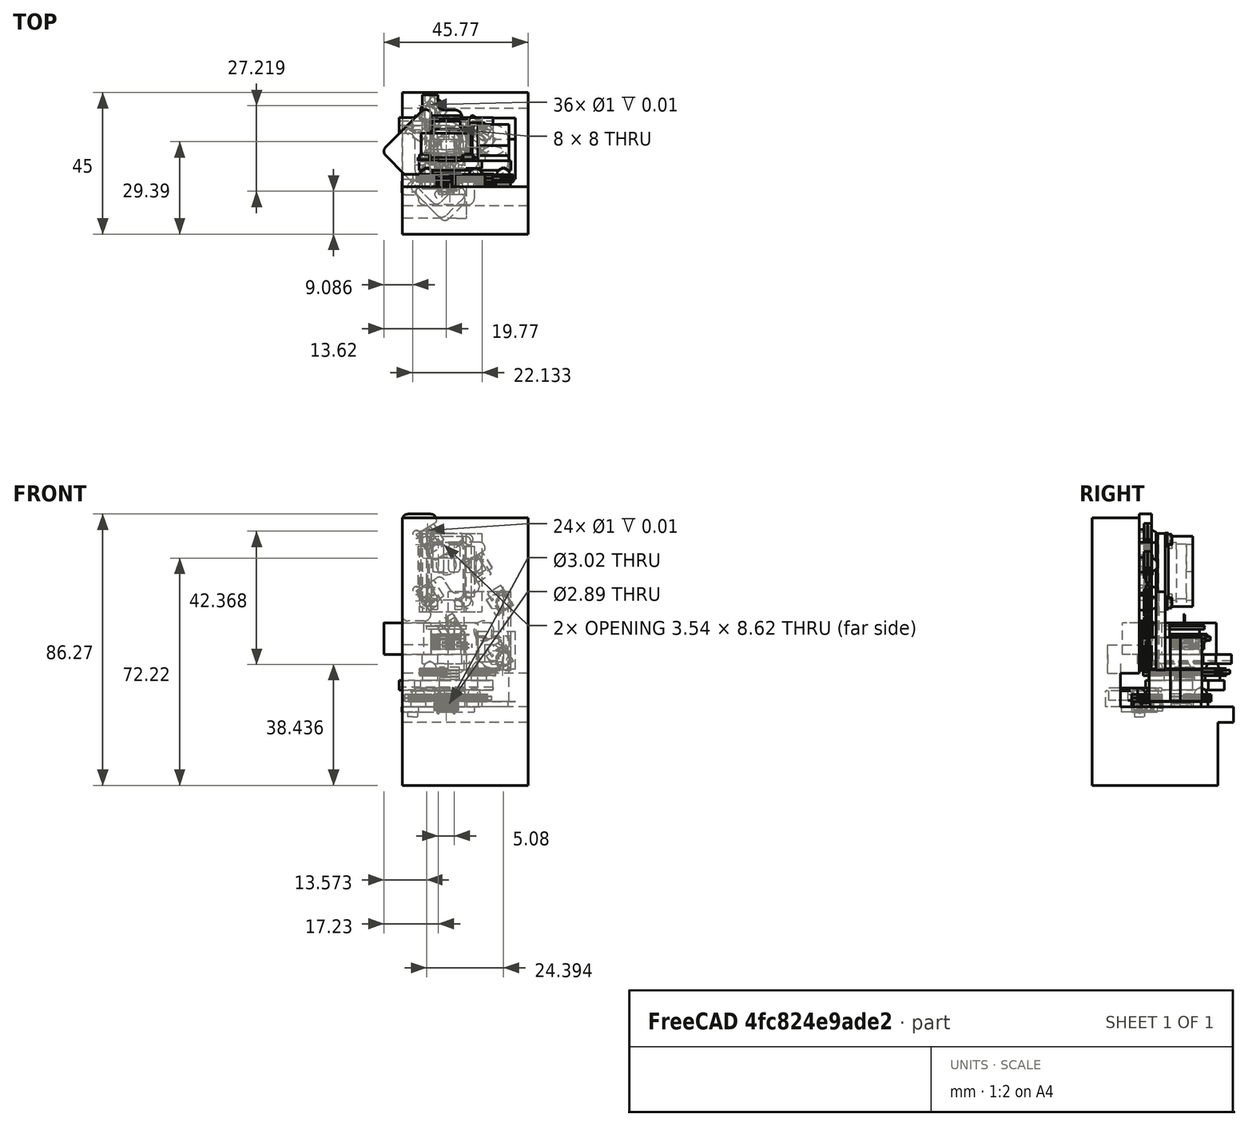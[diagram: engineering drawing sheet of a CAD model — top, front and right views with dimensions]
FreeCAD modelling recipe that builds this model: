
FCSTD DOCUMENT  (FreeCAD 1.1R20260223 (Git shallow))
Label: PhaseII
License: All rights reserved
LicenseURL: https://en.wikipedia.org/wiki/All_rights_reserved
objects: Part::Box×200, Part::Cut×118, Part::Cylinder×102, App::DocumentObjectGroup×31, Sketcher::SketchObject×30, App::Point×20, PartDesign::Pocket×18, Part::Feature×15, Part::Sphere×13, PartDesign::Fillet×13, PartDesign::Pad×11, PartDesign::Body×11, App::Part×9, App::Link×3, Fem::ConstraintFixed×2, PartDesign::CoordinateSystem×1, Fem::FemSolverObjectPython×1, App::MaterialObjectPython×1, Fem::FemMeshShapeBaseObjectPython×1, Fem::FemAnalysis×1
note: 646 computed .brp shape members not serialized (recipe doc carries the construction recipe); baked Part::Feature solids carry a one-line shape summary decoded from their .brp

FEATURE [App::Point] Origin027  label="Origin035"
  Role = Origin
FEATURE [Sketcher::SketchObject] Sketch003
  ArcFitTolerance = 1e-06
  AttachmentSupport = -> [Origin026]
  ExternalTypes = [0]
  FullyConstrained = true
  MakeInternals = false
  MapMode = 5
  sketch-geometry (4):
    g0: LineSegment StartX=7.94 StartY=11.17 StartZ=0 EndX=-7.94 EndY=11.17 EndZ=0
    g1: LineSegment StartX=-7.94 StartY=11.17 StartZ=0 EndX=-7.94 EndY=-11.17 EndZ=0
    g2: LineSegment StartX=-7.94 StartY=-11.17 StartZ=0 EndX=7.94 EndY=-11.17 EndZ=0
    g3: LineSegment StartX=7.94 StartY=-11.17 StartZ=0 EndX=7.94 EndY=11.17 EndZ=0
  constraints (12):
    c: Coincident(g0,g1)
    c: Coincident(g1,g2)
    c: Coincident(g2,g3)
    c: Coincident(g3,g0)
    c: Horizontal(g0)
    c: Horizontal(g2)
    c: Vertical(g1)
    c: Vertical(g3)
    c: DistanceY(g1,g1) = 22.34
    c: DistanceX(g0,g0) = 15.88
    c: Distance(g-1,g0) = 11.17
    c: Distance(g-1,g1) = 7.94
FEATURE [PartDesign::Pad] Pad001
  Direction = (0,0,1)
  Length = 7.7
  Length2 = 10
  Profile = -> Sketch003
  ReferenceAxis = -> Sketch003 [N_Axis]
  Refine = true
  SideType = 0
  Suppressed = false
  Type = 0
  Type2 = 0
FEATURE [Sketcher::SketchObject] Sketch004
  ArcFitTolerance = 1e-06
  AttachmentSupport = -> [Origin026]
  ExternalTypes = [0]
  FullyConstrained = true
  MakeInternals = false
  MapMode = 5
  sketch-geometry (8):
    g0: LineSegment StartX=-3.69 StartY=8.67 StartZ=0 EndX=3.69 EndY=8.67 EndZ=0
    g1: LineSegment StartX=5.44 StartY=6.92 StartZ=0 EndX=5.44 EndY=-6.92 EndZ=0
    g2: LineSegment StartX=3.69 StartY=-8.67 StartZ=0 EndX=-3.69 EndY=-8.67 EndZ=0
    g3: LineSegment StartX=-5.44 StartY=-6.92 StartZ=0 EndX=-5.44 EndY=6.92 EndZ=0
    g4: ArcOfCircle CenterX=-3.69 CenterY=6.92 CenterZ=0 NormalX=0 NormalY=0 NormalZ=1 AngleXU=0 Radius=1.75 StartAngle=1.5708 EndAngle=3.14159
    g5: ArcOfCircle CenterX=3.69 CenterY=6.92 CenterZ=0 NormalX=0 NormalY=0 NormalZ=1 AngleXU=0 Radius=1.75 StartAngle=0 EndAngle=1.5708
    g6: ArcOfCircle CenterX=-3.69 CenterY=-6.92 CenterZ=0 NormalX=0 NormalY=0 NormalZ=1 AngleXU=0 Radius=1.75 StartAngle=3.14159 EndAngle=4.71239
    g7: ArcOfCircle CenterX=3.69 CenterY=-6.92 CenterZ=0 NormalX=0 NormalY=0 NormalZ=1 AngleXU=0 Radius=1.75 StartAngle=4.71239 EndAngle=6.28319
  constraints (20):
    c: Horizontal(g0)
    c: Vertical(g1)
    c: Horizontal(g2)
    c: Vertical(g3)
    c: Radius(g4) = 1.75
    c: Distance(g-1,g0) = 8.67
    c: Distance(g-1,g2) = 8.67
    c: Distance(g-1,g1) = 5.44
    c: Distance(g-1,g3) = 5.44
    c: Tangent(g0,g4) = 1.5708
    c: Tangent(g3,g4) = 1.5708
    c: Radius(g5) = 1.75
    c: Tangent(g1,g5) = 1.5708
    c: Tangent(g5,g0) = 1.5708
    c: Radius(g6) = 1.75
    c: Radius(g7) = 1.75
    c: Tangent(g6,g3) = 1.5708
    c: Tangent(g2,g6) = 1.5708
    c: Tangent(g7,g1) = 1.5708
    c: Tangent(g7,g2) = 1.5708
FEATURE [Sketcher::SketchObject] Sketch006
  ArcFitTolerance = 1e-06
  AttachmentSupport = -> [Origin026]
  ExternalTypes = [0]
  FullyConstrained = true
  MakeInternals = false
  MapMode = 5
  sketch-geometry (14):
    g0: LineSegment StartX=5.99 StartY=6.92 StartZ=0 EndX=5.99 EndY=-6.92 EndZ=0
    g1: LineSegment StartX=3.69 StartY=-9.22 StartZ=0 EndX=-3.69 EndY=-9.22 EndZ=0
    g2: LineSegment StartX=-5.99 StartY=-6.92 StartZ=0 EndX=-5.99 EndY=6.92 EndZ=0
    g3: ArcOfCircle CenterX=-3.69 CenterY=6.92 CenterZ=0 NormalX=0 NormalY=0 NormalZ=1 AngleXU=0 Radius=2.3 StartAngle=1.5708 EndAngle=3.14159
    g4: ArcOfCircle CenterX=3.69 CenterY=6.92 CenterZ=0 NormalX=0 NormalY=0 NormalZ=1 AngleXU=0 Radius=2.3 StartAngle=0 EndAngle=1.5708
    g5: ArcOfCircle CenterX=-3.69 CenterY=-6.92 CenterZ=0 NormalX=0 NormalY=0 NormalZ=1 AngleXU=0 Radius=2.3 StartAngle=3.14159 EndAngle=4.71239
    g6: ArcOfCircle CenterX=3.69 CenterY=-6.92 CenterZ=0 NormalX=0 NormalY=0 NormalZ=1 AngleXU=0 Radius=2.3 StartAngle=4.71239 EndAngle=6.28319
    g7: LineSegment StartX=2.72 StartY=11.17 StartZ=0 EndX=2.72 EndY=9.97 EndZ=0
    g8: LineSegment StartX=-2.72 StartY=11.17 StartZ=0 EndX=-2.72 EndY=9.97 EndZ=0
    g9: LineSegment StartX=2.72 StartY=11.17 StartZ=0 EndX=-2.72 EndY=11.17 EndZ=0
    g10: LineSegment StartX=3.69 StartY=9.22 StartZ=0 EndX=3.47 EndY=9.22 EndZ=0
    g11: LineSegment StartX=-3.69 StartY=9.22 StartZ=0 EndX=-3.47 EndY=9.22 EndZ=0
    g12: ArcOfCircle CenterX=-3.47 CenterY=9.97 CenterZ=0 NormalX=0 NormalY=0 NormalZ=1 AngleXU=0 Radius=0.75 StartAngle=4.71239 EndAngle=6.28319
    g13: ArcOfCircle CenterX=3.47 CenterY=9.97 CenterZ=0 NormalX=0 NormalY=0 NormalZ=1 AngleXU=0 Radius=0.75 StartAngle=3.14159 EndAngle=4.71239
  constraints (37):
    c: Vertical(g0)
    c: Horizontal(g1)
    c: Vertical(g2)
    c: Distance(g-1,g0) = 5.99
    c: Tangent(g2,g3) = 1.5708
    c: Radius(g4) = 2.3
    c: Tangent(g0,g4) = 1.5708
    c: Tangent(g5,g2) = 1.5708
    c: Tangent(g1,g5) = 1.5708
    c: Tangent(g6,g0) = 1.5708
    c: Tangent(g6,g1) = 1.5708
    c: Vertical(g7)
    c: Vertical(g8)
    c: Distance(g-1,g7) = 2.72
    c: Distance(g-1,g8) = 2.72
    c: Coincident(g9,g7)
    c: Coincident(g9,g8)
    c: Horizontal(g9)
    c: Distance(g-1,g9) = 11.17
    c: Coincident(g10,g4)
    c: Horizontal(g10)
    c: Coincident(g11,g3)
    c: Horizontal(g11)
    c: Radius(g13) = 0.75
    c: Radius(g12) = 0.75
    c: Distance(g-1,g11) = 9.22
    c: Distance(g-1,g10) = 9.22
    c: Tangent(g12,g11) = -1.5708
    c: Tangent(g12,g8) = 1.5708
    c: Tangent(g13,g10) = 1.5708
    c: Tangent(g13,g7) = -1.5708
    c: Angle(g3) = 1.5708
    c: Angle(g4) = 1.5708
    c: Equal(g6,g4)
    c: Equal(g4,g3)
    c: Equal(g3,g5)
    c: Symmetric(g0,g2,g-1)
FEATURE [Part::Cylinder] Cylinder013  label="KJ_D21SH"
  Angle = 360
  AttacherType = Attacher::AttachEngine3D
  FirstAngle = 0
  Height = 1.59
  Placement = pos=(6.94,8.74,32.91) rot=(1,0,0;4.71239rad)
  Radius = 1.59
  SecondAngle = 0
FEATURE [Part::Cylinder] Cylinder014  label="KJ_D21SH001"
  Angle = 360
  AttacherType = Attacher::AttachEngine3D
  FirstAngle = 0
  Height = 1.59
  Placement = pos=(6.94,8.74,53.25) rot=(1,0,0;4.71239rad)
  Radius = 1.59
  SecondAngle = 0
FEATURE [Part::Cylinder] Cylinder015  label="KJ_D21SH002"
  Angle = 360
  AttacherType = Attacher::AttachEngine3D
  FirstAngle = 0
  Height = 1.59
  Placement = pos=(-6.94,8.74,32.91) rot=(1,0,0;4.71239rad)
  Radius = 1.59
  SecondAngle = 0
FEATURE [Part::Cylinder] Cylinder016  label="KJ_D21SH003"
  Angle = 360
  AttacherType = Attacher::AttachEngine3D
  FirstAngle = 0
  Height = 1.59
  Placement = pos=(-6.94,8.74,53.25) rot=(1,0,0;4.71239rad)
  Radius = 1.59
  SecondAngle = 0
FEATURE [Part::Box] Box046  label="Conductive Gasket"
  AttacherType = Attacher::AttachEngine3D
  Height = 1
  Length = 3
  Placement = pos=(5.94,8.33,51.08) rot=(1,0,0;4.71239rad)
  Width = 16
FEATURE [Part::Box] Box047  label="Conductive Gasket001"
  AttacherType = Attacher::AttachEngine3D
  Height = 1
  Length = 3
  Placement = pos=(-8.94,8.33,51.08) rot=(1,0,0;4.71239rad)
  Width = 16
FEATURE [Part::Box] Box048  label="Conductive Gasket002"
  AttacherType = Attacher::AttachEngine3D
  Height = 1
  Length = 10
  Placement = pos=(-5,8.33,55.25) rot=(1,0,0;4.71239rad)
  Width = 3
FEATURE [Part::Box] Box049  label="Conductive Gasket003"
  AttacherType = Attacher::AttachEngine3D
  Height = 1
  Length = 2.3
  Placement = pos=(2.72,8.33,33.91) rot=(1,0,0;4.71239rad)
  Width = 3
FEATURE [Part::Box] Box050  label="Conductive Gasket004"
  AttacherType = Attacher::AttachEngine3D
  Height = 1
  Length = 2.3
  Placement = pos=(-5.02,8.33,33.91) rot=(1,0,0;4.71239rad)
  Width = 3
FEATURE [App::DocumentObjectGroup] Group006  label="PreAmp Shield Gasket"
  Group = -> [Cylinder013,Cylinder014,Cylinder015,Cylinder016,Box046,Box047,Box048,Box049,Box050]
FEATURE [Sketcher::SketchObject] Sketch007
  ArcFitTolerance = 1e-06
  AttachmentSupport = -> [Origin026]
  ExternalTypes = [0]
  FullyConstrained = true
  MakeInternals = false
  MapMode = 5
  sketch-geometry (4):
    g0: LineSegment StartX=2.72 StartY=11.17 StartZ=0 EndX=-2.72 EndY=11.17 EndZ=0
    g1: LineSegment StartX=-2.72 StartY=11.17 StartZ=0 EndX=-2.72 EndY=8.5 EndZ=0
    g2: LineSegment StartX=-2.72 StartY=8.5 StartZ=0 EndX=2.72 EndY=8.5 EndZ=0
    g3: LineSegment StartX=2.72 StartY=8.5 StartZ=0 EndX=2.72 EndY=11.17 EndZ=0
  constraints (12):
    c: Coincident(g0,g1)
    c: Coincident(g1,g2)
    c: Coincident(g2,g3)
    c: Coincident(g3,g0)
    c: Horizontal(g0)
    c: Horizontal(g2)
    c: Vertical(g1)
    c: Vertical(g3)
    c: Distance(g-1,g3) = 2.72
    c: Distance(g-1,g1) = 2.72
    c: Distance(g-1,g0) = 11.17
    c: Distance(g-1,g2) = 8.5
FEATURE [Sketcher::SketchObject] Sketch008
  ArcFitTolerance = 1e-06
  AttachmentSupport = -> [Origin026]
  ExternalTypes = [0]
  FullyConstrained = true
  MakeInternals = false
  MapMode = 5
  sketch-geometry (6):
    g0: LineSegment StartX=2.72 StartY=11.17 StartZ=0 EndX=2.72 EndY=9.97 EndZ=0
    g1: LineSegment StartX=-2.72 StartY=11.17 StartZ=0 EndX=-2.72 EndY=9.97 EndZ=0
    g2: LineSegment StartX=2.72 StartY=11.17 StartZ=0 EndX=-2.72 EndY=11.17 EndZ=0
    g3: LineSegment StartX=1.97 StartY=9.22 StartZ=0 EndX=-1.97 EndY=9.22 EndZ=0
    g4: ArcOfCircle CenterX=1.97 CenterY=9.97 CenterZ=0 NormalX=0 NormalY=0 NormalZ=1 AngleXU=0 Radius=0.75 StartAngle=4.71239 EndAngle=6.28319
    g5: ArcOfCircle CenterX=-1.97 CenterY=9.97 CenterZ=0 NormalX=0 NormalY=0 NormalZ=1 AngleXU=0 Radius=0.75 StartAngle=3.14159 EndAngle=4.71239
  constraints (16):
    c: Vertical(g1)
    c: Coincident(g2,g0)
    c: Coincident(g2,g1)
    c: Horizontal(g2)
    c: Horizontal(g3)
    c: Vertical(g0)
    c: Distance(g-1,g2) = 11.17
    c: Distance(g-1,g3) = 9.22
    c: Distance(g-1,g1) = 2.72
    c: Distance(g-1,g0) = 2.72
    c: Radius(g4) = 0.75
    c: Tangent(g4,g0) = 1.5708
    c: Tangent(g4,g3) = 1.5708
    c: Tangent(g1,g5) = -1.5708
    c: Tangent(g5,g3) = 1.5708
    c: Radius(g5) = 0.75
FEATURE [PartDesign::Pocket] Pocket002
  BaseFeature = -> Pad001
  Direction = (0,0,-1)
  Length = 5.7
  Length2 = 5
  Profile = -> Sketch004
  ReferenceAxis = -> Sketch004 [N_Axis]
  Refine = true
  Reversed = true
  SideType = 0
  Suppressed = false
  Type = 0
  Type2 = 0
FEATURE [PartDesign::Pocket] Pocket003
  BaseFeature = -> Pocket002
  Direction = (0,0,-1)
  Length = 2.52
  Length2 = 5
  Profile = -> Sketch006
  ReferenceAxis = -> Sketch006 [N_Axis]
  Refine = true
  Reversed = true
  SideType = 0
  Suppressed = false
  Type = 0
  Type2 = 0
FEATURE [PartDesign::Pocket] Pocket004
  BaseFeature = -> Pocket003
  Direction = (0,0,-1)
  Length = 5.7
  Length2 = 5
  Profile = -> Sketch007
  ReferenceAxis = -> Sketch007 [N_Axis]
  Refine = true
  Reversed = true
  SideType = 0
  Suppressed = false
  Type = 0
  Type2 = 0
FEATURE [PartDesign::Pocket] Pocket005
  BaseFeature = -> Pocket004
  Direction = (0,0,-1)
  Length = 9
  Length2 = 5
  Profile = -> Sketch008
  ReferenceAxis = -> Sketch008 [N_Axis]
  Refine = true
  Reversed = true
  SideType = 0
  Suppressed = false
  Type = 1
  Type2 = 0
FEATURE [Sketcher::SketchObject] Sketch009
  ArcFitTolerance = 1e-06
  AttachmentOffset = pos=(0,0,7.7) rot=(0,0,1;0rad)
  AttachmentSupport = -> [Origin026]
  ExternalTypes = [0]
  FullyConstrained = true
  MakeInternals = false
  MapMode = 5
  Placement = pos=(0,0,7.7) rot=(0,0,1;0rad)
  sketch-geometry (18):
    g0: LineSegment StartX=-0.77 StartY=-0.58 StartZ=0 EndX=-0.77 EndY=-7.7 EndZ=0
    g1: LineSegment StartX=-4.31 StartY=-7.7 StartZ=0 EndX=-4.31 EndY=-0.58 EndZ=0
    g2: LineSegment StartX=0.77 StartY=-0.58 StartZ=0 EndX=0.77 EndY=-7.7 EndZ=0
    g3: LineSegment StartX=4.31 StartY=-7.7 StartZ=0 EndX=4.31 EndY=-0.58 EndZ=0
    g4: ArcOfCircle CenterX=-3.56 CenterY=-0.58 CenterZ=0 NormalX=0 NormalY=0 NormalZ=1 AngleXU=0 Radius=0.75 StartAngle=1.5708 EndAngle=3.14159
    g5: ArcOfCircle CenterX=-1.52 CenterY=-0.58 CenterZ=0 NormalX=0 NormalY=0 NormalZ=1 AngleXU=0 Radius=0.75 StartAngle=0 EndAngle=1.5708
    g6: ArcOfCircle CenterX=-3.56 CenterY=-7.7 CenterZ=0 NormalX=0 NormalY=0 NormalZ=1 AngleXU=0 Radius=0.75 StartAngle=3.14159 EndAngle=4.71239
    g7: ArcOfCircle CenterX=-1.52 CenterY=-7.7 CenterZ=0 NormalX=0 NormalY=0 NormalZ=1 AngleXU=0 Radius=0.75 StartAngle=4.71239 EndAngle=6.28319
    g8: ArcOfCircle CenterX=1.52 CenterY=-7.7 CenterZ=0 NormalX=0 NormalY=0 NormalZ=1 AngleXU=0 Radius=0.75 StartAngle=3.14159 EndAngle=4.71239
    g9: ArcOfCircle CenterX=3.56 CenterY=-7.7 CenterZ=0 NormalX=0 NormalY=0 NormalZ=1 AngleXU=0 Radius=0.75 StartAngle=4.71239 EndAngle=6.28319
    g10: ArcOfCircle CenterX=1.52 CenterY=-0.58 CenterZ=0 NormalX=0 NormalY=0 NormalZ=1 AngleXU=0 Radius=0.75 StartAngle=1.5708 EndAngle=3.14159
    g11: ArcOfCircle CenterX=3.56 CenterY=-0.58 CenterZ=0 NormalX=0 NormalY=0 NormalZ=1 AngleXU=0 Radius=0.75 StartAngle=0 EndAngle=1.5708
    g12: GeomPoint [constr] X=-2.54 Y=-4.14 Z=0
    g13: GeomPoint [constr] X=2.54 Y=-4.14 Z=0
    g14: LineSegment StartX=-3.56 StartY=0.17 StartZ=0 EndX=-1.52 EndY=0.17 EndZ=0
    g15: LineSegment StartX=-3.56 StartY=-8.45 StartZ=0 EndX=-1.52 EndY=-8.45 EndZ=0
    g16: LineSegment StartX=1.52 StartY=0.17 StartZ=0 EndX=3.56 EndY=0.17 EndZ=0
    g17: LineSegment StartX=1.52 StartY=-8.45 StartZ=0 EndX=3.56 EndY=-8.45 EndZ=0
  constraints (51):
    c: Vertical(g1)
    c: Vertical(g2)
    c: Vertical(g3)
    c: Equal(g1,g0)
    c: Equal(g2,g3)
    c: Radius(g4) = 0.75
    c: Angle(g4) = 1.5708
    c: Equal(g4,g5)
    c: DistanceX(g-2,g12) = -2.54
    c: DistanceX(g-2,g13) = 2.54
    c: DistanceY(g-1,g12) = -4.14
    c: DistanceY(g-1,g13) = -4.14
    c: Angle(g5) = 1.5708
    c: Angle(g6) = 1.5708
    c: Angle(g7) = 1.5708
    c: Angle(g8) = 1.5708
    c: Angle(g9) = 1.5708
    c: Angle(g10) = 1.5708
    c: Angle(g11) = 1.5708
    c: Equal(g4,g10)
    c: Equal(g4,g11)
    c: Equal(g6,g4)
    c: Equal(g7,g4)
    c: Equal(g4,g8)
    c: Equal(g4,g9)
    c: Horizontal(g14)
    c: Tangent(g4,g14) = 1.5708
    c: Tangent(g14,g5) = 1.5708
    c: Coincident(g4,g1)
    c: Coincident(g0,g5)
    c: DistanceX(g14,g14) = 2.04
    c: Tangent(g6,g15) = -1.5708
    c: Tangent(g15,g7) = -1.5708
    c: Coincident(g7,g0)
    c: Equal(g15,g14)
    c: Symmetric(g1,g0,g12)
    c: Horizontal(g16)
    c: Horizontal(g17)
    c: Tangent(g10,g16) = 1.5708
    c: Tangent(g16,g11) = 1.5708
    c: Tangent(g8,g17) = -1.5708
    c: Tangent(g17,g9) = -1.5708
    c: Coincident(g2,g10)
    c: Coincident(g3,g11)
    c: Coincident(g8,g2)
    c: Equal(g17,g16)
    c: Symmetric(g2,g3,g13)
    c: Equal(g16,g14)
    c: Equal(g0,g2)
    c: Distance(g12,g14) = 4.31
    c: Coincident(g1,g6)
FEATURE [PartDesign::Pocket] Pocket006
  BaseFeature = -> Pocket005
  Direction = (0,0,-1)
  Length = 2
  Length2 = 5
  Profile = -> Sketch009
  ReferenceAxis = -> Sketch009 [N_Axis]
  Refine = true
  SideType = 0
  Suppressed = false
  Type = 0
  Type2 = 0
FEATURE [Sketcher::SketchObject] Sketch010
  ArcFitTolerance = 1e-06
  AttachmentSupport = -> [Origin026]
  ExternalTypes = [0]
  FullyConstrained = true
  MakeInternals = false
  MapMode = 5
  sketch-geometry (28):
    g0: LineSegment StartX=5.23 StartY=13.43 StartZ=0 EndX=10.23 EndY=13.43 EndZ=0
    g1: LineSegment StartX=10.23 StartY=13.43 StartZ=0 EndX=10.23 EndY=8.43 EndZ=0
    g2: LineSegment [constr] StartX=5.23 StartY=13.43 StartZ=0 EndX=5.23 EndY=8.43 EndZ=0
    g3: LineSegment [constr] StartX=10.23 StartY=8.43 StartZ=0 EndX=5.23 EndY=8.43 EndZ=0
    g4: ArcOfCircle CenterX=5.23 CenterY=8.43 CenterZ=0 NormalX=0 NormalY=0 NormalZ=1 AngleXU=0 Radius=1.4 StartAngle=1.5708 EndAngle=6.28319
    g5: LineSegment StartX=6.63 StartY=8.43 StartZ=0 EndX=10.23 EndY=8.43 EndZ=0
    g6: LineSegment StartX=5.23 StartY=9.83 StartZ=0 EndX=5.23 EndY=13.43 EndZ=0
    g7: LineSegment [constr] StartX=-5.23 StartY=8.43 StartZ=0 EndX=-5.23 EndY=13.43 EndZ=0
    g8: LineSegment StartX=-5.23 StartY=13.43 StartZ=0 EndX=-10.23 EndY=13.43 EndZ=0
    g9: LineSegment StartX=-10.23 StartY=13.43 StartZ=0 EndX=-10.23 EndY=8.43 EndZ=0
    g10: LineSegment [constr] StartX=-10.23 StartY=8.43 StartZ=0 EndX=-5.23 EndY=8.43 EndZ=0
    g11: LineSegment [constr] StartX=5.23 StartY=-8.43 StartZ=0 EndX=5.23 EndY=-13.43 EndZ=0
    g12: LineSegment StartX=5.23 StartY=-13.43 StartZ=0 EndX=10.23 EndY=-13.43 EndZ=0
    g13: LineSegment StartX=10.23 StartY=-13.43 StartZ=0 EndX=10.23 EndY=-8.43 EndZ=0
    g14: LineSegment [constr] StartX=10.23 StartY=-8.43 StartZ=0 EndX=5.23 EndY=-8.43 EndZ=0
    g15: LineSegment StartX=-10.23 StartY=-13.43 StartZ=0 EndX=-5.23 EndY=-13.43 EndZ=0
    g16: LineSegment [constr] StartX=-5.23 StartY=-13.43 StartZ=0 EndX=-5.23 EndY=-8.43 EndZ=0
    g17: LineSegment StartX=-10.23 StartY=-13.43 StartZ=0 EndX=-10.23 EndY=-8.43 EndZ=0
    g18: LineSegment [constr] StartX=-10.23 StartY=-8.43 StartZ=0 EndX=-5.23 EndY=-8.43 EndZ=0
    g19: ArcOfCircle CenterX=-5.23 CenterY=8.43 CenterZ=0 NormalX=0 NormalY=0 NormalZ=1 AngleXU=0 Radius=1.4 StartAngle=3.14159 EndAngle=7.85398
    g20: ArcOfCircle CenterX=-5.23 CenterY=-8.43 CenterZ=0 NormalX=0 NormalY=0 NormalZ=1 AngleXU=0 Radius=1.4 StartAngle=4.71239 EndAngle=9.42478
    g21: ArcOfCircle CenterX=5.23 CenterY=-8.43 CenterZ=0 NormalX=0 NormalY=0 NormalZ=1 AngleXU=0 Radius=1.4 StartAngle=0 EndAngle=4.71239
    g22: LineSegment StartX=-10.23 StartY=-8.43 StartZ=0 EndX=-6.63 EndY=-8.43 EndZ=0
    g23: LineSegment StartX=-5.23 StartY=-13.43 StartZ=0 EndX=-5.23 EndY=-9.83 EndZ=0
    g24: LineSegment StartX=5.23 StartY=-13.43 StartZ=0 EndX=5.23 EndY=-9.83 EndZ=0
    g25: LineSegment StartX=6.63 StartY=-8.43 StartZ=0 EndX=10.23 EndY=-8.43 EndZ=0
    g26: LineSegment StartX=-10.23 StartY=8.43 StartZ=0 EndX=-6.63 EndY=8.43 EndZ=0
    g27: LineSegment StartX=-5.23 StartY=13.43 StartZ=0 EndX=-5.23 EndY=9.83 EndZ=0
  constraints (77):
    c: Horizontal(g0)
    c: Coincident(g1,g0)
    c: Vertical(g1)
    c: DistanceX(g-2,g0) = 5.23
    c: DistanceY(g-1,g1) = 8.43
    c: DistanceX(g0,g0) = 5
    c: Equal(g0,g1)
    c: Coincident(g2,g0)
    c: Vertical(g2)
    c: Coincident(g3,g1)
    c: Horizontal(g3)
    c: Coincident(g2,g3)
    c: Coincident(g4,g2)
    c: PointOnObject(g4,g3)
    c: PointOnObject(g4,g2)
    c: Radius(g4) = 1.4
    c: Coincident(g5,g4)
    c: Coincident(g5,g1)
    c: Coincident(g6,g4)
    c: Coincident(g6,g0)
    c: Vertical(g7)
    c: Coincident(g8,g7)
    c: Horizontal(g8)
    c: Coincident(g9,g8)
    c: Vertical(g9)
    c: Coincident(g10,g9)
    c: Coincident(g10,g7)
    c: Horizontal(g10)
    c: Vertical(g11)
    c: Coincident(g12,g11)
    c: Horizontal(g12)
    c: Coincident(g13,g12)
    c: Vertical(g13)
    c: Coincident(g14,g13)
    c: Horizontal(g14)
    c: Coincident(g11,g14)
    c: Horizontal(g15)
    c: Coincident(g16,g15)
    c: Vertical(g16)
    c: Coincident(g17,g15)
    c: Vertical(g17)
    c: Coincident(g18,g17)
    c: Coincident(g18,g16)
    c: Horizontal(g18)
    c: Equal(g0,g13)
    c: Equal(g13,g12)
    c: Equal(g12,g15)
    c: Equal(g15,g17)
    c: Equal(g17,g9)
    c: Equal(g9,g8)
    c: Symmetric(g2,g16,g-1)
    c: Symmetric(g7,g11,g-1)
    c: Symmetric(g7,g2,g-2)
    c: Coincident(g21,g11)
    c: PointOnObject(g21,g11)
    c: PointOnObject(g21,g14)
    c: Equal(g4,g21)
    c: Equal(g21,g20)
    c: Equal(g20,g19)
    c: PointOnObject(g20,g16)
    c: PointOnObject(g20,g18)
    c: Coincident(g16,g20)
    c: Coincident(g7,g19)
    c: PointOnObject(g19,g10)
    c: PointOnObject(g19,g7)
    c: Coincident(g22,g17)
    c: Coincident(g22,g20)
    c: Coincident(g23,g15)
    c: Coincident(g23,g20)
    c: Coincident(g24,g11)
    c: Coincident(g24,g21)
    c: Coincident(g25,g21)
    c: Coincident(g25,g13)
    c: Coincident(g26,g9)
    c: Coincident(g26,g19)
    c: Coincident(g27,g7)
    c: Coincident(g27,g19)
FEATURE [PartDesign::Pocket] Pocket007
  BaseFeature = -> Pocket006
  Direction = (0,0,-1)
  Length = 1.1
  Length2 = 5
  Profile = -> Sketch010
  ReferenceAxis = -> Sketch010 [N_Axis]
  Refine = true
  Reversed = true
  SideType = 0
  Suppressed = false
  Type = 0
  Type2 = 0
FEATURE [App::Point] Origin003
  Role = Origin
FEATURE [PartDesign::CoordinateSystem] Local_CS_e57a
  AttacherType = Attacher::AttachEngine3D
  MapMode = 2
FEATURE [App::Point] Origin001
  Role = Origin
FEATURE [Part::Feature] Pcb_e57a
  Placement = pos=(-166.34,98.15,0) rot=(0,0,1;0rad)
  shape: bbox 23.01 x 11.38 x 1.626 mm, 18 faces (baked)
FEATURE [Sketcher::SketchObject] PCB_Sketch_e57a
  ArcFitTolerance = 1e-06
  ExternalTypes = [0]
  FullyConstrained = false
  MakeInternals = false
  sketch-geometry (16):
    g0: LineSegment StartX=-14.09 StartY=-1.42 StartZ=0 EndX=-14.09 EndY=1.42 EndZ=0
    g1: LineSegment StartX=-8.92 StartY=-3.42 StartZ=0 EndX=-8.92 EndY=-3.69 EndZ=0
    g2: LineSegment StartX=-13.09 StartY=2.42 StartZ=0 EndX=-9.92 EndY=2.42 EndZ=0
    g3: LineSegment StartX=-13.09 StartY=-2.42 StartZ=0 EndX=-9.92 EndY=-2.42 EndZ=0
    g4: LineSegment StartX=8.92 StartY=3.69 StartZ=0 EndX=8.92 EndY=-3.69 EndZ=0
    g5: LineSegment StartX=-6.92 StartY=5.69 StartZ=0 EndX=6.92 EndY=5.69 EndZ=0
    g6: LineSegment StartX=6.92 StartY=-5.69 StartZ=0 EndX=-6.92 EndY=-5.69 EndZ=0
    g7: LineSegment StartX=-8.92 StartY=3.69 StartZ=0 EndX=-8.92 EndY=3.42 EndZ=0
    g8: ArcOfCircle CenterX=-13.09 CenterY=1.42 CenterZ=0 NormalX=0 NormalY=0 NormalZ=-1 AngleXU=-7.47076e-07 Radius=0.999999 StartAngle=0 EndAngle=1.5708
    g9: ArcOfCircle CenterX=-9.92 CenterY=-3.42 CenterZ=0 NormalX=0 NormalY=0 NormalZ=-1 AngleXU=1.5708 Radius=0.999999 StartAngle=0 EndAngle=1.5708
    g10: ArcOfCircle CenterX=-6.92 CenterY=3.69 CenterZ=0 NormalX=0 NormalY=0 NormalZ=-1 AngleXU=-7.47076e-07 Radius=2 StartAngle=0 EndAngle=1.5708
    g11: ArcOfCircle CenterX=6.92 CenterY=-3.69 CenterZ=0 NormalX=0 NormalY=0 NormalZ=-1 AngleXU=3.14159 Radius=2 StartAngle=0 EndAngle=1.5708
    g12: ArcOfCircle CenterX=6.92 CenterY=3.69 CenterZ=0 NormalX=0 NormalY=0 NormalZ=-1 AngleXU=1.5708 Radius=2 StartAngle=0 EndAngle=1.5708
    g13: ArcOfCircle CenterX=-9.92 CenterY=3.42 CenterZ=0 NormalX=0 NormalY=0 NormalZ=-1 AngleXU=3.14159 Radius=0.999999 StartAngle=0 EndAngle=1.5708
    g14: ArcOfCircle CenterX=-13.09 CenterY=-1.42 CenterZ=0 NormalX=0 NormalY=0 NormalZ=-1 AngleXU=-1.5708 Radius=0.999999 StartAngle=0 EndAngle=1.5708
    g15: ArcOfCircle CenterX=-6.92 CenterY=-3.69 CenterZ=0 NormalX=0 NormalY=0 NormalZ=-1 AngleXU=-1.5708 Radius=2 StartAngle=0 EndAngle=1.5708
  constraints (16):
    c: Coincident(g0,g14)
    c: Coincident(g0,g8)
    c: Coincident(g3,g14)
    c: Coincident(g2,g8)
    c: Coincident(g3,g9)
    c: Coincident(g2,g13)
    c: Coincident(g1,g15)
    c: Coincident(g1,g9)
    c: Coincident(g7,g13)
    c: Coincident(g7,g10)
    c: Coincident(g6,g15)
    c: Coincident(g5,g10)
    c: Coincident(g6,g11)
    c: Coincident(g5,g12)
    c: Coincident(g4,g11)
    c: Coincident(g4,g12)
FEATURE [App::Part] Board_Geoms_e57a
  Group = -> [Pcb_e57a,PCB_Sketch_e57a]
  Origin = -> Origin
FEATURE [App::Point] Origin005  label="Origin006"
  Role = Origin
FEATURE [App::Point] Origin007  label="Origin009"
  Role = Origin
FEATURE [App::Point] Origin019  label="Origin025"
  Role = Origin
FEATURE [App::Point] Origin017  label="Origin022"
  Role = Origin
FEATURE [Part::Feature] Part__Feature  label="NPPC021KFXC-RC_C03"
  shape: bbox 2.54 x 7.112 x 2.54 mm, 19 faces (baked)
FEATURE [Part::Feature] Part__Feature001  label="NPPC021KFXC-RC_C001"
  shape: bbox 2.54 x 7.112 x 2.54 mm, 19 faces (baked)
FEATURE [Part::Feature] Part__Feature002  label="NPPC021KFXC-RC_C002"
  shape: bbox 2.54 x 7.112 x 2.54 mm, 19 faces (baked)
FEATURE [App::Part] NPPC021KFXC_RC_C03  label="NPPC021KFXC-RC_C003"
  Group = -> [Part__Feature,Part__Feature001,Part__Feature002]
  Origin = -> Origin016
FEATURE [Part::Feature] Part__Feature003  label="Pin - Gold"
  Placement = pos=(-2.54,0,0) rot=(0,1,0;3.14159rad)
  shape: bbox 0.6096 x 0.889 x 1.702 mm, 12 faces (baked)
FEATURE [Part::Feature] Part__Feature004  label="Pin - Gold001"
  shape: bbox 0.6096 x 0.889 x 1.702 mm, 12 faces (baked)
FEATURE [Part::Feature] Part__Feature005  label="Pin - Gold002"
  Placement = pos=(2.54,0,0) rot=(0,1,0;3.14159rad)
  shape: bbox 0.6096 x 0.889 x 1.702 mm, 12 faces (baked)
FEATURE [App::Part] NPPC031KFXC_RC  label="J2_NPPC031KFXC-RC_092ddd3a27b6"
  Group = -> [NPPC021KFXC_RC_C03,Part__Feature003,Part__Feature004,Part__Feature005]
  Origin = -> Origin018
  Placement = pos=(4.14,-2.54,0) rot=(1,0,0;1.5708rad)
FEATURE [App::Point] Origin021  label="Origin028"
  Role = Origin
FEATURE [Part::Feature] Part__Feature006  label="ADP121-AUJZ30R7"
  shape: bbox 2.9 x 0.9 x 1.6 mm, 10 faces (baked)
FEATURE [Part::Feature] Part__Feature007  label="ADP121-AUJZ30R001"
  shape: bbox 0.4 x 0.72 x 0.6123 mm, 15 faces (baked)
FEATURE [Part::Feature] Part__Feature008  label="ADP121-AUJZ30R002"
  shape: bbox 0.4 x 0.72 x 0.6123 mm, 15 faces (baked)
FEATURE [Part::Feature] Part__Feature009  label="ADP121-AUJZ30R003"
  shape: bbox 0.4 x 0.72 x 0.6123 mm, 15 faces (baked)
FEATURE [Part::Feature] Part__Feature010  label="ADP121-AUJZ30R004"
  shape: bbox 0.4 x 0.72 x 0.6123 mm, 15 faces (baked)
FEATURE [Part::Feature] Part__Feature011  label="ADP121-AUJZ30R005"
  shape: bbox 0.4 x 0.72 x 0.6123 mm, 15 faces (baked)
FEATURE [App::Part] ADP121_AUJZ30R7  label="U1_ADP121-AUJZ30R006_c235f6473035"
  Group = -> [Part__Feature006,Part__Feature007,Part__Feature008,Part__Feature009,Part__Feature010,Part__Feature011]
  Origin = -> Origin020
  Placement = pos=(-6.32,0.09,0.645) rot=(0.57735,0.57735,0.57735;2.0944rad)
FEATURE [App::Point] Origin028  label="Origin037"
  Role = Origin
FEATURE [Part::Feature] Part__Feature012  label="MMCX-J-P-H-RA-SM1_body"
  shape: bbox 4.6 x 6.5 x 3.5 mm, 61 faces (baked)
FEATURE [App::Part] MMCX_J_P_H_RA_SM1  label="J1_MMCX-J-P-H-RA-SM1_25358a300291"
  Group = -> [Part__Feature012]
  Origin = -> Origin029
  Placement = pos=(-11.67,0,2.84) rot=(0.57735,-0.57735,0.57735;2.0944rad)
FEATURE [App::Link] J2_NPPC031KFXC_RC_092ddd3a27b6_ln_  label="J3_NPPC031KFXC-RC_da87777116d9"
  LinkPlacement = pos=(4.14,2.54,0) rot=(1,0,0;1.5708rad)
  LinkedObject = -> NPPC031KFXC_RC
  Placement = pos=(4.14,2.54,0) rot=(1,0,0;1.5708rad)
FEATURE [App::Part] Top_e57a
  Group = -> [NPPC031KFXC_RC,ADP121_AUJZ30R7,MMCX_J_P_H_RA_SM1,J2_NPPC031KFXC_RC_092ddd3a27b6_ln_]
  Origin = -> Origin006
FEATURE [App::Point] Origin009  label="Origin011"
  Role = Origin
FEATURE [Part::Feature] Shape  label="H1_Discs2_D21SH_3e0910014654"
  Placement = pos=(-10.67,0.03,-2.4156) rot=(1,0,0;1.5708rad)
  shape: bbox 3.175 x 3.175 x 1.588 mm, 4 faces (baked)
FEATURE [App::Link] H1_Discs2_D21SH_3e0910014654_ln_  label="H2_Discs2_D21SH_73186dc4d259"
  LinkPlacement = pos=(3e-16,3.355,-2.4156) rot=(1,0,0;1.5708rad)
  LinkedObject = -> Shape
  Placement = pos=(3e-16,3.355,-2.4156) rot=(1,0,0;1.5708rad)
FEATURE [App::Link] H1_Discs2_D21SH_3e0910014654_ln_001  label="H3_Discs2_D21SH_1b5fe099ede3"
  LinkPlacement = pos=(6.585,-3.355,-2.4156) rot=(1,0,0;1.5708rad)
  LinkedObject = -> Shape
  Placement = pos=(6.585,-3.355,-2.4156) rot=(1,0,0;1.5708rad)
FEATURE [App::Part] Bot_e57a
  Group = -> [Shape,H1_Discs2_D21SH_3e0910014654_ln_,H1_Discs2_D21SH_3e0910014654_ln_001]
  Origin = -> Origin008
FEATURE [App::Part] Step_Models_e57a
  Group = -> [Top_e57a,Bot_e57a]
  Origin = -> Origin004
FEATURE [App::Part] Board_e57a  label="PreAmp PCB"
  Group = -> [Local_CS_e57a,Board_Geoms_e57a,Step_Models_e57a]
  Origin = -> Origin002
  Placement = pos=(0,11.55,43.08) rot=(-0.57735,-0.57735,-0.57735;2.0944rad)
FEATURE [Part::Cylinder] Cylinder017  label="KJ_D31SH"
  Angle = 360
  AttacherType = Attacher::AttachEngine3D
  FirstAngle = 0
  Height = 1.59
  Radius = 2.38
  SecondAngle = 0
FEATURE [Part::Box] Box051  label="Small LiNbO3 Plate013"
  AttacherType = Attacher::AttachEngine3D
  Height = 0.5
  Length = 4.5
  Width = 5.5
FEATURE [Part::Cylinder] Cylinder018  label="Cylinder013"
  Angle = 360
  AttacherType = Attacher::AttachEngine3D
  FirstAngle = 0
  Height = 0.01
  Placement = pos=(1,4.5,0.49) rot=(0,0,1;0rad)
  Radius = 0.5
  SecondAngle = 0
FEATURE [Part::Cut] Cut005  label="Small LiNbO3 Plate"
  Base = -> Box051
  Placement = pos=(-2.38,-2.38,1.64) rot=(0,0,1;0rad)
  Refine = true
  Tool = -> Cylinder018
FEATURE [Part::Box] Box052  label="Small Cu GND Electrode009"
  AttacherType = Attacher::AttachEngine3D
  Height = 1.15
  Length = 6
  Width = 6.5
FEATURE [Part::Box] Box053  label="Small Cu GND Electrode010"
  AttacherType = Attacher::AttachEngine3D
  Height = 1.05
  Length = 6
  Placement = pos=(0,0,0.05) rot=(0,0,1;0rad)
  Width = 6.45
FEATURE [Part::Cut] Cut006  label="Small Cu Electrode, Short Axis, GND"
  Base = -> Box052
  Placement = pos=(-2.38,3.62,1.59) rot=(0,0,1;-1.5708rad)
  Refine = true
  Tool = -> Box053
FEATURE [Part::Box] Box054  label="Small LiNbO3 Plate014"
  AttacherType = Attacher::AttachEngine3D
  Height = 0.5
  Length = 4.5
  Width = 5.5
FEATURE [Part::Cylinder] Cylinder019
  Angle = 360
  AttacherType = Attacher::AttachEngine3D
  FirstAngle = 0
  Height = 0.01
  Placement = pos=(1,4.5,0.49) rot=(0,0,1;0rad)
  Radius = 0.5
  SecondAngle = 0
FEATURE [Part::Cut] Cut007  label="Small LiNbO3 Plate015"
  Base = -> Box054
  Placement = pos=(2.12,3.12,2.19) rot=(0,0,1;3.14159rad)
  Refine = true
  Tool = -> Cylinder019
FEATURE [Part::Box] Box055  label="Small Cu GND Electrode011"
  AttacherType = Attacher::AttachEngine3D
  Height = 1.2
  Length = 5
  Width = 7.5
FEATURE [Part::Box] Box056  label="Small Cu GND Electrode012"
  AttacherType = Attacher::AttachEngine3D
  Height = 1.1
  Length = 5
  Placement = pos=(0,0,0.05) rot=(0,0,1;0rad)
  Width = 7.45
FEATURE [Part::Cut] Cut008  label="Small Cu Electrode001, Long Axis, V"
  Base = -> Box055
  Placement = pos=(-2.38,-2.38,2.14) rot=(0,0,1;0rad)
  Refine = true
  Tool = -> Box056
FEATURE [Part::Box] Box057  label="Small Cu GND Electrode013"
  AttacherType = Attacher::AttachEngine3D
  Height = 1.15
  Length = 6
  Width = 6.5
FEATURE [Part::Box] Box058  label="Small Cu GND Electrode014"
  AttacherType = Attacher::AttachEngine3D
  Height = 1.05
  Length = 6
  Placement = pos=(0,0,0.05) rot=(0,0,1;0rad)
  Width = 6.45
FEATURE [Part::Cut] Cut009  label="Small Cu Electrode002, Short Axis, GND"
  Base = -> Box057
  Placement = pos=(-2.38,3.62,2.74) rot=(0,0,1;-1.5708rad)
  Refine = true
  Tool = -> Box058
FEATURE [Part::Box] Box059  label="Small LiNbO3 Plate016"
  AttacherType = Attacher::AttachEngine3D
  Height = 0.5
  Length = 4.5
  Width = 5.5
FEATURE [Part::Cylinder] Cylinder020
  Angle = 360
  AttacherType = Attacher::AttachEngine3D
  FirstAngle = 0
  Height = 0.01
  Placement = pos=(1,4.5,0.49) rot=(0,0,1;0rad)
  Radius = 0.5
  SecondAngle = 0
FEATURE [Part::Cut] Cut010  label="Small LiNbO3 Plate017"
  Base = -> Box059
  Placement = pos=(-2.38,-2.38,2.79) rot=(0,0,1;0rad)
  Refine = true
  Tool = -> Cylinder020
FEATURE [Part::Box] Box060  label="Small LiNbO3 Plate018"
  AttacherType = Attacher::AttachEngine3D
  Height = 0.5
  Length = 4.5
  Width = 5.5
FEATURE [Part::Cylinder] Cylinder021
  Angle = 360
  AttacherType = Attacher::AttachEngine3D
  FirstAngle = 0
  Height = 0.01
  Placement = pos=(1,4.5,0.49) rot=(0,0,1;0rad)
  Radius = 0.5
  SecondAngle = 0
FEATURE [Part::Cut] Cut011  label="Small LiNbO3 Plate019"
  Base = -> Box060
  Placement = pos=(2.12,3.12,3.34) rot=(0,0,1;3.14159rad)
  Refine = true
  Tool = -> Cylinder021
FEATURE [Part::Box] Box061  label="Cube004"
  AttacherType = Attacher::AttachEngine3D
  Height = 10
  Length = 10
  Placement = pos=(-5,-5,-10) rot=(0,0,1;0rad)
  Width = 10
FEATURE [Part::Sphere] Sphere004
  Angle1 = -90
  Angle2 = 90
  Angle3 = 360
  AttacherType = Attacher::AttachEngine3D
  Radius = 2
FEATURE [Part::Cut] Cut012  label="Sapphire Half-Ball Lens004"
  Base = -> Sphere004
  Placement = pos=(0,0,3.89) rot=(0,0,1;0rad)
  Refine = true
  Tool = -> Box061
FEATURE [App::DocumentObjectGroup] Group008  label="Coarse Piezo Stack"
  Group = -> [Cylinder017,Cut006,Cut005,Cut008,Cut007,Cut009,Cut010,Cut011,Cut012]
FEATURE [Part::Cylinder] Cylinder022  label="KJ_D61SH"
  Angle = 360
  AttacherType = Attacher::AttachEngine3D
  FirstAngle = 0
  Height = 1.59
  Placement = pos=(0,14.39,16.66) rot=(0,0,1;0rad)
  Radius = 4.76
  SecondAngle = 0
FEATURE [Part::Box] Box062  label="Large LiNbO3 Plate005"
  AttacherType = Attacher::AttachEngine3D
  Height = 0.5
  Length = 9
  Width = 11
FEATURE [Part::Cylinder] Cylinder023  label="Cylinder022"
  Angle = 360
  AttacherType = Attacher::AttachEngine3D
  FirstAngle = 0
  Height = 0.01
  Placement = pos=(1,10,0.49) rot=(0,0,1;0rad)
  Radius = 0.5
  SecondAngle = 0
FEATURE [Part::Cut] Cut013  label="Large LiNbO3 Plate"
  Base = -> Box062
  Placement = pos=(-4.76,18.63,18.3) rot=(0,0,1;-1.5708rad)
  Refine = true
  Tool = -> Cylinder023
FEATURE [Part::Box] Box063  label="Large LiNbO3 Plate006"
  AttacherType = Attacher::AttachEngine3D
  Height = 0.5
  Length = 9
  Width = 11
FEATURE [Part::Cylinder] Cylinder024
  Angle = 360
  AttacherType = Attacher::AttachEngine3D
  FirstAngle = 0
  Height = 0.01
  Placement = pos=(1,10,0.49) rot=(0,0,1;0rad)
  Radius = 0.5
  SecondAngle = 0
FEATURE [Part::Cut] Cut014  label="Large LiNbO3 Plate007"
  Base = -> Box063
  Placement = pos=(6.24,9.63,18.85) rot=(0,0,1;1.5708rad)
  Refine = true
  Tool = -> Cylinder024
FEATURE [Part::Box] Box064  label="Small Cu GND Electrode015"
  AttacherType = Attacher::AttachEngine3D
  Height = 1.15
  Length = 11.5
  Width = 11
FEATURE [Part::Box] Box065  label="Small Cu GND Electrode016"
  AttacherType = Attacher::AttachEngine3D
  Height = 1.05
  Length = 11.5
  Placement = pos=(0,0,0.05) rot=(0,0,1;0rad)
  Width = 10.95
FEATURE [Part::Cut] Cut015  label="Large Cu Electrode, Short Axis, GND"
  Base = -> Box064
  Placement = pos=(-4.76,9.63,18.25) rot=(0,0,1;0rad)
  Refine = true
  Tool = -> Box065
FEATURE [Part::Box] Box066  label="Small Cu GND Electrode017"
  AttacherType = Attacher::AttachEngine3D
  Height = 1.2
  Length = 9.5
  Width = 13
FEATURE [Part::Box] Box067  label="Small Cu GND Electrode018"
  AttacherType = Attacher::AttachEngine3D
  Height = 1.1
  Length = 9.5
  Placement = pos=(0,0,0.05) rot=(0,0,1;0rad)
  Width = 12.95
FEATURE [Part::Cut] Cut016  label="Large Cu Electrode, Long Axis, V_X"
  Base = -> Box066
  Placement = pos=(-4.76,19.13,18.8) rot=(0,0,1;-1.5708rad)
  Refine = true
  Tool = -> Box067
FEATURE [Part::Box] Box068  label="Small Cu GND Electrode019"
  AttacherType = Attacher::AttachEngine3D
  Height = 1.15
  Length = 11.5
  Width = 11
FEATURE [Part::Box] Box069  label="Small Cu GND Electrode020"
  AttacherType = Attacher::AttachEngine3D
  Height = 1.05
  Length = 11.5
  Placement = pos=(0,0,0.05) rot=(0,0,1;0rad)
  Width = 10.95
FEATURE [Part::Cut] Cut017  label="Large Cu Electrode, Short Axis, GND001"
  Base = -> Box068
  Placement = pos=(-4.76,9.63,19.4) rot=(0,0,1;0rad)
  Refine = true
  Tool = -> Box069
FEATURE [Part::Box] Box070  label="Large LiNbO3 Plate008"
  AttacherType = Attacher::AttachEngine3D
  Height = 0.5
  Length = 9
  Width = 11
FEATURE [Part::Cylinder] Cylinder025
  Angle = 360
  AttacherType = Attacher::AttachEngine3D
  FirstAngle = 0
  Height = 0.01
  Placement = pos=(1,10,0.49) rot=(0,0,1;0rad)
  Radius = 0.5
  SecondAngle = 0
FEATURE [Part::Cut] Cut018  label="Large LiNbO3 Plate009"
  Base = -> Box070
  Placement = pos=(-4.76,18.63,19.45) rot=(0,0,1;-1.5708rad)
  Refine = true
  Tool = -> Cylinder025
FEATURE [Part::Box] Box071  label="Large LiNbO3 Plate010"
  AttacherType = Attacher::AttachEngine3D
  Height = 0.5
  Length = 9
  Width = 11
FEATURE [Part::Cylinder] Cylinder026
  Angle = 360
  AttacherType = Attacher::AttachEngine3D
  FirstAngle = 0
  Height = 0.01
  Placement = pos=(1,10,0.49) rot=(0,0,1;0rad)
  Radius = 0.5
  SecondAngle = 0
FEATURE [Part::Cut] Cut019  label="Large LiNbO3 Plate011"
  Base = -> Box071
  Placement = pos=(6.24,9.63,20) rot=(0,0,1;1.5708rad)
  Refine = true
  Tool = -> Cylinder026
FEATURE [Part::Box] Box072  label="Large LiNbO3 Plate012"
  AttacherType = Attacher::AttachEngine3D
  Height = 0.5
  Length = 9
  Width = 11
FEATURE [Part::Cylinder] Cylinder027
  Angle = 360
  AttacherType = Attacher::AttachEngine3D
  FirstAngle = 0
  Height = 0.01
  Placement = pos=(1,10,0.49) rot=(0,0,1;0rad)
  Radius = 0.5
  SecondAngle = 0
FEATURE [Part::Cut] Cut020  label="Large LiNbO3 Plate013"
  Base = -> Box072
  Placement = pos=(-4.76,9.63,20.6) rot=(0,0,1;0rad)
  Refine = true
  Tool = -> Cylinder027
FEATURE [Part::Box] Box073  label="Large LiNbO3 Plate014"
  AttacherType = Attacher::AttachEngine3D
  Height = 0.5
  Length = 9
  Width = 11
FEATURE [Part::Cylinder] Cylinder028
  Angle = 360
  AttacherType = Attacher::AttachEngine3D
  FirstAngle = 0
  Height = 0.01
  Placement = pos=(1,10,0.49) rot=(0,0,1;0rad)
  Radius = 0.5
  SecondAngle = 0
FEATURE [Part::Cut] Cut021  label="Large LiNbO3 Plate015"
  Base = -> Box073
  Placement = pos=(4.24,20.63,21.15) rot=(0,0,1;3.14159rad)
  Refine = true
  Tool = -> Cylinder028
FEATURE [Part::Box] Box074  label="Large LiNbO3 Plate016"
  AttacherType = Attacher::AttachEngine3D
  Height = 0.5
  Length = 9
  Width = 11
FEATURE [Part::Cylinder] Cylinder029
  Angle = 360
  AttacherType = Attacher::AttachEngine3D
  FirstAngle = 0
  Height = 0.01
  Placement = pos=(1,10,0.49) rot=(0,0,1;0rad)
  Radius = 0.5
  SecondAngle = 0
FEATURE [Part::Cut] Cut022  label="Large LiNbO3 Plate017"
  Base = -> Box074
  Placement = pos=(-4.76,9.63,21.75) rot=(0,0,1;0rad)
  Refine = true
  Tool = -> Cylinder029
FEATURE [Part::Box] Box075  label="Large LiNbO3 Plate018"
  AttacherType = Attacher::AttachEngine3D
  Height = 0.5
  Length = 9
  Width = 11
FEATURE [Part::Cylinder] Cylinder030
  Angle = 360
  AttacherType = Attacher::AttachEngine3D
  FirstAngle = 0
  Height = 0.01
  Placement = pos=(1,10,0.49) rot=(0,0,1;0rad)
  Radius = 0.5
  SecondAngle = 0
FEATURE [Part::Cut] Cut023  label="Large LiNbO3 Plate019"
  Base = -> Box075
  Placement = pos=(4.24,20.63,22.3) rot=(0,0,1;3.14159rad)
  Refine = true
  Tool = -> Cylinder030
FEATURE [Part::Box] Box076  label="Small Cu GND Electrode021"
  AttacherType = Attacher::AttachEngine3D
  Height = 1.15
  Length = 11.5
  Width = 11
FEATURE [Part::Box] Box077  label="Small Cu GND Electrode022"
  AttacherType = Attacher::AttachEngine3D
  Height = 1.05
  Length = 11.5
  Placement = pos=(0,0,0.05) rot=(0,0,1;0rad)
  Width = 10.95
FEATURE [Part::Cut] Cut024  label="Large Cu Electrode, Short Axis, GND002"
  Base = -> Box076
  Placement = pos=(-4.76,21.13,20.55) rot=(0,0,1;-1.5708rad)
  Refine = true
  Tool = -> Box077
FEATURE [Part::Box] Box078  label="Small Cu GND Electrode023"
  AttacherType = Attacher::AttachEngine3D
  Height = 1.15
  Length = 11.5
  Width = 11
FEATURE [Part::Box] Box079  label="Small Cu GND Electrode024"
  AttacherType = Attacher::AttachEngine3D
  Height = 1.05
  Length = 11.5
  Placement = pos=(0,0,0.05) rot=(0,0,1;0rad)
  Width = 10.95
FEATURE [Part::Cut] Cut025  label="Large Cu Electrode, Short Axis, GND003"
  Base = -> Box078
  Placement = pos=(-4.76,21.13,21.7) rot=(0,0,1;-1.5708rad)
  Refine = true
  Tool = -> Box079
FEATURE [Part::Box] Box080  label="Small Cu GND Electrode025"
  AttacherType = Attacher::AttachEngine3D
  Height = 1.2
  Length = 9.5
  Width = 13
FEATURE [Part::Box] Box081  label="Small Cu GND Electrode026"
  AttacherType = Attacher::AttachEngine3D
  Height = 1.1
  Length = 9.5
  Placement = pos=(0,0,0.05) rot=(0,0,1;0rad)
  Width = 12.95
FEATURE [Part::Cut] Cut026  label="Large Cu Electrode, Long Axis, V_Y"
  Base = -> Box080
  Placement = pos=(-4.76,9.63,21.1) rot=(0,0,1;0rad)
  Refine = true
  Tool = -> Box081
FEATURE [Part::Cylinder] Cylinder031  label="KJ_D61SH001"
  Angle = 360
  AttacherType = Attacher::AttachEngine3D
  FirstAngle = 0
  Height = 1.59
  Placement = pos=(0,14.39,23.05) rot=(0,0,1;0rad)
  Radius = 4.76
  SecondAngle = 0
FEATURE [App::Point] Origin031  label="Origin039"
  Role = Origin
FEATURE [Sketcher::SketchObject] Sketch011
  ArcFitTolerance = 1e-06
  AttachmentSupport = -> [Origin030]
  ExternalTypes = [0]
  FullyConstrained = true
  MakeInternals = false
  MapMode = 5
  sketch-geometry (4):
    g0: LineSegment StartX=-7.65 StartY=-12.42 StartZ=0 EndX=-7.65 EndY=12.42 EndZ=0
    g1: LineSegment StartX=-7.65 StartY=12.42 StartZ=0 EndX=12.3 EndY=12.42 EndZ=0
    g2: LineSegment StartX=-7.65 StartY=-12.42 StartZ=0 EndX=12.3 EndY=-12.42 EndZ=0
    g3: LineSegment StartX=12.3 StartY=-12.42 StartZ=0 EndX=12.3 EndY=12.42 EndZ=0
  constraints (12):
    c: Vertical(g0)
    c: Coincident(g1,g0)
    c: Horizontal(g1)
    c: Coincident(g2,g0)
    c: Horizontal(g2)
    c: Coincident(g3,g2)
    c: Coincident(g3,g1)
    c: Vertical(g3)
    c: Distance(g-1,g1) = 12.42
    c: Distance(g-1,g2) = 12.42
    c: Distance(g-1,g0) = 7.65
    c: Distance(g-1,g3) = 12.3
FEATURE [PartDesign::Pad] Pad002
  Direction = (0,0,1)
  Length = 3
  Length2 = 10
  Profile = -> Sketch011
  ReferenceAxis = -> Sketch011 [N_Axis]
  Refine = true
  SideType = 0
  Suppressed = false
  Type = 0
  Type2 = 0
FEATURE [Sketcher::SketchObject] Sketch012
  ArcFitTolerance = 1e-06
  AttachmentSupport = -> [Origin030]
  ExternalTypes = [0]
  FullyConstrained = true
  MakeInternals = false
  MapMode = 5
  Placement = pos=(0,0,0) rot=(1,0,0;1.5708rad)
  sketch-geometry (3):
    g0: LineSegment StartX=-5.15 StartY=0.866025 StartZ=0 EndX=-6.65 EndY=0 EndZ=0
    g1: LineSegment StartX=-5.15 StartY=0.866025 StartZ=0 EndX=-3.65 EndY=0 EndZ=0
    g2: LineSegment StartX=-3.65 StartY=0 StartZ=0 EndX=-6.65 EndY=0 EndZ=0
  constraints (9):
    c: Coincident(g1,g0)
    c: Coincident(g2,g1)
    c: Coincident(g2,g0)
    c: PointOnObject(g1,g-1)
    c: PointOnObject(g0,g-1)
    c: Distance(g-1,g1) = 3.65
    c: Distance(g1,g0) = 3
    c: Equal(g0,g1)
    c: Angle(g0,g1) = 2.0944
FEATURE [PartDesign::Pocket] Pocket008
  BaseFeature = -> Pad002
  Direction = (0,1,-2e-16)
  Length = 5
  Length2 = 5
  Profile = -> Sketch012
  ReferenceAxis = -> Sketch012 [N_Axis]
  Refine = true
  SideType = 2
  Suppressed = false
  Type = 1
  Type2 = 0
FEATURE [Sketcher::SketchObject] Sketch013
  ArcFitTolerance = 1e-06
  AttachmentSupport = -> [Origin030]
  ExternalTypes = [0]
  FullyConstrained = true
  MakeInternals = false
  MapMode = 5
  Placement = pos=(0,0,0) rot=(1,0,0;1.5708rad)
  sketch-geometry (4):
    g0: LineSegment StartX=7.3 StartY=0.56 StartZ=0 EndX=7.3 EndY=0 EndZ=0
    g1: LineSegment StartX=7.3 StartY=0 StartZ=0 EndX=12.3 EndY=0 EndZ=0
    g2: LineSegment StartX=12.3 StartY=0 StartZ=0 EndX=12.3 EndY=0.56 EndZ=0
    g3: LineSegment StartX=12.3 StartY=0.56 StartZ=0 EndX=7.3 EndY=0.56 EndZ=0
  constraints (12):
    c: Coincident(g0,g1)
    c: Coincident(g1,g2)
    c: Coincident(g2,g3)
    c: Coincident(g3,g0)
    c: Vertical(g0)
    c: Vertical(g2)
    c: Horizontal(g1)
    c: Horizontal(g3)
    c: Distance(g-1,g0) = 7.3
    c: DistanceX(g3,g3) = 5
    c: PointOnObject(g0,g-1)
    c: DistanceY(g0,g0) = 0.56
FEATURE [PartDesign::Pocket] Pocket009
  BaseFeature = -> Pocket008
  Direction = (0,1,-2e-16)
  Length = 5
  Length2 = 5
  Profile = -> Sketch013
  ReferenceAxis = -> Sketch013 [N_Axis]
  Refine = true
  SideType = 2
  Suppressed = false
  Type = 1
  Type2 = 0
FEATURE [PartDesign::Body] Body002  label="Coarse Z Slider"
  AllowCompound = false
  Group = -> [Sketch011,Pad002,Sketch012,Pocket008,Sketch013,Pocket009]
  Origin = -> Origin030
  Placement = pos=(-1,5.33,42.62) rot=(1,0,0;4.71239rad)
  Tip = -> Pocket009
FEATURE [Part::Box] Box130  label="Steel Shim Spacer004"
  AttacherType = Attacher::AttachEngine3D
  Height = 0.25
  Length = 5
  Placement = pos=(-2.5,5.3e-15,47.62) rot=(1,0,0;4.71239rad)
  Width = 5
FEATURE [Part::Box] Box131  label="Steel Shim Spacer005"
  AttacherType = Attacher::AttachEngine3D
  Height = 0.25
  Length = 5
  Placement = pos=(-2.5,1.04,47.62) rot=(1,0,0;4.71239rad)
  Width = 5
FEATURE [Part::Box] Box132  label="Steel Shim Spacer006"
  AttacherType = Attacher::AttachEngine3D
  Height = 0.25
  Length = 5
  Placement = pos=(-2.5,2.08,47.62) rot=(1,0,0;4.71239rad)
  Width = 5
FEATURE [Part::Box] Box133  label="Steel Shim Spacer007"
  AttacherType = Attacher::AttachEngine3D
  Height = 0.25
  Length = 5
  Placement = pos=(-2.5,3.12,47.62) rot=(1,0,0;4.71239rad)
  Width = 5
FEATURE [Part::Box] Box134  label="Small LiNbO3 Plate052"
  AttacherType = Attacher::AttachEngine3D
  Height = 0.5
  Length = 4.5
  Width = 5.5
FEATURE [Part::Box] Box135  label="Small Cu GND Electrode051"
  AttacherType = Attacher::AttachEngine3D
  Height = 1.15
  Length = 6
  Width = 6.5
FEATURE [Part::Box] Box136  label="Small Cu GND Electrode052"
  AttacherType = Attacher::AttachEngine3D
  Height = 1.05
  Length = 6
  Placement = pos=(0,0,0.05) rot=(0,0,1;0rad)
  Width = 6.45
FEATURE [Part::Box] Box137  label="Small LiNbO3 Plate053"
  AttacherType = Attacher::AttachEngine3D
  Height = 0.5
  Length = 4.5
  Width = 5.5
FEATURE [Part::Box] Box138  label="Small Cu GND Electrode053"
  AttacherType = Attacher::AttachEngine3D
  Height = 1.2
  Length = 5
  Width = 7.5
FEATURE [Part::Box] Box139  label="Small Cu GND Electrode054"
  AttacherType = Attacher::AttachEngine3D
  Height = 1.1
  Length = 5
  Placement = pos=(0,0,0.05) rot=(0,0,1;0rad)
  Width = 7.45
FEATURE [Part::Box] Box140  label="Small Cu GND Electrode055"
  AttacherType = Attacher::AttachEngine3D
  Height = 1.15
  Length = 6
  Width = 6.5
FEATURE [Part::Box] Box141  label="Small Cu GND Electrode056"
  AttacherType = Attacher::AttachEngine3D
  Height = 1.05
  Length = 6
  Placement = pos=(0,0,0.05) rot=(0,0,1;0rad)
  Width = 6.45
FEATURE [Part::Box] Box142  label="Small LiNbO3 Plate054"
  AttacherType = Attacher::AttachEngine3D
  Height = 0.5
  Length = 4.5
  Width = 5.5
FEATURE [Part::Box] Box143  label="Small LiNbO3 Plate055"
  AttacherType = Attacher::AttachEngine3D
  Height = 0.5
  Length = 4.5
  Width = 5.5
FEATURE [Part::Box] Box144  label="Cube009"
  AttacherType = Attacher::AttachEngine3D
  Height = 10
  Length = 10
  Placement = pos=(-5,-5,-10) rot=(0,0,1;0rad)
  Width = 10
FEATURE [Part::Box] Box145  label="Small LiNbO3 Plate056"
  AttacherType = Attacher::AttachEngine3D
  Height = 0.5
  Length = 4.5
  Width = 5.5
FEATURE [Part::Box] Box146  label="Small Cu GND Electrode057"
  AttacherType = Attacher::AttachEngine3D
  Height = 1.15
  Length = 6
  Width = 6.5
FEATURE [Part::Box] Box147  label="Small Cu GND Electrode058"
  AttacherType = Attacher::AttachEngine3D
  Height = 1.05
  Length = 6
  Placement = pos=(0,0,0.05) rot=(0,0,1;0rad)
  Width = 6.45
FEATURE [Part::Box] Box148  label="Small LiNbO3 Plate057"
  AttacherType = Attacher::AttachEngine3D
  Height = 0.5
  Length = 4.5
  Width = 5.5
FEATURE [Part::Box] Box149  label="Small Cu GND Electrode059"
  AttacherType = Attacher::AttachEngine3D
  Height = 1.2
  Length = 5
  Width = 7.5
FEATURE [Part::Box] Box150  label="Small Cu GND Electrode060"
  AttacherType = Attacher::AttachEngine3D
  Height = 1.1
  Length = 5
  Placement = pos=(0,0,0.05) rot=(0,0,1;0rad)
  Width = 7.45
FEATURE [Part::Box] Box151  label="Small Cu GND Electrode061"
  AttacherType = Attacher::AttachEngine3D
  Height = 1.15
  Length = 6
  Width = 6.5
FEATURE [Part::Box] Box152  label="Small Cu GND Electrode062"
  AttacherType = Attacher::AttachEngine3D
  Height = 1.05
  Length = 6
  Placement = pos=(0,0,0.05) rot=(0,0,1;0rad)
  Width = 6.45
FEATURE [Part::Box] Box153  label="Small LiNbO3 Plate058"
  AttacherType = Attacher::AttachEngine3D
  Height = 0.5
  Length = 4.5
  Width = 5.5
FEATURE [Part::Box] Box154  label="Small LiNbO3 Plate059"
  AttacherType = Attacher::AttachEngine3D
  Height = 0.5
  Length = 4.5
  Width = 5.5
FEATURE [Part::Box] Box155  label="Cube010"
  AttacherType = Attacher::AttachEngine3D
  Height = 10
  Length = 10
  Placement = pos=(-5,-5,-10) rot=(0,0,1;0rad)
  Width = 10
FEATURE [Part::Box] Box156  label="Small LiNbO3 Plate060"
  AttacherType = Attacher::AttachEngine3D
  Height = 0.5
  Length = 4.5
  Width = 5.5
FEATURE [Part::Box] Box157  label="Small Cu GND Electrode063"
  AttacherType = Attacher::AttachEngine3D
  Height = 1.15
  Length = 6
  Width = 6.5
FEATURE [Part::Box] Box158  label="Small Cu GND Electrode064"
  AttacherType = Attacher::AttachEngine3D
  Height = 1.05
  Length = 6
  Placement = pos=(0,0,0.05) rot=(0,0,1;0rad)
  Width = 6.45
FEATURE [Part::Box] Box159  label="Small LiNbO3 Plate061"
  AttacherType = Attacher::AttachEngine3D
  Height = 0.5
  Length = 4.5
  Width = 5.5
FEATURE [Part::Box] Box160  label="Small Cu GND Electrode065"
  AttacherType = Attacher::AttachEngine3D
  Height = 1.2
  Length = 5
  Width = 7.5
FEATURE [Part::Box] Box161  label="Small Cu GND Electrode066"
  AttacherType = Attacher::AttachEngine3D
  Height = 1.1
  Length = 5
  Placement = pos=(0,0,0.05) rot=(0,0,1;0rad)
  Width = 7.45
FEATURE [Part::Box] Box162  label="Small Cu GND Electrode067"
  AttacherType = Attacher::AttachEngine3D
  Height = 1.15
  Length = 6
  Width = 6.5
FEATURE [Part::Box] Box163  label="Small Cu GND Electrode068"
  AttacherType = Attacher::AttachEngine3D
  Height = 1.05
  Length = 6
  Placement = pos=(0,0,0.05) rot=(0,0,1;0rad)
  Width = 6.45
FEATURE [Part::Box] Box164  label="Small LiNbO3 Plate062"
  AttacherType = Attacher::AttachEngine3D
  Height = 0.5
  Length = 4.5
  Width = 5.5
FEATURE [Part::Box] Box165  label="Small LiNbO3 Plate063"
  AttacherType = Attacher::AttachEngine3D
  Height = 0.5
  Length = 4.5
  Width = 5.5
FEATURE [Part::Box] Box166  label="Cube011"
  AttacherType = Attacher::AttachEngine3D
  Height = 10
  Length = 10
  Placement = pos=(-5,-5,-10) rot=(0,0,1;0rad)
  Width = 10
FEATURE [Part::Cut] Cut060  label="Small Cu Electrode, Short Axis, GND005"
  Base = -> Box135
  Placement = pos=(-6.25005,1.59,49.7089) rot=(0.364925,0.658342,0.658342;3.84141rad)
  Refine = true
  Tool = -> Box136
FEATURE [Part::Cut] Cut062  label="Small Cu Electrode001, Long Axis, V005"
  Base = -> Box138
  Placement = pos=(-9.42956,2.14,54.7971) rot=(-0.926703,-0.265728,-0.265728;1.64685rad)
  Refine = true
  Tool = -> Box139
FEATURE [Part::Cut] Cut063  label="Small Cu Electrode002, Short Axis, GND005"
  Base = -> Box140
  Placement = pos=(-6.25005,2.74,49.7089) rot=(0.364925,0.658342,0.658342;3.84141rad)
  Refine = true
  Tool = -> Box141
FEATURE [Part::Cut] Cut068  label="Small Cu Electrode, Short Axis, GND006"
  Base = -> Box146
  Placement = pos=(-6.25005,1.59,31.8689) rot=(0.364925,0.658342,0.658342;3.84141rad)
  Refine = true
  Tool = -> Box147
FEATURE [Part::Cut] Cut070  label="Small Cu Electrode001, Long Axis, V006"
  Base = -> Box149
  Placement = pos=(-9.42956,2.14,36.9571) rot=(-0.926703,-0.265728,-0.265728;1.64685rad)
  Refine = true
  Tool = -> Box150
FEATURE [Part::Cut] Cut071  label="Small Cu Electrode002, Short Axis, GND006"
  Base = -> Box151
  Placement = pos=(-6.25005,2.74,31.8689) rot=(0.364925,0.658342,0.658342;3.84141rad)
  Refine = true
  Tool = -> Box152
FEATURE [Part::Cut] Cut076  label="Small Cu Electrode, Short Axis, GND007"
  Base = -> Box157
  Placement = pos=(9.19995,1.59,40.7889) rot=(0.364925,0.658342,0.658342;3.84141rad)
  Refine = true
  Tool = -> Box158
FEATURE [Part::Cut] Cut078  label="Small Cu Electrode001, Long Axis, V007"
  Base = -> Box160
  Placement = pos=(6.02044,2.14,45.8771) rot=(-0.926703,-0.265728,-0.265728;1.64685rad)
  Refine = true
  Tool = -> Box161
FEATURE [Part::Cut] Cut079  label="Small Cu Electrode002, Short Axis, GND007"
  Base = -> Box162
  Placement = pos=(9.19995,2.74,40.7889) rot=(0.364925,0.658342,0.658342;3.84141rad)
  Refine = true
  Tool = -> Box163
FEATURE [Part::Cylinder] Cylinder056  label="KJ_D401_005"
  Angle = 360
  AttacherType = Attacher::AttachEngine3D
  FirstAngle = 0
  Height = 0.79
  Placement = pos=(0,0.25,45.12) rot=(1,0,0;4.71239rad)
  Radius = 3.18
  SecondAngle = 0
FEATURE [Part::Cylinder] Cylinder057  label="KJ_D401_006"
  Angle = 360
  AttacherType = Attacher::AttachEngine3D
  FirstAngle = 0
  Height = 0.79
  Placement = pos=(0,1.29,45.12) rot=(1,0,0;4.71239rad)
  Radius = 3.18
  SecondAngle = 0
FEATURE [Part::Cylinder] Cylinder058  label="KJ_D401_007"
  Angle = 360
  AttacherType = Attacher::AttachEngine3D
  FirstAngle = 0
  Height = 0.79
  Placement = pos=(0,2.33,45.12) rot=(1,0,0;4.71239rad)
  Radius = 3.18
  SecondAngle = 0
FEATURE [Part::Cylinder] Cylinder059  label="KJ_D401_008"
  Angle = 360
  AttacherType = Attacher::AttachEngine3D
  FirstAngle = 0
  Height = 0.79
  Placement = pos=(0,3.37,45.12) rot=(1,0,0;4.71239rad)
  Radius = 3.18
  SecondAngle = 0
FEATURE [Part::Cylinder] Cylinder060  label="KJ_D31SH005"
  Angle = 360
  AttacherType = Attacher::AttachEngine3D
  FirstAngle = 0
  Height = 1.59
  Placement = pos=(-6.15,7.1e-15,54.04) rot=(-0.926703,-0.265728,-0.265728;1.64685rad)
  Radius = 2.38
  SecondAngle = 0
FEATURE [Part::Cylinder] Cylinder061
  Angle = 360
  AttacherType = Attacher::AttachEngine3D
  FirstAngle = 0
  Height = 0.01
  Placement = pos=(1,4.5,0.49) rot=(0,0,1;0rad)
  Radius = 0.5
  SecondAngle = 0
FEATURE [Part::Cut] Cut059  label="Small LiNbO3 Plate064"
  Base = -> Box134
  Placement = pos=(-9.42956,1.64,54.7971) rot=(-0.926703,-0.265728,-0.265728;1.64685rad)
  Refine = true
  Tool = -> Cylinder061
FEATURE [Part::Cylinder] Cylinder062
  Angle = 360
  AttacherType = Attacher::AttachEngine3D
  FirstAngle = 0
  Height = 0.01
  Placement = pos=(1,4.5,0.49) rot=(0,0,1;0rad)
  Radius = 0.5
  SecondAngle = 0
FEATURE [Part::Cut] Cut061  label="Small LiNbO3 Plate065"
  Base = -> Box137
  Placement = pos=(-2.69879,2.19,52.5175) rot=(-0.198716,0.693005,0.693005;2.74927rad)
  Refine = true
  Tool = -> Cylinder062
FEATURE [Part::Cylinder] Cylinder063
  Angle = 360
  AttacherType = Attacher::AttachEngine3D
  FirstAngle = 0
  Height = 0.01
  Placement = pos=(1,4.5,0.49) rot=(0,0,1;0rad)
  Radius = 0.5
  SecondAngle = 0
FEATURE [Part::Cut] Cut064  label="Small LiNbO3 Plate066"
  Base = -> Box142
  Placement = pos=(-9.42956,2.79,54.7971) rot=(-0.926703,-0.265728,-0.265728;1.64685rad)
  Refine = true
  Tool = -> Cylinder063
FEATURE [Part::Cylinder] Cylinder064
  Angle = 360
  AttacherType = Attacher::AttachEngine3D
  FirstAngle = 0
  Height = 0.01
  Placement = pos=(1,4.5,0.49) rot=(0,0,1;0rad)
  Radius = 0.5
  SecondAngle = 0
FEATURE [Part::Cut] Cut065  label="Small LiNbO3 Plate067"
  Base = -> Box143
  Placement = pos=(-2.69879,3.34,52.5175) rot=(-0.198716,0.693005,0.693005;2.74927rad)
  Refine = true
  Tool = -> Cylinder064
FEATURE [Part::Cylinder] Cylinder065  label="KJ_D31SH006"
  Angle = 360
  AttacherType = Attacher::AttachEngine3D
  FirstAngle = 0
  Height = 1.59
  Placement = pos=(-6.15,1.8e-15,36.2) rot=(-0.926703,-0.265728,-0.265728;1.64685rad)
  Radius = 2.38
  SecondAngle = 0
FEATURE [Part::Cylinder] Cylinder066
  Angle = 360
  AttacherType = Attacher::AttachEngine3D
  FirstAngle = 0
  Height = 0.01
  Placement = pos=(1,4.5,0.49) rot=(0,0,1;0rad)
  Radius = 0.5
  SecondAngle = 0
FEATURE [Part::Cut] Cut067  label="Small LiNbO3 Plate068"
  Base = -> Box145
  Placement = pos=(-9.42956,1.64,36.9571) rot=(-0.926703,-0.265728,-0.265728;1.64685rad)
  Refine = true
  Tool = -> Cylinder066
FEATURE [Part::Cylinder] Cylinder067
  Angle = 360
  AttacherType = Attacher::AttachEngine3D
  FirstAngle = 0
  Height = 0.01
  Placement = pos=(1,4.5,0.49) rot=(0,0,1;0rad)
  Radius = 0.5
  SecondAngle = 0
FEATURE [Part::Cut] Cut069  label="Small LiNbO3 Plate069"
  Base = -> Box148
  Placement = pos=(-2.69879,2.19,34.6775) rot=(-0.198716,0.693005,0.693005;2.74927rad)
  Refine = true
  Tool = -> Cylinder067
FEATURE [Part::Cylinder] Cylinder068
  Angle = 360
  AttacherType = Attacher::AttachEngine3D
  FirstAngle = 0
  Height = 0.01
  Placement = pos=(1,4.5,0.49) rot=(0,0,1;0rad)
  Radius = 0.5
  SecondAngle = 0
FEATURE [Part::Cut] Cut072  label="Small LiNbO3 Plate070"
  Base = -> Box153
  Placement = pos=(-9.42956,2.79,36.9571) rot=(-0.926703,-0.265728,-0.265728;1.64685rad)
  Refine = true
  Tool = -> Cylinder068
FEATURE [Part::Cylinder] Cylinder069
  Angle = 360
  AttacherType = Attacher::AttachEngine3D
  FirstAngle = 0
  Height = 0.01
  Placement = pos=(1,4.5,0.49) rot=(0,0,1;0rad)
  Radius = 0.5
  SecondAngle = 0
FEATURE [Part::Cut] Cut073  label="Small LiNbO3 Plate071"
  Base = -> Box154
  Placement = pos=(-2.69879,3.34,34.6775) rot=(-0.198716,0.693005,0.693005;2.74927rad)
  Refine = true
  Tool = -> Cylinder069
FEATURE [Part::Cylinder] Cylinder070  label="KJ_D31SH007"
  Angle = 360
  AttacherType = Attacher::AttachEngine3D
  FirstAngle = 0
  Height = 1.59
  Placement = pos=(9.3,3.6e-15,45.12) rot=(-0.926703,-0.265728,-0.265728;1.64685rad)
  Radius = 2.38
  SecondAngle = 0
FEATURE [Part::Cylinder] Cylinder071
  Angle = 360
  AttacherType = Attacher::AttachEngine3D
  FirstAngle = 0
  Height = 0.01
  Placement = pos=(1,4.5,0.49) rot=(0,0,1;0rad)
  Radius = 0.5
  SecondAngle = 0
FEATURE [Part::Cut] Cut075  label="Small LiNbO3 Plate072"
  Base = -> Box156
  Placement = pos=(6.02044,1.64,45.8771) rot=(-0.926703,-0.265728,-0.265728;1.64685rad)
  Refine = true
  Tool = -> Cylinder071
FEATURE [Part::Cylinder] Cylinder072
  Angle = 360
  AttacherType = Attacher::AttachEngine3D
  FirstAngle = 0
  Height = 0.01
  Placement = pos=(1,4.5,0.49) rot=(0,0,1;0rad)
  Radius = 0.5
  SecondAngle = 0
FEATURE [Part::Cut] Cut077  label="Small LiNbO3 Plate073"
  Base = -> Box159
  Placement = pos=(12.7512,2.19,43.5975) rot=(-0.198716,0.693005,0.693005;2.74927rad)
  Refine = true
  Tool = -> Cylinder072
FEATURE [Part::Cylinder] Cylinder073
  Angle = 360
  AttacherType = Attacher::AttachEngine3D
  FirstAngle = 0
  Height = 0.01
  Placement = pos=(1,4.5,0.49) rot=(0,0,1;0rad)
  Radius = 0.5
  SecondAngle = 0
FEATURE [Part::Cut] Cut080  label="Small LiNbO3 Plate074"
  Base = -> Box164
  Placement = pos=(6.02044,2.79,45.8771) rot=(-0.926703,-0.265728,-0.265728;1.64685rad)
  Refine = true
  Tool = -> Cylinder073
FEATURE [Part::Cylinder] Cylinder074
  Angle = 360
  AttacherType = Attacher::AttachEngine3D
  FirstAngle = 0
  Height = 0.01
  Placement = pos=(1,4.5,0.49) rot=(0,0,1;0rad)
  Radius = 0.5
  SecondAngle = 0
FEATURE [Part::Cut] Cut081  label="Small LiNbO3 Plate075"
  Base = -> Box165
  Placement = pos=(12.7512,3.34,43.5975) rot=(-0.198716,0.693005,0.693005;2.74927rad)
  Refine = true
  Tool = -> Cylinder074
FEATURE [App::DocumentObjectGroup] Group015  label="Magnet Stack001"
  Group = -> [Box130,Cylinder056,Box131,Cylinder057,Box132,Cylinder058,Box133,Cylinder059]
FEATURE [Part::Sphere] Sphere009
  Angle1 = -90
  Angle2 = 90
  Angle3 = 360
  AttacherType = Attacher::AttachEngine3D
  Radius = 2
FEATURE [Part::Cut] Cut066  label="Sapphire Half-Ball Lens009"
  Base = -> Sphere009
  Placement = pos=(-6.15,3.89,54.04) rot=(-0.926703,-0.265728,-0.265728;1.64685rad)
  Refine = true
  Tool = -> Box144
FEATURE [App::DocumentObjectGroup] Group016  label="Coarse Piezo Stack, Rotated004"
  Group = -> [Cylinder060,Cut060,Cut059,Cut062,Cut061,Cut063,Cut064,Cut065,Cut066]
FEATURE [Part::Sphere] Sphere010
  Angle1 = -90
  Angle2 = 90
  Angle3 = 360
  AttacherType = Attacher::AttachEngine3D
  Radius = 2
FEATURE [Part::Cut] Cut074  label="Sapphire Half-Ball Lens010"
  Base = -> Sphere010
  Placement = pos=(-6.15,3.89,36.2) rot=(-0.926703,-0.265728,-0.265728;1.64685rad)
  Refine = true
  Tool = -> Box155
FEATURE [App::DocumentObjectGroup] Group017  label="Coarse Piezo Stack, Rotated005"
  Group = -> [Cylinder065,Cut068,Cut067,Cut070,Cut069,Cut071,Cut072,Cut073,Cut074]
FEATURE [Part::Sphere] Sphere011
  Angle1 = -90
  Angle2 = 90
  Angle3 = 360
  AttacherType = Attacher::AttachEngine3D
  Radius = 2
FEATURE [Part::Cut] Cut082  label="Sapphire Half-Ball Lens011"
  Base = -> Sphere011
  Placement = pos=(9.3,3.89,45.12) rot=(-0.926703,-0.265728,-0.265728;1.64685rad)
  Refine = true
  Tool = -> Box166
FEATURE [App::DocumentObjectGroup] Group018  label="Coarse Piezo Stack, Rotated006"
  Group = -> [Cylinder070,Cut076,Cut075,Cut078,Cut077,Cut079,Cut080,Cut081,Cut082]
FEATURE [App::DocumentObjectGroup] Group019  label="Coarse Z Piezo Tripod"
  Group = -> [Group016,Group017,Group018,Group015]
FEATURE [Part::Box] Box167  label="Steel Shim Spacer008"
  AttacherType = Attacher::AttachEngine3D
  Height = 0.25
  Length = 5
  Placement = pos=(-2.5,15.89,0) rot=(0,0,1;4.71239rad)
  Width = 5
FEATURE [Part::Box] Box168  label="Steel Shim Spacer009"
  AttacherType = Attacher::AttachEngine3D
  Height = 0.25
  Length = 5
  Placement = pos=(-2.5,15.89,1.04) rot=(0,0,1;4.71239rad)
  Width = 5
FEATURE [Part::Box] Box169  label="Steel Shim Spacer010"
  AttacherType = Attacher::AttachEngine3D
  Height = 0.25
  Length = 5
  Placement = pos=(-2.5,15.89,2.08) rot=(0,0,1;4.71239rad)
  Width = 5
FEATURE [Part::Box] Box170  label="Steel Shim Spacer011"
  AttacherType = Attacher::AttachEngine3D
  Height = 0.25
  Length = 5
  Placement = pos=(-2.5,15.89,3.12) rot=(0,0,1;4.71239rad)
  Width = 5
FEATURE [Part::Box] Box171  label="Small LiNbO3 Plate076"
  AttacherType = Attacher::AttachEngine3D
  Height = 0.5
  Length = 4.5
  Width = 5.5
FEATURE [Part::Box] Box172  label="Small Cu GND Electrode069"
  AttacherType = Attacher::AttachEngine3D
  Height = 1.15
  Length = 6
  Width = 6.5
FEATURE [Part::Box] Box173  label="Small Cu GND Electrode070"
  AttacherType = Attacher::AttachEngine3D
  Height = 1.05
  Length = 6
  Placement = pos=(0,0,0.05) rot=(0,0,1;0rad)
  Width = 6.45
FEATURE [Part::Box] Box174  label="Small LiNbO3 Plate077"
  AttacherType = Attacher::AttachEngine3D
  Height = 0.5
  Length = 4.5
  Width = 5.5
FEATURE [Part::Box] Box175  label="Small Cu GND Electrode071"
  AttacherType = Attacher::AttachEngine3D
  Height = 1.2
  Length = 5
  Width = 7.5
FEATURE [Part::Box] Box176  label="Small Cu GND Electrode072"
  AttacherType = Attacher::AttachEngine3D
  Height = 1.1
  Length = 5
  Placement = pos=(0,0,0.05) rot=(0,0,1;0rad)
  Width = 7.45
FEATURE [Part::Box] Box177  label="Small Cu GND Electrode073"
  AttacherType = Attacher::AttachEngine3D
  Height = 1.15
  Length = 6
  Width = 6.5
FEATURE [Part::Box] Box178  label="Small Cu GND Electrode074"
  AttacherType = Attacher::AttachEngine3D
  Height = 1.05
  Length = 6
  Placement = pos=(0,0,0.05) rot=(0,0,1;0rad)
  Width = 6.45
FEATURE [Part::Box] Box179  label="Small LiNbO3 Plate078"
  AttacherType = Attacher::AttachEngine3D
  Height = 0.5
  Length = 4.5
  Width = 5.5
FEATURE [Part::Box] Box180  label="Small LiNbO3 Plate079"
  AttacherType = Attacher::AttachEngine3D
  Height = 0.5
  Length = 4.5
  Width = 5.5
FEATURE [Part::Box] Box181  label="Cube012"
  AttacherType = Attacher::AttachEngine3D
  Height = 10
  Length = 10
  Placement = pos=(-5,-5,-10) rot=(0,0,1;0rad)
  Width = 10
FEATURE [Part::Box] Box182  label="Small LiNbO3 Plate080"
  AttacherType = Attacher::AttachEngine3D
  Height = 0.5
  Length = 4.5
  Width = 5.5
FEATURE [Part::Box] Box183  label="Small Cu GND Electrode075"
  AttacherType = Attacher::AttachEngine3D
  Height = 1.15
  Length = 6
  Width = 6.5
FEATURE [Part::Box] Box184  label="Small Cu GND Electrode076"
  AttacherType = Attacher::AttachEngine3D
  Height = 1.05
  Length = 6
  Placement = pos=(0,0,0.05) rot=(0,0,1;0rad)
  Width = 6.45
FEATURE [Part::Box] Box185  label="Small LiNbO3 Plate081"
  AttacherType = Attacher::AttachEngine3D
  Height = 0.5
  Length = 4.5
  Width = 5.5
FEATURE [Part::Box] Box186  label="Small Cu GND Electrode077"
  AttacherType = Attacher::AttachEngine3D
  Height = 1.2
  Length = 5
  Width = 7.5
FEATURE [Part::Box] Box187  label="Small Cu GND Electrode078"
  AttacherType = Attacher::AttachEngine3D
  Height = 1.1
  Length = 5
  Placement = pos=(0,0,0.05) rot=(0,0,1;0rad)
  Width = 7.45
FEATURE [Part::Box] Box188  label="Small Cu GND Electrode079"
  AttacherType = Attacher::AttachEngine3D
  Height = 1.15
  Length = 6
  Width = 6.5
FEATURE [Part::Box] Box189  label="Small Cu GND Electrode080"
  AttacherType = Attacher::AttachEngine3D
  Height = 1.05
  Length = 6
  Placement = pos=(0,0,0.05) rot=(0,0,1;0rad)
  Width = 6.45
FEATURE [Part::Box] Box190  label="Small LiNbO3 Plate082"
  AttacherType = Attacher::AttachEngine3D
  Height = 0.5
  Length = 4.5
  Width = 5.5
FEATURE [Part::Box] Box191  label="Small LiNbO3 Plate083"
  AttacherType = Attacher::AttachEngine3D
  Height = 0.5
  Length = 4.5
  Width = 5.5
FEATURE [Part::Box] Box192  label="Cube013"
  AttacherType = Attacher::AttachEngine3D
  Height = 10
  Length = 10
  Placement = pos=(-5,-5,-10) rot=(0,0,1;0rad)
  Width = 10
FEATURE [Part::Box] Box193  label="Small LiNbO3 Plate084"
  AttacherType = Attacher::AttachEngine3D
  Height = 0.5
  Length = 4.5
  Width = 5.5
FEATURE [Part::Box] Box194  label="Small Cu GND Electrode081"
  AttacherType = Attacher::AttachEngine3D
  Height = 1.15
  Length = 6
  Width = 6.5
FEATURE [Part::Box] Box195  label="Small Cu GND Electrode082"
  AttacherType = Attacher::AttachEngine3D
  Height = 1.05
  Length = 6
  Placement = pos=(0,0,0.05) rot=(0,0,1;0rad)
  Width = 6.45
FEATURE [Part::Box] Box196  label="Small LiNbO3 Plate085"
  AttacherType = Attacher::AttachEngine3D
  Height = 0.5
  Length = 4.5
  Width = 5.5
FEATURE [Part::Box] Box197  label="Small Cu GND Electrode083"
  AttacherType = Attacher::AttachEngine3D
  Height = 1.2
  Length = 5
  Width = 7.5
FEATURE [Part::Box] Box198  label="Small Cu GND Electrode084"
  AttacherType = Attacher::AttachEngine3D
  Height = 1.1
  Length = 5
  Placement = pos=(0,0,0.05) rot=(0,0,1;0rad)
  Width = 7.45
FEATURE [Part::Box] Box199  label="Small Cu GND Electrode085"
  AttacherType = Attacher::AttachEngine3D
  Height = 1.15
  Length = 6
  Width = 6.5
FEATURE [Part::Box] Box200  label="Small Cu GND Electrode086"
  AttacherType = Attacher::AttachEngine3D
  Height = 1.05
  Length = 6
  Placement = pos=(0,0,0.05) rot=(0,0,1;0rad)
  Width = 6.45
FEATURE [Part::Box] Box201  label="Small LiNbO3 Plate086"
  AttacherType = Attacher::AttachEngine3D
  Height = 0.5
  Length = 4.5
  Width = 5.5
FEATURE [Part::Box] Box202  label="Small LiNbO3 Plate087"
  AttacherType = Attacher::AttachEngine3D
  Height = 0.5
  Length = 4.5
  Width = 5.5
FEATURE [Part::Box] Box203  label="Cube014"
  AttacherType = Attacher::AttachEngine3D
  Height = 10
  Length = 10
  Placement = pos=(-5,-5,-10) rot=(0,0,1;0rad)
  Width = 10
FEATURE [Part::Cut] Cut084  label="Small Cu Electrode, Short Axis, GND008"
  Base = -> Box172
  Placement = pos=(-4.58886,19.64,1.59) rot=(0,0,1;2.58309rad)
  Refine = true
  Tool = -> Box173
FEATURE [Part::Cut] Cut086  label="Small Cu Electrode001, Long Axis, V008"
  Base = -> Box175
  Placement = pos=(-9.67715,22.8196,2.14) rot=(0,0,-1;2.1293rad)
  Refine = true
  Tool = -> Box176
FEATURE [Part::Cut] Cut087  label="Small Cu Electrode002, Short Axis, GND008"
  Base = -> Box177
  Placement = pos=(-4.58886,19.64,2.74) rot=(0,0,1;2.58309rad)
  Refine = true
  Tool = -> Box178
FEATURE [Part::Cut] Cut092  label="Small Cu Electrode, Short Axis, GND009"
  Base = -> Box183
  Placement = pos=(13.2511,19.64,1.59) rot=(0,0,1;2.58309rad)
  Refine = true
  Tool = -> Box184
FEATURE [Part::Cut] Cut094  label="Small Cu Electrode001, Long Axis, V009"
  Base = -> Box186
  Placement = pos=(8.16285,22.8196,2.14) rot=(0,0,-1;2.1293rad)
  Refine = true
  Tool = -> Box187
FEATURE [Part::Cut] Cut095  label="Small Cu Electrode002, Short Axis, GND009"
  Base = -> Box188
  Placement = pos=(13.2511,19.64,2.74) rot=(0,0,1;2.58309rad)
  Refine = true
  Tool = -> Box189
FEATURE [Part::Cut] Cut100  label="Small Cu Electrode, Short Axis, GND010"
  Base = -> Box194
  Placement = pos=(4.33114,4.19005,1.59) rot=(0,0,1;2.58309rad)
  Refine = true
  Tool = -> Box195
FEATURE [Part::Cut] Cut102  label="Small Cu Electrode001, Long Axis, V010"
  Base = -> Box197
  Placement = pos=(-0.757147,7.36956,2.14) rot=(0,0,-1;2.1293rad)
  Refine = true
  Tool = -> Box198
FEATURE [Part::Cut] Cut103  label="Small Cu Electrode002, Short Axis, GND010"
  Base = -> Box199
  Placement = pos=(4.33114,4.19005,2.74) rot=(0,0,1;2.58309rad)
  Refine = true
  Tool = -> Box200
FEATURE [Part::Cylinder] Cylinder075  label="KJ_D401_009"
  Angle = 360
  AttacherType = Attacher::AttachEngine3D
  FirstAngle = 0
  Height = 0.79
  Placement = pos=(-2e-16,13.39,0.25) rot=(0,0,1;4.71239rad)
  Radius = 3.18
  SecondAngle = 0
FEATURE [Part::Cylinder] Cylinder076  label="KJ_D401_010"
  Angle = 360
  AttacherType = Attacher::AttachEngine3D
  FirstAngle = 0
  Height = 0.79
  Placement = pos=(-2e-16,13.39,1.29) rot=(0,0,1;4.71239rad)
  Radius = 3.18
  SecondAngle = 0
FEATURE [Part::Cylinder] Cylinder077  label="KJ_D401_011"
  Angle = 360
  AttacherType = Attacher::AttachEngine3D
  FirstAngle = 0
  Height = 0.79
  Placement = pos=(-2e-16,13.39,2.33) rot=(0,0,1;4.71239rad)
  Radius = 3.18
  SecondAngle = 0
FEATURE [Part::Cylinder] Cylinder078  label="KJ_D401_012"
  Angle = 360
  AttacherType = Attacher::AttachEngine3D
  FirstAngle = 0
  Height = 0.79
  Placement = pos=(-2e-16,13.39,3.37) rot=(0,0,1;4.71239rad)
  Radius = 3.18
  SecondAngle = 0
FEATURE [Part::Cylinder] Cylinder079  label="KJ_D31SH008"
  Angle = 360
  AttacherType = Attacher::AttachEngine3D
  FirstAngle = 0
  Height = 1.59
  Placement = pos=(-8.92,19.54,0) rot=(0,0,-1;2.1293rad)
  Radius = 2.38
  SecondAngle = 0
FEATURE [Part::Cylinder] Cylinder080
  Angle = 360
  AttacherType = Attacher::AttachEngine3D
  FirstAngle = 0
  Height = 0.01
  Placement = pos=(1,4.5,0.49) rot=(0,0,1;0rad)
  Radius = 0.5
  SecondAngle = 0
FEATURE [Part::Cut] Cut083  label="Small LiNbO3 Plate088"
  Base = -> Box171
  Placement = pos=(-9.67715,22.8196,1.64) rot=(0,0,-1;2.1293rad)
  Refine = true
  Tool = -> Cylinder080
FEATURE [Part::Cylinder] Cylinder081
  Angle = 360
  AttacherType = Attacher::AttachEngine3D
  FirstAngle = 0
  Height = 0.01
  Placement = pos=(1,4.5,0.49) rot=(0,0,1;0rad)
  Radius = 0.5
  SecondAngle = 0
FEATURE [Part::Cut] Cut085  label="Small LiNbO3 Plate089"
  Base = -> Box174
  Placement = pos=(-7.39752,16.0888,2.19) rot=(0,0,1;1.01229rad)
  Refine = true
  Tool = -> Cylinder081
FEATURE [Part::Cylinder] Cylinder082
  Angle = 360
  AttacherType = Attacher::AttachEngine3D
  FirstAngle = 0
  Height = 0.01
  Placement = pos=(1,4.5,0.49) rot=(0,0,1;0rad)
  Radius = 0.5
  SecondAngle = 0
FEATURE [Part::Cut] Cut088  label="Small LiNbO3 Plate090"
  Base = -> Box179
  Placement = pos=(-9.67715,22.8196,2.79) rot=(0,0,-1;2.1293rad)
  Refine = true
  Tool = -> Cylinder082
FEATURE [Part::Cylinder] Cylinder083
  Angle = 360
  AttacherType = Attacher::AttachEngine3D
  FirstAngle = 0
  Height = 0.01
  Placement = pos=(1,4.5,0.49) rot=(0,0,1;0rad)
  Radius = 0.5
  SecondAngle = 0
FEATURE [Part::Cut] Cut089  label="Small LiNbO3 Plate091"
  Base = -> Box180
  Placement = pos=(-7.39752,16.0888,3.34) rot=(0,0,1;1.01229rad)
  Refine = true
  Tool = -> Cylinder083
FEATURE [Part::Cylinder] Cylinder084  label="KJ_D31SH009"
  Angle = 360
  AttacherType = Attacher::AttachEngine3D
  FirstAngle = 0
  Height = 1.59
  Placement = pos=(8.92,19.54,0) rot=(0,0,-1;2.1293rad)
  Radius = 2.38
  SecondAngle = 0
FEATURE [Part::Cylinder] Cylinder085
  Angle = 360
  AttacherType = Attacher::AttachEngine3D
  FirstAngle = 0
  Height = 0.01
  Placement = pos=(1,4.5,0.49) rot=(0,0,1;0rad)
  Radius = 0.5
  SecondAngle = 0
FEATURE [Part::Cut] Cut091  label="Small LiNbO3 Plate092"
  Base = -> Box182
  Placement = pos=(8.16285,22.8196,1.64) rot=(0,0,-1;2.1293rad)
  Refine = true
  Tool = -> Cylinder085
FEATURE [Part::Cylinder] Cylinder086
  Angle = 360
  AttacherType = Attacher::AttachEngine3D
  FirstAngle = 0
  Height = 0.01
  Placement = pos=(1,4.5,0.49) rot=(0,0,1;0rad)
  Radius = 0.5
  SecondAngle = 0
FEATURE [Part::Cut] Cut093  label="Small LiNbO3 Plate093"
  Base = -> Box185
  Placement = pos=(10.4425,16.0888,2.19) rot=(0,0,1;1.01229rad)
  Refine = true
  Tool = -> Cylinder086
FEATURE [Part::Cylinder] Cylinder087
  Angle = 360
  AttacherType = Attacher::AttachEngine3D
  FirstAngle = 0
  Height = 0.01
  Placement = pos=(1,4.5,0.49) rot=(0,0,1;0rad)
  Radius = 0.5
  SecondAngle = 0
FEATURE [Part::Cut] Cut096  label="Small LiNbO3 Plate094"
  Base = -> Box190
  Placement = pos=(8.16285,22.8196,2.79) rot=(0,0,-1;2.1293rad)
  Refine = true
  Tool = -> Cylinder087
FEATURE [Part::Cylinder] Cylinder088
  Angle = 360
  AttacherType = Attacher::AttachEngine3D
  FirstAngle = 0
  Height = 0.01
  Placement = pos=(1,4.5,0.49) rot=(0,0,1;0rad)
  Radius = 0.5
  SecondAngle = 0
FEATURE [Part::Cut] Cut097  label="Small LiNbO3 Plate095"
  Base = -> Box191
  Placement = pos=(10.4425,16.0888,3.34) rot=(0,0,1;1.01229rad)
  Refine = true
  Tool = -> Cylinder088
FEATURE [Part::Cylinder] Cylinder089  label="KJ_D31SH010"
  Angle = 360
  AttacherType = Attacher::AttachEngine3D
  FirstAngle = 0
  Height = 1.59
  Placement = pos=(-2.3e-15,4.09,0) rot=(0,0,-1;2.1293rad)
  Radius = 2.38
  SecondAngle = 0
FEATURE [Part::Cylinder] Cylinder090
  Angle = 360
  AttacherType = Attacher::AttachEngine3D
  FirstAngle = 0
  Height = 0.01
  Placement = pos=(1,4.5,0.49) rot=(0,0,1;0rad)
  Radius = 0.5
  SecondAngle = 0
FEATURE [Part::Cut] Cut099  label="Small LiNbO3 Plate096"
  Base = -> Box193
  Placement = pos=(-0.757147,7.36956,1.64) rot=(0,0,-1;2.1293rad)
  Refine = true
  Tool = -> Cylinder090
FEATURE [Part::Cylinder] Cylinder091
  Angle = 360
  AttacherType = Attacher::AttachEngine3D
  FirstAngle = 0
  Height = 0.01
  Placement = pos=(1,4.5,0.49) rot=(0,0,1;0rad)
  Radius = 0.5
  SecondAngle = 0
FEATURE [Part::Cut] Cut101  label="Small LiNbO3 Plate097"
  Base = -> Box196
  Placement = pos=(1.52248,0.63879,2.19) rot=(0,0,1;1.01229rad)
  Refine = true
  Tool = -> Cylinder091
FEATURE [Part::Cylinder] Cylinder092
  Angle = 360
  AttacherType = Attacher::AttachEngine3D
  FirstAngle = 0
  Height = 0.01
  Placement = pos=(1,4.5,0.49) rot=(0,0,1;0rad)
  Radius = 0.5
  SecondAngle = 0
FEATURE [Part::Cut] Cut104  label="Small LiNbO3 Plate098"
  Base = -> Box201
  Placement = pos=(-0.757147,7.36956,2.79) rot=(0,0,-1;2.1293rad)
  Refine = true
  Tool = -> Cylinder092
FEATURE [Part::Cylinder] Cylinder093
  Angle = 360
  AttacherType = Attacher::AttachEngine3D
  FirstAngle = 0
  Height = 0.01
  Placement = pos=(1,4.5,0.49) rot=(0,0,1;0rad)
  Radius = 0.5
  SecondAngle = 0
FEATURE [Part::Cut] Cut105  label="Small LiNbO3 Plate099"
  Base = -> Box202
  Placement = pos=(1.52248,0.63879,3.34) rot=(0,0,1;1.01229rad)
  Refine = true
  Tool = -> Cylinder093
FEATURE [App::DocumentObjectGroup] Group020  label="Magnet Stack002"
  Group = -> [Box167,Cylinder075,Box168,Cylinder076,Box169,Cylinder077,Box170,Cylinder078]
FEATURE [Part::Sphere] Sphere012
  Angle1 = -90
  Angle2 = 90
  Angle3 = 360
  AttacherType = Attacher::AttachEngine3D
  Radius = 2
FEATURE [Part::Cut] Cut090  label="Sapphire Half-Ball Lens012"
  Base = -> Sphere012
  Placement = pos=(-8.92,19.54,3.89) rot=(0,0,-1;2.1293rad)
  Refine = true
  Tool = -> Box181
FEATURE [App::DocumentObjectGroup] Group021  label="Coarse Piezo Stack, Rotated007"
  Group = -> [Cylinder079,Cut084,Cut083,Cut086,Cut085,Cut087,Cut088,Cut089,Cut090]
FEATURE [Part::Sphere] Sphere013
  Angle1 = -90
  Angle2 = 90
  Angle3 = 360
  AttacherType = Attacher::AttachEngine3D
  Radius = 2
FEATURE [Part::Cut] Cut098  label="Sapphire Half-Ball Lens013"
  Base = -> Sphere013
  Placement = pos=(8.92,19.54,3.89) rot=(0,0,-1;2.1293rad)
  Refine = true
  Tool = -> Box192
FEATURE [App::DocumentObjectGroup] Group022  label="Coarse Piezo Stack, Rotated008"
  Group = -> [Cylinder084,Cut092,Cut091,Cut094,Cut093,Cut095,Cut096,Cut097,Cut098]
FEATURE [Part::Sphere] Sphere014
  Angle1 = -90
  Angle2 = 90
  Angle3 = 360
  AttacherType = Attacher::AttachEngine3D
  Radius = 2
FEATURE [Part::Cut] Cut106  label="Sapphire Half-Ball Lens014"
  Base = -> Sphere014
  Placement = pos=(-2.3e-15,4.09,3.89) rot=(0,0,-1;2.1293rad)
  Refine = true
  Tool = -> Box203
FEATURE [App::DocumentObjectGroup] Group023  label="Coarse Piezo Stack, Rotated009"
  Group = -> [Cylinder089,Cut100,Cut099,Cut102,Cut101,Cut103,Cut104,Cut105,Cut106]
FEATURE [App::DocumentObjectGroup] Group024  label="Coarse X Piezo Tripod"
  Group = -> [Group021,Group022,Group023,Group020]
FEATURE [Part::Box] Box204  label="Steel Shim Spacer012"
  AttacherType = Attacher::AttachEngine3D
  Height = 0.25
  Length = 5
  Placement = pos=(-1.5,11.89,8.33) rot=(0,0,1;0rad)
  Width = 5
FEATURE [Part::Box] Box205  label="Steel Shim Spacer013"
  AttacherType = Attacher::AttachEngine3D
  Height = 0.25
  Length = 5
  Placement = pos=(-1.5,11.89,9.37) rot=(0,0,1;0rad)
  Width = 5
FEATURE [Part::Box] Box206  label="Steel Shim Spacer014"
  AttacherType = Attacher::AttachEngine3D
  Height = 0.25
  Length = 5
  Placement = pos=(-1.5,11.89,10.41) rot=(0,0,1;0rad)
  Width = 5
FEATURE [Part::Box] Box207  label="Steel Shim Spacer015"
  AttacherType = Attacher::AttachEngine3D
  Height = 0.25
  Length = 5
  Placement = pos=(-1.5,11.89,11.45) rot=(0,0,1;0rad)
  Width = 5
FEATURE [Part::Box] Box208  label="Small LiNbO3 Plate100"
  AttacherType = Attacher::AttachEngine3D
  Height = 0.5
  Length = 4.5
  Width = 5.5
FEATURE [Part::Box] Box209  label="Small Cu GND Electrode087"
  AttacherType = Attacher::AttachEngine3D
  Height = 1.15
  Length = 6
  Width = 6.5
FEATURE [Part::Box] Box210  label="Small Cu GND Electrode088"
  AttacherType = Attacher::AttachEngine3D
  Height = 1.05
  Length = 6
  Placement = pos=(0,0,0.05) rot=(0,0,1;0rad)
  Width = 6.45
FEATURE [Part::Box] Box211  label="Small LiNbO3 Plate101"
  AttacherType = Attacher::AttachEngine3D
  Height = 0.5
  Length = 4.5
  Width = 5.5
FEATURE [Part::Box] Box212  label="Small Cu GND Electrode089"
  AttacherType = Attacher::AttachEngine3D
  Height = 1.2
  Length = 5
  Width = 7.5
FEATURE [Part::Box] Box213  label="Small Cu GND Electrode090"
  AttacherType = Attacher::AttachEngine3D
  Height = 1.1
  Length = 5
  Placement = pos=(0,0,0.05) rot=(0,0,1;0rad)
  Width = 7.45
FEATURE [Part::Box] Box214  label="Small Cu GND Electrode091"
  AttacherType = Attacher::AttachEngine3D
  Height = 1.15
  Length = 6
  Width = 6.5
FEATURE [Part::Box] Box215  label="Small Cu GND Electrode092"
  AttacherType = Attacher::AttachEngine3D
  Height = 1.05
  Length = 6
  Placement = pos=(0,0,0.05) rot=(0,0,1;0rad)
  Width = 6.45
FEATURE [Part::Box] Box216  label="Small LiNbO3 Plate102"
  AttacherType = Attacher::AttachEngine3D
  Height = 0.5
  Length = 4.5
  Width = 5.5
FEATURE [Part::Box] Box217  label="Small LiNbO3 Plate103"
  AttacherType = Attacher::AttachEngine3D
  Height = 0.5
  Length = 4.5
  Width = 5.5
FEATURE [Part::Box] Box218  label="Cube015"
  AttacherType = Attacher::AttachEngine3D
  Height = 10
  Length = 10
  Placement = pos=(-5,-5,-10) rot=(0,0,1;0rad)
  Width = 10
FEATURE [Part::Box] Box219  label="Small LiNbO3 Plate104"
  AttacherType = Attacher::AttachEngine3D
  Height = 0.5
  Length = 4.5
  Width = 5.5
FEATURE [Part::Box] Box220  label="Small Cu GND Electrode093"
  AttacherType = Attacher::AttachEngine3D
  Height = 1.15
  Length = 6
  Width = 6.5
FEATURE [Part::Box] Box221  label="Small Cu GND Electrode094"
  AttacherType = Attacher::AttachEngine3D
  Height = 1.05
  Length = 6
  Placement = pos=(0,0,0.05) rot=(0,0,1;0rad)
  Width = 6.45
FEATURE [Part::Box] Box222  label="Small LiNbO3 Plate105"
  AttacherType = Attacher::AttachEngine3D
  Height = 0.5
  Length = 4.5
  Width = 5.5
FEATURE [Part::Box] Box223  label="Small Cu GND Electrode095"
  AttacherType = Attacher::AttachEngine3D
  Height = 1.2
  Length = 5
  Width = 7.5
FEATURE [Part::Box] Box224  label="Small Cu GND Electrode096"
  AttacherType = Attacher::AttachEngine3D
  Height = 1.1
  Length = 5
  Placement = pos=(0,0,0.05) rot=(0,0,1;0rad)
  Width = 7.45
FEATURE [Part::Box] Box225  label="Small Cu GND Electrode097"
  AttacherType = Attacher::AttachEngine3D
  Height = 1.15
  Length = 6
  Width = 6.5
FEATURE [Part::Box] Box226  label="Small Cu GND Electrode098"
  AttacherType = Attacher::AttachEngine3D
  Height = 1.05
  Length = 6
  Placement = pos=(0,0,0.05) rot=(0,0,1;0rad)
  Width = 6.45
FEATURE [Part::Box] Box227  label="Small LiNbO3 Plate106"
  AttacherType = Attacher::AttachEngine3D
  Height = 0.5
  Length = 4.5
  Width = 5.5
FEATURE [Part::Box] Box228  label="Small LiNbO3 Plate107"
  AttacherType = Attacher::AttachEngine3D
  Height = 0.5
  Length = 4.5
  Width = 5.5
FEATURE [Part::Box] Box229  label="Cube016"
  AttacherType = Attacher::AttachEngine3D
  Height = 10
  Length = 10
  Placement = pos=(-5,-5,-10) rot=(0,0,1;0rad)
  Width = 10
FEATURE [Part::Box] Box230  label="Small LiNbO3 Plate108"
  AttacherType = Attacher::AttachEngine3D
  Height = 0.5
  Length = 4.5
  Width = 5.5
FEATURE [Part::Box] Box231  label="Small Cu GND Electrode099"
  AttacherType = Attacher::AttachEngine3D
  Height = 1.15
  Length = 6
  Width = 6.5
FEATURE [Part::Box] Box232  label="Small Cu GND Electrode100"
  AttacherType = Attacher::AttachEngine3D
  Height = 1.05
  Length = 6
  Placement = pos=(0,0,0.05) rot=(0,0,1;0rad)
  Width = 6.45
FEATURE [Part::Box] Box233  label="Small LiNbO3 Plate109"
  AttacherType = Attacher::AttachEngine3D
  Height = 0.5
  Length = 4.5
  Width = 5.5
FEATURE [Part::Box] Box234  label="Small Cu GND Electrode101"
  AttacherType = Attacher::AttachEngine3D
  Height = 1.2
  Length = 5
  Width = 7.5
FEATURE [Part::Box] Box235  label="Small Cu GND Electrode102"
  AttacherType = Attacher::AttachEngine3D
  Height = 1.1
  Length = 5
  Placement = pos=(0,0,0.05) rot=(0,0,1;0rad)
  Width = 7.45
FEATURE [Part::Box] Box236  label="Small Cu GND Electrode103"
  AttacherType = Attacher::AttachEngine3D
  Height = 1.15
  Length = 6
  Width = 6.5
FEATURE [Part::Box] Box237  label="Small Cu GND Electrode104"
  AttacherType = Attacher::AttachEngine3D
  Height = 1.05
  Length = 6
  Placement = pos=(0,0,0.05) rot=(0,0,1;0rad)
  Width = 6.45
FEATURE [Part::Box] Box238  label="Small LiNbO3 Plate110"
  AttacherType = Attacher::AttachEngine3D
  Height = 0.5
  Length = 4.5
  Width = 5.5
FEATURE [Part::Box] Box239  label="Small LiNbO3 Plate111"
  AttacherType = Attacher::AttachEngine3D
  Height = 0.5
  Length = 4.5
  Width = 5.5
FEATURE [Part::Box] Box240  label="Cube017"
  AttacherType = Attacher::AttachEngine3D
  Height = 10
  Length = 10
  Placement = pos=(-5,-5,-10) rot=(0,0,1;0rad)
  Width = 10
FEATURE [Part::Cut] Cut108  label="Small Cu Electrode, Short Axis, GND011"
  Base = -> Box209
  Placement = pos=(-5.25005,9.80114,9.92) rot=(0,0,-1;2.1293rad)
  Refine = true
  Tool = -> Box210
FEATURE [Part::Cut] Cut110  label="Small Cu Electrode001, Long Axis, V011"
  Base = -> Box212
  Placement = pos=(-8.42956,4.71285,10.47) rot=(0,0,1;5.72468rad)
  Refine = true
  Tool = -> Box213
FEATURE [Part::Cut] Cut111  label="Small Cu Electrode002, Short Axis, GND011"
  Base = -> Box214
  Placement = pos=(-5.25005,9.80114,11.07) rot=(0,0,-1;2.1293rad)
  Refine = true
  Tool = -> Box215
FEATURE [Part::Cut] Cut116  label="Small Cu Electrode, Short Axis, GND012"
  Base = -> Box220
  Placement = pos=(-5.25005,27.6411,9.92) rot=(0,0,-1;2.1293rad)
  Refine = true
  Tool = -> Box221
FEATURE [Part::Cut] Cut118  label="Small Cu Electrode001, Long Axis, V012"
  Base = -> Box223
  Placement = pos=(-8.42956,22.5529,10.47) rot=(0,0,1;5.72468rad)
  Refine = true
  Tool = -> Box224
FEATURE [Part::Cut] Cut119  label="Small Cu Electrode002, Short Axis, GND012"
  Base = -> Box225
  Placement = pos=(-5.25005,27.6411,11.07) rot=(0,0,-1;2.1293rad)
  Refine = true
  Tool = -> Box226
FEATURE [Part::Cut] Cut124  label="Small Cu Electrode, Short Axis, GND013"
  Base = -> Box231
  Placement = pos=(10.2,18.7211,9.92) rot=(0,0,-1;2.1293rad)
  Refine = true
  Tool = -> Box232
FEATURE [Part::Cut] Cut126  label="Small Cu Electrode001, Long Axis, V013"
  Base = -> Box234
  Placement = pos=(7.02044,13.6329,10.47) rot=(0,0,1;5.72468rad)
  Refine = true
  Tool = -> Box235
FEATURE [Part::Cut] Cut127  label="Small Cu Electrode002, Short Axis, GND013"
  Base = -> Box236
  Placement = pos=(10.2,18.7211,11.07) rot=(0,0,-1;2.1293rad)
  Refine = true
  Tool = -> Box237
FEATURE [Part::Cylinder] Cylinder094  label="KJ_D401_013"
  Angle = 360
  AttacherType = Attacher::AttachEngine3D
  FirstAngle = 0
  Height = 0.79
  Placement = pos=(1,14.39,8.58) rot=(0,0,1;0rad)
  Radius = 3.18
  SecondAngle = 0
FEATURE [Part::Cylinder] Cylinder095  label="KJ_D401_014"
  Angle = 360
  AttacherType = Attacher::AttachEngine3D
  FirstAngle = 0
  Height = 0.79
  Placement = pos=(1,14.39,9.62) rot=(0,0,1;0rad)
  Radius = 3.18
  SecondAngle = 0
FEATURE [Part::Cylinder] Cylinder096  label="KJ_D401_015"
  Angle = 360
  AttacherType = Attacher::AttachEngine3D
  FirstAngle = 0
  Height = 0.79
  Placement = pos=(1,14.39,10.66) rot=(0,0,1;0rad)
  Radius = 3.18
  SecondAngle = 0
FEATURE [Part::Cylinder] Cylinder097  label="KJ_D401_016"
  Angle = 360
  AttacherType = Attacher::AttachEngine3D
  FirstAngle = 0
  Height = 0.79
  Placement = pos=(1,14.39,11.7) rot=(0,0,1;0rad)
  Radius = 3.18
  SecondAngle = 0
FEATURE [Part::Cylinder] Cylinder098  label="KJ_D31SH011"
  Angle = 360
  AttacherType = Attacher::AttachEngine3D
  FirstAngle = 0
  Height = 1.59
  Placement = pos=(-5.15,5.47,8.33) rot=(0,0,1;5.72468rad)
  Radius = 2.38
  SecondAngle = 0
FEATURE [Part::Cylinder] Cylinder099
  Angle = 360
  AttacherType = Attacher::AttachEngine3D
  FirstAngle = 0
  Height = 0.01
  Placement = pos=(1,4.5,0.49) rot=(0,0,1;0rad)
  Radius = 0.5
  SecondAngle = 0
FEATURE [Part::Cut] Cut107  label="Small LiNbO3 Plate112"
  Base = -> Box208
  Placement = pos=(-8.42956,4.71285,9.97) rot=(0,0,1;5.72468rad)
  Refine = true
  Tool = -> Cylinder099
FEATURE [Part::Cylinder] Cylinder100
  Angle = 360
  AttacherType = Attacher::AttachEngine3D
  FirstAngle = 0
  Height = 0.01
  Placement = pos=(1,4.5,0.49) rot=(0,0,1;0rad)
  Radius = 0.5
  SecondAngle = 0
FEATURE [Part::Cut] Cut109  label="Small LiNbO3 Plate113"
  Base = -> Box211
  Placement = pos=(-1.69879,6.99248,10.52) rot=(0,0,-1;3.7001rad)
  Refine = true
  Tool = -> Cylinder100
FEATURE [Part::Cylinder] Cylinder101
  Angle = 360
  AttacherType = Attacher::AttachEngine3D
  FirstAngle = 0
  Height = 0.01
  Placement = pos=(1,4.5,0.49) rot=(0,0,1;0rad)
  Radius = 0.5
  SecondAngle = 0
FEATURE [Part::Cut] Cut112  label="Small LiNbO3 Plate114"
  Base = -> Box216
  Placement = pos=(-8.42956,4.71285,11.12) rot=(0,0,1;5.72468rad)
  Refine = true
  Tool = -> Cylinder101
FEATURE [Part::Cylinder] Cylinder102
  Angle = 360
  AttacherType = Attacher::AttachEngine3D
  FirstAngle = 0
  Height = 0.01
  Placement = pos=(1,4.5,0.49) rot=(0,0,1;0rad)
  Radius = 0.5
  SecondAngle = 0
FEATURE [Part::Cut] Cut113  label="Small LiNbO3 Plate115"
  Base = -> Box217
  Placement = pos=(-1.69879,6.99248,11.67) rot=(0,0,-1;3.7001rad)
  Refine = true
  Tool = -> Cylinder102
FEATURE [Part::Cylinder] Cylinder103  label="KJ_D31SH012"
  Angle = 360
  AttacherType = Attacher::AttachEngine3D
  FirstAngle = 0
  Height = 1.59
  Placement = pos=(-5.15,23.31,8.33) rot=(0,0,1;5.72468rad)
  Radius = 2.38
  SecondAngle = 0
FEATURE [Part::Cylinder] Cylinder104
  Angle = 360
  AttacherType = Attacher::AttachEngine3D
  FirstAngle = 0
  Height = 0.01
  Placement = pos=(1,4.5,0.49) rot=(0,0,1;0rad)
  Radius = 0.5
  SecondAngle = 0
FEATURE [Part::Cut] Cut115  label="Small LiNbO3 Plate116"
  Base = -> Box219
  Placement = pos=(-8.42956,22.5529,9.97) rot=(0,0,1;5.72468rad)
  Refine = true
  Tool = -> Cylinder104
FEATURE [Part::Cylinder] Cylinder105
  Angle = 360
  AttacherType = Attacher::AttachEngine3D
  FirstAngle = 0
  Height = 0.01
  Placement = pos=(1,4.5,0.49) rot=(0,0,1;0rad)
  Radius = 0.5
  SecondAngle = 0
FEATURE [Part::Cut] Cut117  label="Small LiNbO3 Plate117"
  Base = -> Box222
  Placement = pos=(-1.69879,24.8325,10.52) rot=(0,0,-1;3.7001rad)
  Refine = true
  Tool = -> Cylinder105
FEATURE [Part::Cylinder] Cylinder106
  Angle = 360
  AttacherType = Attacher::AttachEngine3D
  FirstAngle = 0
  Height = 0.01
  Placement = pos=(1,4.5,0.49) rot=(0,0,1;0rad)
  Radius = 0.5
  SecondAngle = 0
FEATURE [Part::Cut] Cut120  label="Small LiNbO3 Plate118"
  Base = -> Box227
  Placement = pos=(-8.42956,22.5529,11.12) rot=(0,0,1;5.72468rad)
  Refine = true
  Tool = -> Cylinder106
FEATURE [Part::Cylinder] Cylinder107
  Angle = 360
  AttacherType = Attacher::AttachEngine3D
  FirstAngle = 0
  Height = 0.01
  Placement = pos=(1,4.5,0.49) rot=(0,0,1;0rad)
  Radius = 0.5
  SecondAngle = 0
FEATURE [Part::Cut] Cut121  label="Small LiNbO3 Plate119"
  Base = -> Box228
  Placement = pos=(-1.69879,24.8325,11.67) rot=(0,0,-1;3.7001rad)
  Refine = true
  Tool = -> Cylinder107
FEATURE [Part::Cylinder] Cylinder108  label="KJ_D31SH013"
  Angle = 360
  AttacherType = Attacher::AttachEngine3D
  FirstAngle = 0
  Height = 1.59
  Placement = pos=(10.3,14.39,8.33) rot=(0,0,1;5.72468rad)
  Radius = 2.38
  SecondAngle = 0
FEATURE [Part::Cylinder] Cylinder109
  Angle = 360
  AttacherType = Attacher::AttachEngine3D
  FirstAngle = 0
  Height = 0.01
  Placement = pos=(1,4.5,0.49) rot=(0,0,1;0rad)
  Radius = 0.5
  SecondAngle = 0
FEATURE [Part::Cut] Cut123  label="Small LiNbO3 Plate120"
  Base = -> Box230
  Placement = pos=(7.02044,13.6329,9.97) rot=(0,0,1;5.72468rad)
  Refine = true
  Tool = -> Cylinder109
FEATURE [Part::Cylinder] Cylinder110
  Angle = 360
  AttacherType = Attacher::AttachEngine3D
  FirstAngle = 0
  Height = 0.01
  Placement = pos=(1,4.5,0.49) rot=(0,0,1;0rad)
  Radius = 0.5
  SecondAngle = 0
FEATURE [Part::Cut] Cut125  label="Small LiNbO3 Plate121"
  Base = -> Box233
  Placement = pos=(13.7512,15.9125,10.52) rot=(0,0,-1;3.7001rad)
  Refine = true
  Tool = -> Cylinder110
FEATURE [Part::Cylinder] Cylinder111
  Angle = 360
  AttacherType = Attacher::AttachEngine3D
  FirstAngle = 0
  Height = 0.01
  Placement = pos=(1,4.5,0.49) rot=(0,0,1;0rad)
  Radius = 0.5
  SecondAngle = 0
FEATURE [Part::Cut] Cut128  label="Small LiNbO3 Plate122"
  Base = -> Box238
  Placement = pos=(7.02044,13.6329,11.12) rot=(0,0,1;5.72468rad)
  Refine = true
  Tool = -> Cylinder111
FEATURE [Part::Cylinder] Cylinder112
  Angle = 360
  AttacherType = Attacher::AttachEngine3D
  FirstAngle = 0
  Height = 0.01
  Placement = pos=(1,4.5,0.49) rot=(0,0,1;0rad)
  Radius = 0.5
  SecondAngle = 0
FEATURE [Part::Cut] Cut129  label="Small LiNbO3 Plate123"
  Base = -> Box239
  Placement = pos=(13.7512,15.9125,11.67) rot=(0,0,-1;3.7001rad)
  Refine = true
  Tool = -> Cylinder112
FEATURE [App::DocumentObjectGroup] Group025  label="Magnet Stack003"
  Group = -> [Box204,Cylinder094,Box205,Cylinder095,Box206,Cylinder096,Box207,Cylinder097]
FEATURE [Part::Sphere] Sphere015
  Angle1 = -90
  Angle2 = 90
  Angle3 = 360
  AttacherType = Attacher::AttachEngine3D
  Radius = 2
FEATURE [Part::Cut] Cut114  label="Sapphire Half-Ball Lens015"
  Base = -> Sphere015
  Placement = pos=(-5.15,5.47,12.22) rot=(0,0,1;5.72468rad)
  Refine = true
  Tool = -> Box218
FEATURE [App::DocumentObjectGroup] Group026  label="Coarse Piezo Stack, Rotated010"
  Group = -> [Cylinder098,Cut108,Cut107,Cut110,Cut109,Cut111,Cut112,Cut113,Cut114]
FEATURE [Part::Sphere] Sphere016
  Angle1 = -90
  Angle2 = 90
  Angle3 = 360
  AttacherType = Attacher::AttachEngine3D
  Radius = 2
FEATURE [Part::Cut] Cut122  label="Sapphire Half-Ball Lens016"
  Base = -> Sphere016
  Placement = pos=(-5.15,23.31,12.22) rot=(0,0,1;5.72468rad)
  Refine = true
  Tool = -> Box229
FEATURE [App::DocumentObjectGroup] Group027  label="Coarse Piezo Stack, Rotated011"
  Group = -> [Cylinder103,Cut116,Cut115,Cut118,Cut117,Cut119,Cut120,Cut121,Cut122]
FEATURE [Part::Sphere] Sphere017
  Angle1 = -90
  Angle2 = 90
  Angle3 = 360
  AttacherType = Attacher::AttachEngine3D
  Radius = 2
FEATURE [Part::Cut] Cut130  label="Sapphire Half-Ball Lens017"
  Base = -> Sphere017
  Placement = pos=(10.3,14.39,12.22) rot=(0,0,1;5.72468rad)
  Refine = true
  Tool = -> Box240
FEATURE [App::DocumentObjectGroup] Group028  label="Coarse Piezo Stack, Rotated012"
  Group = -> [Cylinder108,Cut124,Cut123,Cut126,Cut125,Cut127,Cut128,Cut129,Cut130]
FEATURE [App::DocumentObjectGroup] Group029  label="Coarse Y Piezo Tripod"
  Group = -> [Group026,Group027,Group028,Group025]
FEATURE [App::Point] Origin035  label="Origin041"
  Role = Origin
FEATURE [Sketcher::SketchObject] Sketch017
  ArcFitTolerance = 1e-06
  AttachmentSupport = -> [Origin034]
  ExternalTypes = [0]
  FullyConstrained = true
  MakeInternals = false
  MapMode = 5
  sketch-geometry (16):
    g0: LineSegment StartX=-7.65 StartY=-14.92 StartZ=0 EndX=-7.65 EndY=14.92 EndZ=0
    g1: LineSegment StartX=-7.65 StartY=14.92 StartZ=0 EndX=-2.65 EndY=14.92 EndZ=0
    g2: LineSegment StartX=-7.65 StartY=-14.92 StartZ=0 EndX=-2.65 EndY=-14.92 EndZ=0
    g3: LineSegment StartX=12.3 StartY=6 StartZ=0 EndX=12.3 EndY=-6 EndZ=0
    g4: LineSegment StartX=-2.65 StartY=14.92 StartZ=0 EndX=-2.65 EndY=12 EndZ=0
    g5: LineSegment StartX=-2.65 StartY=-14.92 StartZ=0 EndX=-2.65 EndY=-12 EndZ=0
    g6: LineSegment StartX=12.3 StartY=6 StartZ=0 EndX=7 EndY=6 EndZ=0
    g7: LineSegment StartX=12.3 StartY=-6 StartZ=0 EndX=7 EndY=-6 EndZ=0
    g8: LineSegment StartX=-0.65 StartY=10 StartZ=0 EndX=3 EndY=10 EndZ=0
    g9: ArcOfCircle CenterX=-0.65 CenterY=12 CenterZ=0 NormalX=0 NormalY=0 NormalZ=1 AngleXU=0 Radius=2 StartAngle=3.14159 EndAngle=4.71239
    g10: ArcOfCircle CenterX=7 CenterY=8 CenterZ=0 NormalX=0 NormalY=0 NormalZ=1 AngleXU=0 Radius=2 StartAngle=3.14159 EndAngle=4.71239
    g11: LineSegment StartX=-0.65 StartY=-10 StartZ=0 EndX=3 EndY=-10 EndZ=0
    g12: ArcOfCircle CenterX=-0.65 CenterY=-12 CenterZ=0 NormalX=0 NormalY=0 NormalZ=1 AngleXU=0 Radius=2 StartAngle=1.5708 EndAngle=3.14159
    g13: ArcOfCircle CenterX=7 CenterY=-8 CenterZ=0 NormalX=0 NormalY=0 NormalZ=1 AngleXU=0 Radius=2 StartAngle=1.5708 EndAngle=3.14159
    g14: ArcOfCircle CenterX=3 CenterY=8 CenterZ=0 NormalX=0 NormalY=0 NormalZ=1 AngleXU=0 Radius=2 StartAngle=0 EndAngle=1.5708
    g15: ArcOfCircle CenterX=3 CenterY=-8 CenterZ=0 NormalX=0 NormalY=0 NormalZ=1 AngleXU=0 Radius=2 StartAngle=4.71239 EndAngle=6.28319
  constraints (46):
    c: Vertical(g0)
    c: Coincident(g1,g0)
    c: Horizontal(g1)
    c: Coincident(g2,g0)
    c: Horizontal(g2)
    c: Distance(g-1,g1) = 14.92
    c: Distance(g-1,g2) = 14.92
    c: Distance(g-1,g0) = 7.65
    c: Vertical(g3)
    c: Distance(g-1,g3) = 12.3
    c: DistanceX(g1,g1) = 5
    c: Equal(g1,g2)
    c: DistanceY(g-1,g3) = 6
    c: DistanceY(g-1,g3) = -6
    c: Coincident(g4,g1)
    c: Vertical(g4)
    c: Coincident(g5,g2)
    c: Vertical(g5)
    c: Coincident(g6,g3)
    c: Horizontal(g6)
    c: Horizontal(g7)
    c: Coincident(g7,g3)
    c: Equal(g4,g5)
    c: Equal(g7,g6)
    c: Horizontal(g8)
    c: Tangent(g9,g4) = -1.5708
    c: Tangent(g9,g8) = -1.5708
    c: Tangent(g10,g6) = 1.5708
    c: Horizontal(g11)
    c: Tangent(g5,g12) = 1.5708
    c: Tangent(g11,g12) = 1.5708
    c: Tangent(g7,g13) = -1.5708
    c: Equal(g8,g11)
    c: Equal(g9,g12)
    c: Radius(g9) = 2
    c: Radius(g10) = 2
    c: Tangent(g8,g14) = 1.5708
    c: Tangent(g15,g11) = -1.5708
    c: Equal(g14,g10)
    c: Angle(g14) = 1.5708
    c: Angle(g10) = 1.5708
    c: Coincident(g10,g14)
    c: Coincident(g13,g15)
    c: Angle(g13) = 1.5708
    c: Equal(g13,g10)
    c: DistanceX(g-2,g13) = 5
FEATURE [PartDesign::Pad] Pad004
  Direction = (0,0,1)
  Length = 3
  Length2 = 10
  Profile = -> Sketch017
  ReferenceAxis = -> Sketch017 [N_Axis]
  Refine = true
  SideType = 0
  Suppressed = false
  Type = 0
  Type2 = 0
FEATURE [Sketcher::SketchObject] Sketch018
  ArcFitTolerance = 1e-06
  AttachmentSupport = -> [Origin034]
  ExternalTypes = [0]
  FullyConstrained = true
  MakeInternals = false
  MapMode = 5
  Placement = pos=(0,0,0) rot=(1,0,0;1.5708rad)
  sketch-geometry (3):
    g0: LineSegment StartX=-5.15 StartY=0.866025 StartZ=0 EndX=-6.65 EndY=0 EndZ=0
    g1: LineSegment StartX=-5.15 StartY=0.866025 StartZ=0 EndX=-3.65 EndY=0 EndZ=0
    g2: LineSegment StartX=-3.65 StartY=0 StartZ=0 EndX=-6.65 EndY=0 EndZ=0
  constraints (9):
    c: Coincident(g1,g0)
    c: Coincident(g2,g1)
    c: Coincident(g2,g0)
    c: PointOnObject(g1,g-1)
    c: PointOnObject(g0,g-1)
    c: Distance(g-1,g1) = 3.65
    c: Distance(g1,g0) = 3
    c: Equal(g0,g1)
    c: Angle(g0,g1) = 2.0944
FEATURE [PartDesign::Pocket] Pocket012
  BaseFeature = -> Pad004
  Direction = (0,1,-2e-16)
  Length = 5
  Length2 = 5
  Profile = -> Sketch018
  ReferenceAxis = -> Sketch018 [N_Axis]
  Refine = true
  SideType = 2
  Suppressed = false
  Type = 1
  Type2 = 0
FEATURE [Sketcher::SketchObject] Sketch019
  ArcFitTolerance = 1e-06
  AttachmentSupport = -> [Origin034]
  ExternalTypes = [0]
  FullyConstrained = true
  MakeInternals = false
  MapMode = 5
  Placement = pos=(0,0,0) rot=(1,0,0;1.5708rad)
  sketch-geometry (4):
    g0: LineSegment StartX=7.3 StartY=0.56 StartZ=0 EndX=7.3 EndY=0 EndZ=0
    g1: LineSegment StartX=7.3 StartY=0 StartZ=0 EndX=12.3 EndY=0 EndZ=0
    g2: LineSegment StartX=12.3 StartY=0 StartZ=0 EndX=12.3 EndY=0.56 EndZ=0
    g3: LineSegment StartX=12.3 StartY=0.56 StartZ=0 EndX=7.3 EndY=0.56 EndZ=0
  constraints (12):
    c: Coincident(g0,g1)
    c: Coincident(g1,g2)
    c: Coincident(g2,g3)
    c: Coincident(g3,g0)
    c: Vertical(g0)
    c: Vertical(g2)
    c: Horizontal(g1)
    c: Horizontal(g3)
    c: Distance(g-1,g0) = 7.3
    c: DistanceX(g3,g3) = 5
    c: PointOnObject(g0,g-1)
    c: DistanceY(g0,g0) = 0.56
FEATURE [PartDesign::Pocket] Pocket013
  BaseFeature = -> Pocket012
  Direction = (0,1,-2e-16)
  Length = 5
  Length2 = 5
  Profile = -> Sketch019
  ReferenceAxis = -> Sketch019 [N_Axis]
  Refine = true
  SideType = 2
  Suppressed = false
  Type = 1
  Type2 = 0
FEATURE [PartDesign::Body] Body004  label="Coarse Y Slider"
  AllowCompound = false
  Group = -> [Sketch017,Pad004,Sketch018,Pocket012,Sketch019,Pocket013]
  Origin = -> Origin034
  Placement = pos=(0,14.39,13.66) rot=(0,0,1;0rad)
  Tip = -> Pocket013
FEATURE [App::Point] Origin037  label="Origin043"
  Role = Origin
FEATURE [Sketcher::SketchObject] Sketch020
  ArcFitTolerance = 1e-06
  AttachmentSupport = -> [Origin036]
  ExternalTypes = [0]
  FullyConstrained = true
  MakeInternals = false
  MapMode = 5
  sketch-geometry (20):
    g0: LineSegment StartX=-7.65 StartY=14.92 StartZ=0 EndX=0 EndY=14.92 EndZ=0
    g1: LineSegment StartX=-7.65 StartY=-14.92 StartZ=0 EndX=-2.65 EndY=-14.92 EndZ=0
    g2: LineSegment StartX=12.3 StartY=6 StartZ=0 EndX=12.3 EndY=-6 EndZ=0
    g3: LineSegment StartX=-2.65 StartY=-14.92 StartZ=0 EndX=-2.65 EndY=-12 EndZ=0
    g4: LineSegment StartX=12.3 StartY=6 StartZ=0 EndX=6 EndY=6 EndZ=0
    g5: ArcOfCircle CenterX=6 CenterY=8 CenterZ=0 NormalX=0 NormalY=0 NormalZ=1 AngleXU=0 Radius=2 StartAngle=3.14159 EndAngle=4.71239
    g6: LineSegment StartX=-0.65 StartY=-10 StartZ=0 EndX=8.3 EndY=-10 EndZ=0
    g7: ArcOfCircle CenterX=-0.65 CenterY=-12 CenterZ=0 NormalX=0 NormalY=0 NormalZ=1 AngleXU=0 Radius=2 StartAngle=1.5708 EndAngle=3.14159
    g8: GeomPoint [constr] X=8.92 Y=-5.15 Z=0
    g9: GeomPoint [constr] X=-8.92 Y=-5.15 Z=0
    g10: GeomPoint [constr] X=0 Y=10.3 Z=0
    g11: ArcOfCircle CenterX=8.3 CenterY=-6 CenterZ=0 NormalX=0 NormalY=0 NormalZ=1 AngleXU=0 Radius=4 StartAngle=4.71239 EndAngle=6.28319
    g12: ArcOfCircle CenterX=-5e-16 CenterY=10.92 CenterZ=0 NormalX=0 NormalY=0 NormalZ=1 AngleXU=0 Radius=4 StartAngle=0 EndAngle=1.5708
    g13: LineSegment StartX=4 StartY=10.92 StartZ=0 EndX=4 EndY=8 EndZ=0
    g14: LineSegment StartX=-7.65 StartY=14.92 StartZ=0 EndX=-7.65 EndY=-0.15 EndZ=0
    g15: LineSegment StartX=-7.65 StartY=-14.92 StartZ=0 EndX=-7.65 EndY=-10.15 EndZ=0
    g16: ArcOfCircle CenterX=-9.65 CenterY=-10.15 CenterZ=0 NormalX=0 NormalY=0 NormalZ=1 AngleXU=0 Radius=2 StartAngle=3e-16 EndAngle=1.5708
    g17: ArcOfCircle CenterX=-9.65 CenterY=-0.15 CenterZ=0 NormalX=0 NormalY=0 NormalZ=1 AngleXU=0 Radius=2 StartAngle=4.71239 EndAngle=6.28319
    g18: ArcOfCircle CenterX=-9.65 CenterY=-5.15 CenterZ=0 NormalX=0 NormalY=0 NormalZ=1 AngleXU=0 Radius=3 StartAngle=1.5708 EndAngle=3.14159
    g19: ArcOfCircle CenterX=-9.65 CenterY=-5.15 CenterZ=0 NormalX=0 NormalY=0 NormalZ=1 AngleXU=0 Radius=3 StartAngle=3.14159 EndAngle=4.71239
  constraints (53):
    c: Horizontal(g0)
    c: Horizontal(g1)
    c: Distance(g-1,g0) = 14.92
    c: Distance(g-1,g1) = 14.92
    c: Vertical(g2)
    c: Distance(g-1,g2) = 12.3
    c: DistanceX(g0,g0) = 7.65
    c: DistanceY(g-1,g2) = 6
    c: DistanceY(g-1,g2) = -6
    c: Coincident(g3,g1)
    c: Vertical(g3)
    c: Coincident(g4,g2)
    c: Horizontal(g4)
    c: Tangent(g5,g4) = 1.5708
    c: Horizontal(g6)
    c: Tangent(g3,g7) = 1.5708
    c: Tangent(g6,g7) = 1.5708
    c: Radius(g5) = 2
    c: Distance(g-1,g6) = 10
    c: DistanceY(g-1,g8) = -5.15
    c: DistanceX(g-2,g8) = 8.92
    c: DistanceY(g-1,g9) = -5.15
    c: DistanceX(g-2,g9) = -8.92
    c: PointOnObject(g10,g-2)
    c: DistanceY(g-1,g10) = 10.3
    c: Radius(g11) = 4
    c: Coincident(g11,g2)
    c: Tangent(g11,g6) = -1.5708
    c: Radius(g12) = 4
    c: Tangent(g0,g12) = 1.5708
    c: Vertical(g13)
    c: Tangent(g12,g13) = 1.5708
    c: Tangent(g5,g13) = -1.5708
    c: Radius(g7) = 2
    c: Coincident(g14,g0)
    c: Vertical(g14)
    c: Coincident(g15,g1)
    c: Vertical(g15)
    c: Radius(g17) = 2
    c: Equal(g17,g16)
    c: PointOnObject(g0,g-2)
    c: Tangent(g17,g14) = 1.5708
    c: Tangent(g15,g16) = -1.5708
    c: Angle(g18) = 1.5708
    c: Angle(g19) = 1.5708
    c: Radius(g18) = 3
    c: Equal(g18,g19)
    c: Tangent(g19,g18) = -1.5708
    c: Tangent(g17,g18) = 1.5708
    c: Tangent(g19,g16) = 1.5708
    c: DistanceY(g-1,g18) = -5.15
    c: Distance(g3,g15) = 5
    c: DistanceX(g1,g-1) = 7.65
FEATURE [PartDesign::Pad] Pad005
  Direction = (0,0,1)
  Length = 3
  Length2 = 10
  Profile = -> Sketch020
  ReferenceAxis = -> Sketch020 [N_Axis]
  Refine = true
  SideType = 0
  Suppressed = false
  Type = 0
  Type2 = 0
FEATURE [Sketcher::SketchObject] Sketch021
  ArcFitTolerance = 1e-06
  AttachmentSupport = -> [Origin036]
  ExternalTypes = [0]
  FullyConstrained = true
  MakeInternals = false
  MapMode = 5
  Placement = pos=(0,0,0) rot=(1,0,0;1.5708rad)
  sketch-geometry (3):
    g0: LineSegment StartX=-5.15 StartY=0.866025 StartZ=0 EndX=-6.65 EndY=0 EndZ=0
    g1: LineSegment StartX=-5.15 StartY=0.866025 StartZ=0 EndX=-3.65 EndY=0 EndZ=0
    g2: LineSegment StartX=-3.65 StartY=0 StartZ=0 EndX=-6.65 EndY=0 EndZ=0
  constraints (9):
    c: Coincident(g1,g0)
    c: Coincident(g2,g1)
    c: Coincident(g2,g0)
    c: PointOnObject(g1,g-1)
    c: PointOnObject(g0,g-1)
    c: Distance(g-1,g1) = 3.65
    c: Distance(g1,g0) = 3
    c: Equal(g0,g1)
    c: Angle(g0,g1) = 2.0944
FEATURE [PartDesign::Pocket] Pocket014
  BaseFeature = -> Pad005
  Direction = (0,1,-2e-16)
  Length = 5
  Length2 = 5
  Profile = -> Sketch021
  ReferenceAxis = -> Sketch021 [N_Axis]
  Refine = true
  SideType = 2
  Suppressed = false
  Type = 1
  Type2 = 0
FEATURE [Sketcher::SketchObject] Sketch022
  ArcFitTolerance = 1e-06
  AttachmentSupport = -> [Origin036]
  ExternalTypes = [0]
  FullyConstrained = true
  MakeInternals = false
  MapMode = 5
  Placement = pos=(0,0,0) rot=(1,0,0;1.5708rad)
  sketch-geometry (4):
    g0: LineSegment StartX=7.3 StartY=0.56 StartZ=0 EndX=7.3 EndY=0 EndZ=0
    g1: LineSegment StartX=7.3 StartY=0 StartZ=0 EndX=12.3 EndY=0 EndZ=0
    g2: LineSegment StartX=12.3 StartY=0 StartZ=0 EndX=12.3 EndY=0.56 EndZ=0
    g3: LineSegment StartX=12.3 StartY=0.56 StartZ=0 EndX=7.3 EndY=0.56 EndZ=0
  constraints (12):
    c: Coincident(g0,g1)
    c: Coincident(g1,g2)
    c: Coincident(g2,g3)
    c: Coincident(g3,g0)
    c: Vertical(g0)
    c: Vertical(g2)
    c: Horizontal(g1)
    c: Horizontal(g3)
    c: Distance(g-1,g0) = 7.3
    c: DistanceX(g3,g3) = 5
    c: PointOnObject(g0,g-1)
    c: DistanceY(g0,g0) = 0.56
FEATURE [PartDesign::Pocket] Pocket015
  BaseFeature = -> Pocket014
  Direction = (0,1,-2e-16)
  Length = 5
  Length2 = 5
  Profile = -> Sketch022
  ReferenceAxis = -> Sketch022 [N_Axis]
  Refine = true
  SideType = 2
  Suppressed = false
  Type = 1
  Type2 = 0
FEATURE [PartDesign::Body] Body005  label="Coarse X Slider"
  AllowCompound = false
  Group = -> [Sketch020,Pad005,Sketch021,Pocket014,Sketch022,Pocket015]
  Origin = -> Origin036
  Placement = pos=(0,14.39,5.33) rot=(0,0,1;-1.5708rad)
  Tip = -> Pocket015
FEATURE [Part::Box] Box241  label="Glass Cover Slip"
  AttacherType = Attacher::AttachEngine3D
  Height = 0.15
  Length = 12
  Placement = pos=(-4.76,9.63,22.85) rot=(0,0,1;0rad)
  Width = 12
FEATURE [Part::Box] Box242  label="Bias Voltage Electrode"
  AttacherType = Attacher::AttachEngine3D
  Height = 0.05
  Length = 12
  Placement = pos=(-4.76,9.63,23) rot=(0,0,1;0rad)
  Width = 12
FEATURE [App::DocumentObjectGroup] Group  label="Fine XY Piezo Stack"
  Group = -> [Cylinder022,Cut015,Cut013,Cut016,Cut014,Cut017,Cut018,Cut019,Cut024,Cut020,Cut026,Cut021,Cut025,Cut022,Cut023,Box241,Cylinder031,Box242]
FEATURE [Part::Cylinder] Cylinder  label="Steel Disc"
  Angle = 360
  AttacherType = Attacher::AttachEngine3D
  FirstAngle = 0
  Height = 1
  Placement = pos=(0,14.39,24.64) rot=(0,0,1;0rad)
  Radius = 6.35
  SecondAngle = 0
FEATURE [Part::Box] Box243  label="HOPG"
  AttacherType = Attacher::AttachEngine3D
  Height = 0.025
  Length = 10
  Placement = pos=(-5,9.39,25.64) rot=(0,0,1;0rad)
  Width = 10
FEATURE [App::Point] Origin039  label="Origin045"
  Role = Origin
FEATURE [Sketcher::SketchObject] Sketch023
  ArcFitTolerance = 1e-06
  AttachmentSupport = -> [Origin038]
  ExternalTypes = [0]
  FullyConstrained = true
  MakeInternals = false
  MapMode = 5
  sketch-geometry (12):
    g0: LineSegment StartX=-4.5 StartY=4.5 StartZ=0 EndX=-4.5 EndY=6.5 EndZ=0
    g1: LineSegment StartX=-4.5 StartY=6.5 StartZ=0 EndX=4.5 EndY=6.5 EndZ=0
    g2: LineSegment StartX=4.5 StartY=6.5 StartZ=0 EndX=4.5 EndY=4.5 EndZ=0
    g3: LineSegment StartX=4.5 StartY=4.5 StartZ=0 EndX=6.5 EndY=4.5 EndZ=0
    g4: LineSegment StartX=6.5 StartY=4.5 StartZ=0 EndX=6.5 EndY=-4.5 EndZ=0
    g5: LineSegment StartX=6.5 StartY=-4.5 StartZ=0 EndX=4.5 EndY=-4.5 EndZ=0
    g6: LineSegment StartX=4.5 StartY=-4.5 StartZ=0 EndX=4.5 EndY=-6.5 EndZ=0
    g7: LineSegment StartX=4.5 StartY=-6.5 StartZ=0 EndX=-4.5 EndY=-6.5 EndZ=0
    g8: LineSegment StartX=-4.5 StartY=-6.5 StartZ=0 EndX=-4.5 EndY=-4.5 EndZ=0
    g9: LineSegment StartX=-4.5 StartY=-4.5 StartZ=0 EndX=-6.5 EndY=-4.5 EndZ=0
    g10: LineSegment StartX=-6.5 StartY=-4.5 StartZ=0 EndX=-6.5 EndY=4.5 EndZ=0
    g11: LineSegment StartX=-6.5 StartY=4.5 StartZ=0 EndX=-4.5 EndY=4.5 EndZ=0
  constraints (35):
    c: Vertical(g0)
    c: Coincident(g1,g0)
    c: Horizontal(g1)
    c: Coincident(g2,g1)
    c: Vertical(g2)
    c: Coincident(g3,g2)
    c: Horizontal(g3)
    c: Coincident(g4,g3)
    c: Vertical(g4)
    c: Coincident(g5,g4)
    c: Horizontal(g5)
    c: Coincident(g6,g5)
    c: Vertical(g6)
    c: Coincident(g7,g6)
    c: Horizontal(g7)
    c: Coincident(g8,g7)
    c: Vertical(g8)
    c: Coincident(g9,g8)
    c: Horizontal(g9)
    c: Coincident(g10,g9)
    c: Vertical(g10)
    c: Coincident(g11,g10)
    c: Coincident(g11,g0)
    c: Horizontal(g11)
    c: Symmetric(g2,g8,g-1)
    c: Equal(g11,g0)
    c: Equal(g11,g2)
    c: Equal(g11,g3)
    c: Equal(g11,g9)
    c: Equal(g11,g8)
    c: Equal(g11,g6)
    c: Equal(g11,g5)
    c: Equal(g1,g10)
    c: DistanceX(g11,g11) = 2
    c: Distance(g3,g10) = 13
FEATURE [PartDesign::Pad] Pad006
  Direction = (0,0,1)
  Length = 0.07
  Length2 = 10
  Profile = -> Sketch023
  ReferenceAxis = -> Sketch023 [N_Axis]
  Refine = true
  SideType = 0
  Suppressed = false
  Type = 0
  Type2 = 0
FEATURE [Sketcher::SketchObject] Sketch024
  ArcFitTolerance = 1e-06
  AttachmentSupport = -> [Origin038]
  ExternalTypes = [0]
  FullyConstrained = true
  MakeInternals = false
  MapMode = 5
  sketch-geometry (4):
    g0: LineSegment StartX=-4 StartY=4 StartZ=0 EndX=-4 EndY=-4 EndZ=0
    g1: LineSegment StartX=-4 StartY=-4 StartZ=0 EndX=4 EndY=-4 EndZ=0
    g2: LineSegment StartX=4 StartY=-4 StartZ=0 EndX=4 EndY=4 EndZ=0
    g3: LineSegment StartX=4 StartY=4 StartZ=0 EndX=-4 EndY=4 EndZ=0
  constraints (11):
    c: Coincident(g0,g1)
    c: Coincident(g1,g2)
    c: Coincident(g2,g3)
    c: Coincident(g3,g0)
    c: Vertical(g0)
    c: Vertical(g2)
    c: Horizontal(g1)
    c: Horizontal(g3)
    c: Symmetric(g2,g0,g-1)
    c: Equal(g3,g0)
    c: DistanceX(g3,g3) = 8
FEATURE [PartDesign::Pocket] Pocket016
  BaseFeature = -> Pad006
  Direction = (0,0,-1)
  Length = 5
  Length2 = 5
  Profile = -> Sketch024
  ReferenceAxis = -> Sketch024 [N_Axis]
  Refine = true
  Reversed = true
  SideType = 0
  Suppressed = false
  Type = 1
  Type2 = 0
FEATURE [PartDesign::Body] Body006  label="Copper Tape"
  AllowCompound = false
  Group = -> [Sketch023,Pad006,Sketch024,Pocket016]
  Origin = -> Origin038
  Placement = pos=(0,14.39,25.64) rot=(0,0,1;0rad)
  Tip = -> Pocket016
FEATURE [App::DocumentObjectGroup] Group030  label="Sample"
  Group = -> [Cylinder,Box243,Body006]
FEATURE [Part::Cylinder] Cylinder113  label="Tungsten Wire"
  Angle = 360
  AttacherType = Attacher::AttachEngine3D
  FirstAngle = 0
  Height = 3.7
  Placement = pos=(0,14.39,25.66) rot=(0,0,1;0rad)
  Radius = 0.15
  SecondAngle = 0
FEATURE [Fem::FemSolverObjectPython] SolverCcxTools  # FEM object (typed FeaturePython)
  AnalysisType = 1
  AutomaticIncrementation = true
  BeamReducedIntegration = true
  BeamShellResultOutput3D = true
  BucklingAccuracy = 0.01
  BucklingFactors = 1
  EigenmodeHighLimit = 1000000
  EigenmodeLowLimit = 10
  EigenmodesCount = 15
  ExcludeBendingStiffness = false
  GeometricalNonlinearity = 0
  IncrementsMaximum = 2000
  IterationsControlParameterCutb = 0.25,0.5,0.75,0.85,,,1.5,
  IterationsControlParameterIter = 4,8,9,200,10,400,,200,,
  IterationsControlParameterTimeUse = false
  MaterialNonlinearity = 0
  MatrixSolverType = 0
  ModelSpace = 0
  OutputFrequency = 1
  PastixMixedPrecision = false
  SplitInputWriter = false
  ThermoMechSteadyState = true
  ThermoMechType = 0
  TimeInitialIncrement = 1
  TimeMaximumIncrement = 1
  TimeMinimumIncrement = 1e-05
  TimePeriod = 1
FEATURE [App::MaterialObjectPython] MaterialSolid  # material (typed FeaturePython)
  Category = 0
  Material = AmbientColor=(0.3000, 0.3000, 0.3000, 1.0),Author=Uwe Stöhr,CardName=Aluminum-Generic,Density=2.7e-06 kg/mm^3,+17 more (map truncated)
  Suppressed = false
  UUID = 9bf060e9-1663-44a2-88e2-2ff6ee858efe
FEATURE [App::Point] Origin041  label="Origin047"
  Role = Origin
FEATURE [App::Point] Origin043  label="Origin050"
  Role = Origin
FEATURE [Sketcher::SketchObject] Sketch026
  ArcFitTolerance = 1e-06
  AttachmentSupport = -> [Origin042]
  ExternalTypes = [0]
  FullyConstrained = true
  MakeInternals = false
  MapMode = 5
  sketch-geometry (4):
    g0: LineSegment StartX=-7.65 StartY=-12.42 StartZ=0 EndX=-7.65 EndY=12.42 EndZ=0
    g1: LineSegment StartX=-7.65 StartY=12.42 StartZ=0 EndX=12.3 EndY=12.42 EndZ=0
    g2: LineSegment StartX=-7.65 StartY=-12.42 StartZ=0 EndX=12.3 EndY=-12.42 EndZ=0
    g3: LineSegment StartX=12.3 StartY=-12.42 StartZ=0 EndX=12.3 EndY=12.42 EndZ=0
  constraints (12):
    c: Vertical(g0)
    c: Coincident(g1,g0)
    c: Horizontal(g1)
    c: Coincident(g2,g0)
    c: Horizontal(g2)
    c: Coincident(g3,g2)
    c: Coincident(g3,g1)
    c: Vertical(g3)
    c: Distance(g-1,g1) = 12.42
    c: Distance(g-1,g2) = 12.42
    c: Distance(g-1,g0) = 7.65
    c: Distance(g-1,g3) = 12.3
FEATURE [PartDesign::Pad] Pad007
  Direction = (0,0,1)
  Length = 3
  Length2 = 10
  Profile = -> Sketch026
  ReferenceAxis = -> Sketch026 [N_Axis]
  Refine = true
  SideType = 0
  Suppressed = false
  Type = 0
  Type2 = 0
FEATURE [Sketcher::SketchObject] Sketch027
  ArcFitTolerance = 1e-06
  AttachmentSupport = -> [Origin042]
  ExternalTypes = [0]
  FullyConstrained = true
  MakeInternals = false
  MapMode = 5
  Placement = pos=(0,0,0) rot=(1,0,0;1.5708rad)
  sketch-geometry (3):
    g0: LineSegment StartX=-5.15 StartY=0.866025 StartZ=0 EndX=-6.65 EndY=0 EndZ=0
    g1: LineSegment StartX=-5.15 StartY=0.866025 StartZ=0 EndX=-3.65 EndY=0 EndZ=0
    g2: LineSegment StartX=-3.65 StartY=0 StartZ=0 EndX=-6.65 EndY=0 EndZ=0
  constraints (9):
    c: Coincident(g1,g0)
    c: Coincident(g2,g1)
    c: Coincident(g2,g0)
    c: PointOnObject(g1,g-1)
    c: PointOnObject(g0,g-1)
    c: Distance(g-1,g1) = 3.65
    c: Distance(g1,g0) = 3
    c: Equal(g0,g1)
    c: Angle(g0,g1) = 2.0944
FEATURE [PartDesign::Pocket] Pocket017
  BaseFeature = -> Pad007
  Direction = (0,1,-2e-16)
  Length = 5
  Length2 = 5
  Profile = -> Sketch027
  ReferenceAxis = -> Sketch027 [N_Axis]
  Refine = true
  SideType = 2
  Suppressed = false
  Type = 1
  Type2 = 0
FEATURE [Sketcher::SketchObject] Sketch028
  ArcFitTolerance = 1e-06
  AttachmentSupport = -> [Origin042]
  ExternalTypes = [0]
  FullyConstrained = true
  MakeInternals = false
  MapMode = 5
  Placement = pos=(0,0,0) rot=(1,0,0;1.5708rad)
  sketch-geometry (4):
    g0: LineSegment StartX=7.3 StartY=0.56 StartZ=0 EndX=7.3 EndY=0 EndZ=0
    g1: LineSegment StartX=7.3 StartY=0 StartZ=0 EndX=12.3 EndY=0 EndZ=0
    g2: LineSegment StartX=12.3 StartY=0 StartZ=0 EndX=12.3 EndY=0.56 EndZ=0
    g3: LineSegment StartX=12.3 StartY=0.56 StartZ=0 EndX=7.3 EndY=0.56 EndZ=0
  constraints (12):
    c: Coincident(g0,g1)
    c: Coincident(g1,g2)
    c: Coincident(g2,g3)
    c: Coincident(g3,g0)
    c: Vertical(g0)
    c: Vertical(g2)
    c: Horizontal(g1)
    c: Horizontal(g3)
    c: Distance(g-1,g0) = 7.3
    c: DistanceX(g3,g3) = 5
    c: PointOnObject(g0,g-1)
    c: DistanceY(g0,g0) = 0.56
FEATURE [PartDesign::Pocket] Pocket018
  BaseFeature = -> Pocket017
  Direction = (0,1,-2e-16)
  Length = 5
  Length2 = 5
  Profile = -> Sketch028
  ReferenceAxis = -> Sketch028 [N_Axis]
  Refine = true
  SideType = 2
  Suppressed = false
  Type = 1
  Type2 = 0
FEATURE [PartDesign::Body] Body008  label="Coarse Z Slider (Phase I)"
  AllowCompound = false
  Group = -> [Sketch026,Pad007,Sketch027,Pocket017,Sketch028,Pocket018]
  Origin = -> Origin042
  Placement = pos=(13,5.33,24.12) rot=(0,0.707107,0.707107;3.14159rad)
  Tip = -> Pocket018
FEATURE [Part::Box] Box248  label="Steel Shim Spacer016"
  AttacherType = Attacher::AttachEngine3D
  Height = 0.25
  Length = 5
  Placement = pos=(14.5,5.3e-15,21.62) rot=(0,0.707107,0.707107;3.14159rad)
  Width = 5
FEATURE [Part::Box] Box249  label="Steel Shim Spacer017"
  AttacherType = Attacher::AttachEngine3D
  Height = 0.25
  Length = 5
  Placement = pos=(14.5,1.04,21.62) rot=(0,0.707107,0.707107;3.14159rad)
  Width = 5
FEATURE [Part::Box] Box250  label="Steel Shim Spacer018"
  AttacherType = Attacher::AttachEngine3D
  Height = 0.25
  Length = 5
  Placement = pos=(14.5,2.08,21.62) rot=(0,0.707107,0.707107;3.14159rad)
  Width = 5
FEATURE [Part::Box] Box251  label="Steel Shim Spacer019"
  AttacherType = Attacher::AttachEngine3D
  Height = 0.25
  Length = 5
  Placement = pos=(14.5,3.12,21.62) rot=(0,0.707107,0.707107;3.14159rad)
  Width = 5
FEATURE [Part::Box] Box252  label="Small LiNbO3 Plate124"
  AttacherType = Attacher::AttachEngine3D
  Height = 0.5
  Length = 4.5
  Width = 5.5
FEATURE [Part::Box] Box253  label="Small Cu GND Electrode105"
  AttacherType = Attacher::AttachEngine3D
  Height = 1.15
  Length = 6
  Width = 6.5
FEATURE [Part::Box] Box254  label="Small Cu GND Electrode106"
  AttacherType = Attacher::AttachEngine3D
  Height = 1.05
  Length = 6
  Placement = pos=(0,0,0.05) rot=(0,0,1;0rad)
  Width = 6.45
FEATURE [Part::Box] Box255  label="Small LiNbO3 Plate125"
  AttacherType = Attacher::AttachEngine3D
  Height = 0.5
  Length = 4.5
  Width = 5.5
FEATURE [Part::Box] Box256  label="Small Cu GND Electrode107"
  AttacherType = Attacher::AttachEngine3D
  Height = 1.2
  Length = 5
  Width = 7.5
FEATURE [Part::Box] Box257  label="Small Cu GND Electrode108"
  AttacherType = Attacher::AttachEngine3D
  Height = 1.1
  Length = 5
  Placement = pos=(0,0,0.05) rot=(0,0,1;0rad)
  Width = 7.45
FEATURE [Part::Box] Box258  label="Small Cu GND Electrode109"
  AttacherType = Attacher::AttachEngine3D
  Height = 1.15
  Length = 6
  Width = 6.5
FEATURE [Part::Box] Box259  label="Small Cu GND Electrode110"
  AttacherType = Attacher::AttachEngine3D
  Height = 1.05
  Length = 6
  Placement = pos=(0,0,0.05) rot=(0,0,1;0rad)
  Width = 6.45
FEATURE [Part::Box] Box260  label="Small LiNbO3 Plate126"
  AttacherType = Attacher::AttachEngine3D
  Height = 0.5
  Length = 4.5
  Width = 5.5
FEATURE [Part::Box] Box261  label="Small LiNbO3 Plate127"
  AttacherType = Attacher::AttachEngine3D
  Height = 0.5
  Length = 4.5
  Width = 5.5
FEATURE [Part::Box] Box262  label="Cube022"
  AttacherType = Attacher::AttachEngine3D
  Height = 10
  Length = 10
  Placement = pos=(-5,-5,-10) rot=(0,0,1;0rad)
  Width = 10
FEATURE [Part::Box] Box263  label="Small LiNbO3 Plate128"
  AttacherType = Attacher::AttachEngine3D
  Height = 0.5
  Length = 4.5
  Width = 5.5
FEATURE [Part::Box] Box264  label="Small Cu GND Electrode111"
  AttacherType = Attacher::AttachEngine3D
  Height = 1.15
  Length = 6
  Width = 6.5
FEATURE [Part::Box] Box265  label="Small Cu GND Electrode112"
  AttacherType = Attacher::AttachEngine3D
  Height = 1.05
  Length = 6
  Placement = pos=(0,0,0.05) rot=(0,0,1;0rad)
  Width = 6.45
FEATURE [Part::Box] Box266  label="Small LiNbO3 Plate129"
  AttacherType = Attacher::AttachEngine3D
  Height = 0.5
  Length = 4.5
  Width = 5.5
FEATURE [Part::Box] Box267  label="Small Cu GND Electrode113"
  AttacherType = Attacher::AttachEngine3D
  Height = 1.2
  Length = 5
  Width = 7.5
FEATURE [Part::Box] Box268  label="Small Cu GND Electrode114"
  AttacherType = Attacher::AttachEngine3D
  Height = 1.1
  Length = 5
  Placement = pos=(0,0,0.05) rot=(0,0,1;0rad)
  Width = 7.45
FEATURE [Part::Box] Box269  label="Small Cu GND Electrode115"
  AttacherType = Attacher::AttachEngine3D
  Height = 1.15
  Length = 6
  Width = 6.5
FEATURE [Part::Box] Box270  label="Small Cu GND Electrode116"
  AttacherType = Attacher::AttachEngine3D
  Height = 1.05
  Length = 6
  Placement = pos=(0,0,0.05) rot=(0,0,1;0rad)
  Width = 6.45
FEATURE [Part::Box] Box271  label="Small LiNbO3 Plate130"
  AttacherType = Attacher::AttachEngine3D
  Height = 0.5
  Length = 4.5
  Width = 5.5
FEATURE [Part::Box] Box272  label="Small LiNbO3 Plate131"
  AttacherType = Attacher::AttachEngine3D
  Height = 0.5
  Length = 4.5
  Width = 5.5
FEATURE [Part::Box] Box273  label="Cube023"
  AttacherType = Attacher::AttachEngine3D
  Height = 10
  Length = 10
  Placement = pos=(-5,-5,-10) rot=(0,0,1;0rad)
  Width = 10
FEATURE [Part::Box] Box274  label="Small LiNbO3 Plate132"
  AttacherType = Attacher::AttachEngine3D
  Height = 0.5
  Length = 4.5
  Width = 5.5
FEATURE [Part::Box] Box275  label="Small Cu GND Electrode117"
  AttacherType = Attacher::AttachEngine3D
  Height = 1.15
  Length = 6
  Width = 6.5
FEATURE [Part::Box] Box276  label="Small Cu GND Electrode118"
  AttacherType = Attacher::AttachEngine3D
  Height = 1.05
  Length = 6
  Placement = pos=(0,0,0.05) rot=(0,0,1;0rad)
  Width = 6.45
FEATURE [Part::Box] Box277  label="Small LiNbO3 Plate133"
  AttacherType = Attacher::AttachEngine3D
  Height = 0.5
  Length = 4.5
  Width = 5.5
FEATURE [Part::Box] Box278  label="Small Cu GND Electrode119"
  AttacherType = Attacher::AttachEngine3D
  Height = 1.2
  Length = 5
  Width = 7.5
FEATURE [Part::Box] Box279  label="Small Cu GND Electrode120"
  AttacherType = Attacher::AttachEngine3D
  Height = 1.1
  Length = 5
  Placement = pos=(0,0,0.05) rot=(0,0,1;0rad)
  Width = 7.45
FEATURE [Part::Box] Box280  label="Small Cu GND Electrode121"
  AttacherType = Attacher::AttachEngine3D
  Height = 1.15
  Length = 6
  Width = 6.5
FEATURE [Part::Box] Box281  label="Small Cu GND Electrode122"
  AttacherType = Attacher::AttachEngine3D
  Height = 1.05
  Length = 6
  Placement = pos=(0,0,0.05) rot=(0,0,1;0rad)
  Width = 6.45
FEATURE [Part::Box] Box282  label="Small LiNbO3 Plate134"
  AttacherType = Attacher::AttachEngine3D
  Height = 0.5
  Length = 4.5
  Width = 5.5
FEATURE [Part::Box] Box283  label="Small LiNbO3 Plate135"
  AttacherType = Attacher::AttachEngine3D
  Height = 0.5
  Length = 4.5
  Width = 5.5
FEATURE [Part::Box] Box284  label="Cube024"
  AttacherType = Attacher::AttachEngine3D
  Height = 10
  Length = 10
  Placement = pos=(-5,-5,-10) rot=(0,0,1;0rad)
  Width = 10
FEATURE [Part::Cut] Cut132  label="Small Cu Electrode, Short Axis, GND014"
  Base = -> Box253
  Placement = pos=(18.25,1.59,19.5311) rot=(-0.787007,0.436245,0.436245;1.80806rad)
  Refine = true
  Tool = -> Box254
FEATURE [Part::Cut] Cut134  label="Small Cu Electrode001, Long Axis, V014"
  Base = -> Box256
  Placement = pos=(21.4296,2.14,14.4429) rot=(0.198716,-0.693005,-0.693005;3.53391rad)
  Refine = true
  Tool = -> Box257
FEATURE [Part::Cut] Cut135  label="Small Cu Electrode002, Short Axis, GND014"
  Base = -> Box258
  Placement = pos=(18.25,2.74,19.5311) rot=(-0.787007,0.436245,0.436245;1.80806rad)
  Refine = true
  Tool = -> Box259
FEATURE [Part::Cut] Cut140  label="Small Cu Electrode, Short Axis, GND015"
  Base = -> Box264
  Placement = pos=(18.25,1.59,37.3711) rot=(-0.787007,0.436245,0.436245;1.80806rad)
  Refine = true
  Tool = -> Box265
FEATURE [Part::Cut] Cut142  label="Small Cu Electrode001, Long Axis, V015"
  Base = -> Box267
  Placement = pos=(21.4296,2.14,32.2829) rot=(0.198716,-0.693005,-0.693005;3.53391rad)
  Refine = true
  Tool = -> Box268
FEATURE [Part::Cut] Cut143  label="Small Cu Electrode002, Short Axis, GND015"
  Base = -> Box269
  Placement = pos=(18.25,2.74,37.3711) rot=(-0.787007,0.436245,0.436245;1.80806rad)
  Refine = true
  Tool = -> Box270
FEATURE [Part::Cut] Cut148  label="Small Cu Electrode, Short Axis, GND016"
  Base = -> Box275
  Placement = pos=(2.80005,1.59,28.4511) rot=(-0.787007,0.436245,0.436245;1.80806rad)
  Refine = true
  Tool = -> Box276
FEATURE [Part::Cut] Cut150  label="Small Cu Electrode001, Long Axis, V016"
  Base = -> Box278
  Placement = pos=(5.97956,2.14,23.3629) rot=(0.198716,-0.693005,-0.693005;3.53391rad)
  Refine = true
  Tool = -> Box279
FEATURE [Part::Cut] Cut151  label="Small Cu Electrode002, Short Axis, GND016"
  Base = -> Box280
  Placement = pos=(2.80005,2.74,28.4511) rot=(-0.787007,0.436245,0.436245;1.80806rad)
  Refine = true
  Tool = -> Box281
FEATURE [Part::Cylinder] Cylinder114  label="KJ_D401_017"
  Angle = 360
  AttacherType = Attacher::AttachEngine3D
  FirstAngle = 0
  Height = 0.79
  Placement = pos=(12,0.25,24.12) rot=(0,0.707107,0.707107;3.14159rad)
  Radius = 3.18
  SecondAngle = 0
FEATURE [Part::Cylinder] Cylinder115  label="KJ_D401_018"
  Angle = 360
  AttacherType = Attacher::AttachEngine3D
  FirstAngle = 0
  Height = 0.79
  Placement = pos=(12,1.29,24.12) rot=(0,0.707107,0.707107;3.14159rad)
  Radius = 3.18
  SecondAngle = 0
FEATURE [Part::Cylinder] Cylinder116  label="KJ_D401_019"
  Angle = 360
  AttacherType = Attacher::AttachEngine3D
  FirstAngle = 0
  Height = 0.79
  Placement = pos=(12,2.33,24.12) rot=(0,0.707107,0.707107;3.14159rad)
  Radius = 3.18
  SecondAngle = 0
FEATURE [Part::Cylinder] Cylinder117  label="KJ_D401_020"
  Angle = 360
  AttacherType = Attacher::AttachEngine3D
  FirstAngle = 0
  Height = 0.79
  Placement = pos=(12,3.37,24.12) rot=(0,0.707107,0.707107;3.14159rad)
  Radius = 3.18
  SecondAngle = 0
FEATURE [Part::Cylinder] Cylinder118  label="KJ_D31SH014"
  Angle = 360
  AttacherType = Attacher::AttachEngine3D
  FirstAngle = 0
  Height = 1.59
  Placement = pos=(18.15,7.1e-15,15.2) rot=(0.198716,-0.693005,-0.693005;3.53391rad)
  Radius = 2.38
  SecondAngle = 0
FEATURE [Part::Cylinder] Cylinder119
  Angle = 360
  AttacherType = Attacher::AttachEngine3D
  FirstAngle = 0
  Height = 0.01
  Placement = pos=(1,4.5,0.49) rot=(0,0,1;0rad)
  Radius = 0.5
  SecondAngle = 0
FEATURE [Part::Cut] Cut131  label="Small LiNbO3 Plate136"
  Base = -> Box252
  Placement = pos=(21.4296,1.64,14.4429) rot=(0.198716,-0.693005,-0.693005;3.53391rad)
  Refine = true
  Tool = -> Cylinder119
FEATURE [Part::Cylinder] Cylinder120
  Angle = 360
  AttacherType = Attacher::AttachEngine3D
  FirstAngle = 0
  Height = 0.01
  Placement = pos=(1,4.5,0.49) rot=(0,0,1;0rad)
  Radius = 0.5
  SecondAngle = 0
FEATURE [Part::Cut] Cut133  label="Small LiNbO3 Plate137"
  Base = -> Box255
  Placement = pos=(14.6988,2.19,16.7225) rot=(-0.926703,-0.265728,-0.265728;1.64685rad)
  Refine = true
  Tool = -> Cylinder120
FEATURE [Part::Cylinder] Cylinder121
  Angle = 360
  AttacherType = Attacher::AttachEngine3D
  FirstAngle = 0
  Height = 0.01
  Placement = pos=(1,4.5,0.49) rot=(0,0,1;0rad)
  Radius = 0.5
  SecondAngle = 0
FEATURE [Part::Cut] Cut136  label="Small LiNbO3 Plate138"
  Base = -> Box260
  Placement = pos=(21.4296,2.79,14.4429) rot=(0.198716,-0.693005,-0.693005;3.53391rad)
  Refine = true
  Tool = -> Cylinder121
FEATURE [Part::Cylinder] Cylinder122
  Angle = 360
  AttacherType = Attacher::AttachEngine3D
  FirstAngle = 0
  Height = 0.01
  Placement = pos=(1,4.5,0.49) rot=(0,0,1;0rad)
  Radius = 0.5
  SecondAngle = 0
FEATURE [Part::Cut] Cut137  label="Small LiNbO3 Plate139"
  Base = -> Box261
  Placement = pos=(14.6988,3.34,16.7225) rot=(-0.926703,-0.265728,-0.265728;1.64685rad)
  Refine = true
  Tool = -> Cylinder122
FEATURE [Part::Cylinder] Cylinder123  label="KJ_D31SH015"
  Angle = 360
  AttacherType = Attacher::AttachEngine3D
  FirstAngle = 0
  Height = 1.59
  Placement = pos=(18.15,1.8e-15,33.04) rot=(0.198716,-0.693005,-0.693005;3.53391rad)
  Radius = 2.38
  SecondAngle = 0
FEATURE [Part::Cylinder] Cylinder124
  Angle = 360
  AttacherType = Attacher::AttachEngine3D
  FirstAngle = 0
  Height = 0.01
  Placement = pos=(1,4.5,0.49) rot=(0,0,1;0rad)
  Radius = 0.5
  SecondAngle = 0
FEATURE [Part::Cut] Cut139  label="Small LiNbO3 Plate140"
  Base = -> Box263
  Placement = pos=(21.4296,1.64,32.2829) rot=(0.198716,-0.693005,-0.693005;3.53391rad)
  Refine = true
  Tool = -> Cylinder124
FEATURE [Part::Cylinder] Cylinder125
  Angle = 360
  AttacherType = Attacher::AttachEngine3D
  FirstAngle = 0
  Height = 0.01
  Placement = pos=(1,4.5,0.49) rot=(0,0,1;0rad)
  Radius = 0.5
  SecondAngle = 0
FEATURE [Part::Cut] Cut141  label="Small LiNbO3 Plate141"
  Base = -> Box266
  Placement = pos=(14.6988,2.19,34.5625) rot=(-0.926703,-0.265728,-0.265728;1.64685rad)
  Refine = true
  Tool = -> Cylinder125
FEATURE [Part::Cylinder] Cylinder126
  Angle = 360
  AttacherType = Attacher::AttachEngine3D
  FirstAngle = 0
  Height = 0.01
  Placement = pos=(1,4.5,0.49) rot=(0,0,1;0rad)
  Radius = 0.5
  SecondAngle = 0
FEATURE [Part::Cut] Cut144  label="Small LiNbO3 Plate142"
  Base = -> Box271
  Placement = pos=(21.4296,2.79,32.2829) rot=(0.198716,-0.693005,-0.693005;3.53391rad)
  Refine = true
  Tool = -> Cylinder126
FEATURE [Part::Cylinder] Cylinder127
  Angle = 360
  AttacherType = Attacher::AttachEngine3D
  FirstAngle = 0
  Height = 0.01
  Placement = pos=(1,4.5,0.49) rot=(0,0,1;0rad)
  Radius = 0.5
  SecondAngle = 0
FEATURE [Part::Cut] Cut145  label="Small LiNbO3 Plate143"
  Base = -> Box272
  Placement = pos=(14.6988,3.34,34.5625) rot=(-0.926703,-0.265728,-0.265728;1.64685rad)
  Refine = true
  Tool = -> Cylinder127
FEATURE [Part::Cylinder] Cylinder128  label="KJ_D31SH016"
  Angle = 360
  AttacherType = Attacher::AttachEngine3D
  FirstAngle = 0
  Height = 1.59
  Placement = pos=(2.7,3.6e-15,24.12) rot=(0.198716,-0.693005,-0.693005;3.53391rad)
  Radius = 2.38
  SecondAngle = 0
FEATURE [Part::Cylinder] Cylinder129
  Angle = 360
  AttacherType = Attacher::AttachEngine3D
  FirstAngle = 0
  Height = 0.01
  Placement = pos=(1,4.5,0.49) rot=(0,0,1;0rad)
  Radius = 0.5
  SecondAngle = 0
FEATURE [Part::Cut] Cut147  label="Small LiNbO3 Plate144"
  Base = -> Box274
  Placement = pos=(5.97956,1.64,23.3629) rot=(0.198716,-0.693005,-0.693005;3.53391rad)
  Refine = true
  Tool = -> Cylinder129
FEATURE [Part::Cylinder] Cylinder130
  Angle = 360
  AttacherType = Attacher::AttachEngine3D
  FirstAngle = 0
  Height = 0.01
  Placement = pos=(1,4.5,0.49) rot=(0,0,1;0rad)
  Radius = 0.5
  SecondAngle = 0
FEATURE [Part::Cut] Cut149  label="Small LiNbO3 Plate145"
  Base = -> Box277
  Placement = pos=(-0.75121,2.19,25.6425) rot=(-0.926703,-0.265728,-0.265728;1.64685rad)
  Refine = true
  Tool = -> Cylinder130
FEATURE [Part::Cylinder] Cylinder131
  Angle = 360
  AttacherType = Attacher::AttachEngine3D
  FirstAngle = 0
  Height = 0.01
  Placement = pos=(1,4.5,0.49) rot=(0,0,1;0rad)
  Radius = 0.5
  SecondAngle = 0
FEATURE [Part::Cut] Cut152  label="Small LiNbO3 Plate146"
  Base = -> Box282
  Placement = pos=(5.97956,2.79,23.3629) rot=(0.198716,-0.693005,-0.693005;3.53391rad)
  Refine = true
  Tool = -> Cylinder131
FEATURE [Part::Cylinder] Cylinder132
  Angle = 360
  AttacherType = Attacher::AttachEngine3D
  FirstAngle = 0
  Height = 0.01
  Placement = pos=(1,4.5,0.49) rot=(0,0,1;0rad)
  Radius = 0.5
  SecondAngle = 0
FEATURE [Part::Cut] Cut153  label="Small LiNbO3 Plate147"
  Base = -> Box283
  Placement = pos=(-0.75121,3.34,25.6425) rot=(-0.926703,-0.265728,-0.265728;1.64685rad)
  Refine = true
  Tool = -> Cylinder132
FEATURE [App::DocumentObjectGroup] Group031  label="Magnet Stack004"
  Group = -> [Box248,Cylinder114,Box249,Cylinder115,Box250,Cylinder116,Box251,Cylinder117]
FEATURE [Part::Sphere] Sphere018
  Angle1 = -90
  Angle2 = 90
  Angle3 = 360
  AttacherType = Attacher::AttachEngine3D
  Radius = 2
FEATURE [Part::Cut] Cut138  label="Sapphire Half-Ball Lens018"
  Base = -> Sphere018
  Placement = pos=(18.15,3.89,15.2) rot=(0.198716,-0.693005,-0.693005;3.53391rad)
  Refine = true
  Tool = -> Box262
FEATURE [App::DocumentObjectGroup] Group032  label="Coarse Piezo Stack, Rotated013"
  Group = -> [Cylinder118,Cut132,Cut131,Cut134,Cut133,Cut135,Cut136,Cut137,Cut138]
FEATURE [Part::Sphere] Sphere019
  Angle1 = -90
  Angle2 = 90
  Angle3 = 360
  AttacherType = Attacher::AttachEngine3D
  Radius = 2
FEATURE [Part::Cut] Cut146  label="Sapphire Half-Ball Lens019"
  Base = -> Sphere019
  Placement = pos=(18.15,3.89,33.04) rot=(0.198716,-0.693005,-0.693005;3.53391rad)
  Refine = true
  Tool = -> Box273
FEATURE [App::DocumentObjectGroup] Group033  label="Coarse Piezo Stack, Rotated014"
  Group = -> [Cylinder123,Cut140,Cut139,Cut142,Cut141,Cut143,Cut144,Cut145,Cut146]
FEATURE [Part::Sphere] Sphere020
  Angle1 = -90
  Angle2 = 90
  Angle3 = 360
  AttacherType = Attacher::AttachEngine3D
  Radius = 2
FEATURE [Part::Cut] Cut154  label="Sapphire Half-Ball Lens020"
  Base = -> Sphere020
  Placement = pos=(2.7,3.89,24.12) rot=(0.198716,-0.693005,-0.693005;3.53391rad)
  Refine = true
  Tool = -> Box284
FEATURE [App::DocumentObjectGroup] Group034  label="Coarse Piezo Stack, Rotated015"
  Group = -> [Cylinder128,Cut148,Cut147,Cut150,Cut149,Cut151,Cut152,Cut153,Cut154]
FEATURE [App::DocumentObjectGroup] Group035  label="Coarse Z Piezo Tripod (Phase I)"
  Group = -> [Group032,Group033,Group034,Group031]
FEATURE [Part::Box] Box287  label="Copper Shim"
  AttacherType = Attacher::AttachEngine3D
  Height = 0.41
  Length = 5.5
  Placement = pos=(12.25,0.5,19.79) rot=(1,0,0;4.71239rad)
  Width = 5.5
FEATURE [Part::Cylinder] Cylinder133  label="KJ_D31SH017"
  Angle = 360
  AttacherType = Attacher::AttachEngine3D
  FirstAngle = 0
  Height = 1.59
  Placement = pos=(15,0.91,17.04) rot=(1,0,0;4.71239rad)
  Radius = 2.38
  SecondAngle = 0
FEATURE [Part::Box] Box288  label="Copper Shim001"
  AttacherType = Attacher::AttachEngine3D
  Height = 0.05
  Length = 12
  Placement = pos=(10,2.5,12.04) rot=(-0.57735,-0.57735,-0.57735;2.0944rad)
  Width = 12
FEATURE [Part::Box] Box289  label="Glass Cover Slip002"
  AttacherType = Attacher::AttachEngine3D
  Height = 0.15
  Length = 12
  Placement = pos=(10,2.55,12.04) rot=(-0.57735,-0.57735,-0.57735;2.0944rad)
  Width = 12
FEATURE [Part::Box] Box290  label="Glass Cover Slip003"
  AttacherType = Attacher::AttachEngine3D
  Height = 0.15
  Length = 12
  Placement = pos=(10,2.7,12.04) rot=(-0.57735,-0.57735,-0.57735;2.0944rad)
  Width = 12
FEATURE [Part::Box] Box291  label="Glass Cover Slip004"
  AttacherType = Attacher::AttachEngine3D
  Height = 0.15
  Length = 12
  Placement = pos=(10,2.85,12.04) rot=(-0.57735,-0.57735,-0.57735;2.0944rad)
  Width = 12
FEATURE [Part::Box] Box292  label="Glass Cover Slip005"
  AttacherType = Attacher::AttachEngine3D
  Height = 0.15
  Length = 12
  Placement = pos=(10,3,12.04) rot=(-0.57735,-0.57735,-0.57735;2.0944rad)
  Width = 12
FEATURE [Part::Box] Box293  label="Steel Cube001"
  AttacherType = Attacher::AttachEngine3D
  Height = 10
  Length = 10
  Placement = pos=(10,3.15,12.04) rot=(-0.57735,-0.57735,-0.57735;2.0944rad)
  Width = 10
FEATURE [App::DocumentObjectGroup] Group036  label="Moving Capacitance Probe (Phase 0.2)"
  Group = -> [Box288,Box289,Box290,Box291,Box292,Box293]
FEATURE [App::DocumentObjectGroup] Group037  label="Capacitance Probe Extender, Small (Phase 0.2)"
  Group = -> [Box287,Cylinder133]
FEATURE [Part::Box] Box294  label="Copper Shim002"
  AttacherType = Attacher::AttachEngine3D
  Height = 0.41
  Length = 11
  Placement = pos=(9.5,0.5,22.54) rot=(1,0,0;4.71239rad)
  Width = 11
FEATURE [Part::Cylinder] Cylinder134  label="KJ_D61SH002"
  Angle = 360
  AttacherType = Attacher::AttachEngine3D
  FirstAngle = 0
  Height = 1.59
  Placement = pos=(15,0.91,17.04) rot=(1,0,0;4.71239rad)
  Radius = 4.76
  SecondAngle = 0
FEATURE [App::DocumentObjectGroup] Group038  label="Capacitance Probe Extender, Large (Phase 0.2)"
  Group = -> [Box294,Cylinder134]
FEATURE [Part::Cylinder] Cylinder135  label="KJ_D61SH003"
  Angle = 360
  AttacherType = Attacher::AttachEngine3D
  FirstAngle = 0
  Height = 1.59
  Placement = pos=(15,8.15,0) rot=(0,0,1;0rad)
  Radius = 4.76
  SecondAngle = 0
FEATURE [Part::Box] Box295  label="Copper Cube"
  AttacherType = Attacher::AttachEngine3D
  Height = 10
  Length = 10
  Placement = pos=(10,3.15,1.74) rot=(0,0,1;0rad)
  Width = 10
FEATURE [Part::Box] Box296  label="Glass Cover Slip006"
  AttacherType = Attacher::AttachEngine3D
  Height = 0.15
  Length = 12
  Placement = pos=(10,3.15,1.59) rot=(0,0,1;0rad)
  Width = 12
FEATURE [App::DocumentObjectGroup] Group039  label="Stationary Capacitance Probe (Phase 0.2)"
  Group = -> [Cylinder135,Box296,Box295]
FEATURE [Sketcher::SketchObject] Sketch029
  ArcFitTolerance = 1e-06
  AttachmentSupport = -> [Origin040]
  ExternalTypes = [0]
  FullyConstrained = true
  MakeInternals = false
  MapMode = 5
  Placement = pos=(0,0,0) rot=(0.57735,0.57735,0.57735;2.0944rad)
  sketch-geometry (10):
    g0: LineSegment StartX=0 StartY=60 StartZ=0 EndX=-15 EndY=60 EndZ=0
    g1: LineSegment StartX=-15 StartY=60 StartZ=0 EndX=-15 EndY=-25 EndZ=0
    g2: LineSegment StartX=-15 StartY=-25 StartZ=0 EndX=25 EndY=-25 EndZ=0
    g3: LineSegment StartX=30 StartY=0 StartZ=0 EndX=-6 EndY=0 EndZ=0
    g4: LineSegment StartX=-6 StartY=0 StartZ=0 EndX=-6 EndY=10.66 EndZ=0
    g5: LineSegment StartX=-6 StartY=10.66 StartZ=0 EndX=0 EndY=10.66 EndZ=0
    g6: LineSegment StartX=0 StartY=10.66 StartZ=0 EndX=0 EndY=60 EndZ=0
    g7: LineSegment StartX=25 StartY=-25 StartZ=0 EndX=25 EndY=-5 EndZ=0
    g8: LineSegment StartX=25 StartY=-5 StartZ=0 EndX=30 EndY=-5 EndZ=0
    g9: LineSegment StartX=30 StartY=-5 StartZ=0 EndX=30 EndY=0 EndZ=0
  constraints (30):
    c: PointOnObject(g0,g-2)
    c: Horizontal(g0)
    c: Coincident(g1,g0)
    c: Vertical(g1)
    c: Coincident(g2,g1)
    c: Horizontal(g2)
    c: PointOnObject(g3,g-1)
    c: PointOnObject(g3,g-1)
    c: Coincident(g4,g3)
    c: Vertical(g4)
    c: Coincident(g5,g4)
    c: PointOnObject(g5,g-2)
    c: Horizontal(g5)
    c: Coincident(g6,g5)
    c: Coincident(g6,g0)
    c: Distance(g-1,g0) = 60
    c: DistanceY(g2,g3) = 25
    c: DistanceX(g0,g0) = 15
    c: DistanceY(g4,g4) = 10.66
    c: Distance(g-1,g4) = 6
    c: Coincident(g7,g2)
    c: Vertical(g7)
    c: Coincident(g8,g7)
    c: Horizontal(g8)
    c: Coincident(g9,g8)
    c: Coincident(g9,g3)
    c: Vertical(g9)
    c: Distance(g-1,g9) = 30
    c: Distance(g-1,g7) = 25
    c: Distance(g9,g9) = 5
FEATURE [PartDesign::Pad] Pad008
  Direction = (1,0,0)
  Length = 26
  Length2 = 14
  Profile = -> Sketch029
  ReferenceAxis = -> Sketch029 [N_Axis]
  Refine = true
  SideType = 1
  Suppressed = false
  Type = 0
  Type2 = 0
FEATURE [Sketcher::SketchObject] Sketch030
  ArcFitTolerance = 1e-06
  AttachmentSupport = -> [Origin040]
  ExternalTypes = [0]
  FullyConstrained = true
  MakeInternals = false
  MapMode = 5
  Placement = pos=(0,0,0) rot=(1,0,0;1.5708rad)
  sketch-geometry (10):
    g0: LineSegment [constr] StartX=3.35 StartY=13.66 StartZ=0 EndX=3.35 EndY=16.66 EndZ=0
    g1: LineSegment [constr] StartX=3.35 StartY=16.66 StartZ=0 EndX=-13.65 EndY=16.66 EndZ=0
    g2: LineSegment [constr] StartX=-13.65 StartY=16.66 StartZ=0 EndX=-13.65 EndY=13.66 EndZ=0
    g3: LineSegment [constr] StartX=-13.65 StartY=13.66 StartZ=0 EndX=3.35 EndY=13.66 EndZ=0
    g4: ArcOfCircle CenterX=3.35 CenterY=16.66 CenterZ=0 NormalX=0 NormalY=0 NormalZ=1 AngleXU=0 Radius=3 StartAngle=1e-16 EndAngle=1.5708
    g5: ArcOfCircle CenterX=3.35 CenterY=13.66 CenterZ=0 NormalX=0 NormalY=0 NormalZ=1 AngleXU=0 Radius=3 StartAngle=4.71239 EndAngle=6.28319
    g6: LineSegment StartX=6.35 StartY=16.66 StartZ=0 EndX=6.35 EndY=13.66 EndZ=0
    g7: LineSegment StartX=3.35 StartY=19.66 StartZ=0 EndX=-20 EndY=19.66 EndZ=0
    g8: LineSegment StartX=3.35 StartY=10.66 StartZ=0 EndX=-20 EndY=10.66 EndZ=0
    g9: LineSegment StartX=-20 StartY=10.66 StartZ=0 EndX=-20 EndY=19.66 EndZ=0
  constraints (26):
    c: Coincident(g0,g1)
    c: Coincident(g1,g2)
    c: Coincident(g2,g3)
    c: Coincident(g3,g0)
    c: Vertical(g0)
    c: Vertical(g2)
    c: Horizontal(g1)
    c: Horizontal(g3)
    c: Distance(g-1,g0) = 3.35
    c: Distance(g-1,g2) = 13.65
    c: Distance(g-1,g3) = 13.66
    c: Distance(g-1,g1) = 16.66
    c: Coincident(g4,g0)
    c: Coincident(g5,g0)
    c: Vertical(g6)
    c: Horizontal(g7)
    c: Horizontal(g8)
    c: Coincident(g9,g8)
    c: Coincident(g9,g7)
    c: Vertical(g9)
    c: Tangent(g4,g6) = 1.5708
    c: Tangent(g5,g6) = 1.5708
    c: Tangent(g4,g7) = -1.5708
    c: Tangent(g5,g8) = 1.5708
    c: Distance(g-1,g9) = 20
    c: Radius(g4) = 3
FEATURE [PartDesign::Pocket] Pocket019
  BaseFeature = -> Pad008
  Direction = (0,1,-2e-16)
  Length = 10
  Length2 = 5
  Profile = -> Sketch030
  ReferenceAxis = -> Sketch030 [N_Axis]
  Refine = true
  Reversed = true
  SideType = 0
  Suppressed = false
  Type = 0
  Type2 = 0
FEATURE [Sketcher::SketchObject] Sketch031
  ArcFitTolerance = 1e-06
  AttachmentSupport = -> [Origin040]
  ExternalTypes = [0]
  FullyConstrained = true
  MakeInternals = false
  MapMode = 5
  Placement = pos=(0,0,0) rot=(1,0,0;1.5708rad)
  sketch-geometry (9):
    g0: LineSegment [constr] StartX=3.35 StartY=13.66 StartZ=0 EndX=3.35 EndY=16.66 EndZ=0
    g1: LineSegment [constr] StartX=3.35 StartY=16.66 StartZ=0 EndX=-13.65 EndY=16.66 EndZ=0
    g2: LineSegment [constr] StartX=-13.65 StartY=16.66 StartZ=0 EndX=-13.65 EndY=13.66 EndZ=0
    g3: LineSegment [constr] StartX=-13.65 StartY=13.66 StartZ=0 EndX=3.35 EndY=13.66 EndZ=0
    g4: ArcOfCircle CenterX=3.35 CenterY=16.66 CenterZ=0 NormalX=0 NormalY=0 NormalZ=1 AngleXU=0 Radius=3 StartAngle=5e-16 EndAngle=1.5708
    g5: LineSegment StartX=6.35 StartY=16.66 StartZ=0 EndX=6.35 EndY=10.66 EndZ=0
    g6: LineSegment StartX=3.35 StartY=19.66 StartZ=0 EndX=-20 EndY=19.66 EndZ=0
    g7: LineSegment StartX=6.35 StartY=10.66 StartZ=0 EndX=-20 EndY=10.66 EndZ=0
    g8: LineSegment StartX=-20 StartY=10.66 StartZ=0 EndX=-20 EndY=19.66 EndZ=0
  constraints (25):
    c: Coincident(g0,g1)
    c: Coincident(g1,g2)
    c: Coincident(g2,g3)
    c: Coincident(g3,g0)
    c: Vertical(g0)
    c: Vertical(g2)
    c: Horizontal(g1)
    c: Horizontal(g3)
    c: Distance(g-1,g0) = 3.35
    c: Distance(g-1,g2) = 13.65
    c: Distance(g-1,g3) = 13.66
    c: Distance(g-1,g1) = 16.66
    c: Coincident(g4,g0)
    c: Vertical(g5)
    c: Horizontal(g6)
    c: Horizontal(g7)
    c: Coincident(g8,g7)
    c: Coincident(g8,g6)
    c: Vertical(g8)
    c: Tangent(g4,g5) = 1.5708
    c: Tangent(g4,g6) = -1.5708
    c: Distance(g-1,g8) = 20
    c: Radius(g4) = 3
    c: Coincident(g5,g7)
    c: Distance(g0,g7) = 3
FEATURE [PartDesign::Pocket] Pocket020
  BaseFeature = -> Pocket019
  Direction = (0,1,-2e-16)
  Length = 6
  Length2 = 5
  Profile = -> Sketch031
  ReferenceAxis = -> Sketch031 [N_Axis]
  Refine = true
  Reversed = true
  SideType = 0
  Suppressed = false
  Type = 0
  Type2 = 0
FEATURE [PartDesign::Body] Body007  label="STM Base"
  AllowCompound = false
  Group = -> [Sketch029,Pad008,Sketch030,Pocket019,Sketch031,Pocket020]
  Origin = -> Origin040
  Tip = -> Pocket020
FEATURE [Part::Box] Box297  label="Copper Cube001"
  AttacherType = Attacher::AttachEngine3D
  Height = 10
  Length = 10
  Placement = pos=(10,9.92,1.74) rot=(0,0,1;0rad)
  Width = 10
FEATURE [Part::Box] Box298  label="Glass Cover Slip007"
  AttacherType = Attacher::AttachEngine3D
  Height = 0.15
  Length = 12
  Placement = pos=(10,9.92,1.59) rot=(0,0,1;0rad)
  Width = 12
FEATURE [Part::Cylinder] Cylinder136  label="KJ_D61SH004"
  Angle = 360
  AttacherType = Attacher::AttachEngine3D
  FirstAngle = 0
  Height = 1.59
  Placement = pos=(15,14.92,0) rot=(0,0,1;0rad)
  Radius = 4.76
  SecondAngle = 0
FEATURE [App::DocumentObjectGroup] Group040  label="Stationary Capacitance Probe (Phase I)"
  Group = -> [Cylinder136,Box298,Box297]
FEATURE [Part::Box] Box299  label="Steel Cube004"
  AttacherType = Attacher::AttachEngine3D
  Height = 10
  Length = 10
  Placement = pos=(10,9.92,22.04) rot=(1,0,0;4.71239rad)
  Width = 10
FEATURE [Part::Cylinder] Cylinder137  label="KJ_D61SH005"
  Angle = 360
  AttacherType = Attacher::AttachEngine3D
  FirstAngle = 0
  Height = 1.59
  Placement = pos=(15,8.33,17.04) rot=(1,0,0;4.71239rad)
  Radius = 4.76
  SecondAngle = 0
FEATURE [App::DocumentObjectGroup] Group041  label="Moving Capacitance Probe (Phase I)"
  Group = -> [Cylinder137,Box299]
FEATURE [Fem::FemMeshShapeBaseObjectPython] FEMMeshGmsh  label="FEMMeshGmsh001"  # FEM object (typed FeaturePython)
  Algorithm2D = 0
  Algorithm3D = 0
  CharacteristicLengthMax = 0
  CharacteristicLengthMin = 0
  CoherenceMesh = true
  ElementDimension = 0
  ElementOrder = 1
  GeometryTolerance = 1e-06
  GroupsOfNodes = true
  HighOrderOptimize = 0
  MeshSizeFromCurvature = 12
  OptimizeNetgen = false
  OptimizeStd = true
  RecombinationAlgorithm = 0
  Recombine3DAll = false
  RecombineAll = false
  SecondOrderLinear = false
  Shape = -> Body007
  SubdivisionAlgorithm = 0
  Suppressed = false
FEATURE [Fem::ConstraintFixed] ConstraintFixed
  NormalDirection = (0,-1,0)
  Normals = (20) [(0,-1,0),(0,-1,0),(0,-1,0),(0,-1,0),(0,-1,0),(0,-1,0),(0,-1,0),(0,-1,0),(0,-1,0),(0,-1,0),(0,-1,0),(0,-1,0),(0,-1,0),(0,-1,0),(0,-1,0),(0,-1,0),+4 more]
  Points = (20) [(-14,-15,60),(-14,-15,38.75),(-14,-15,17.5),(-14,-15,-3.75),(-14,-15,-25),(-0.666667,-15,60),(-0.666667,-15,38.75),(-0.666667,-15,17.5),+12 more]
  References = -> [Pocket020]
  Suppressed = false
FEATURE [Fem::ConstraintFixed] ConstraintFixed001
  NormalDirection = (0,0,-1)
  Normals = (16) [(0,0,-1),(0,0,-1),(0,0,-1),(0,0,-1),(0,0,-1),(0,0,-1),(0,0,-1),(0,0,-1),(0,0,-1),(0,0,-1),(0,0,-1),(0,0,-1),(0,0,-1),(0,0,-1),(0,0,-1),(0,0,-1)]
  Points = (16) [(-14,-15,-25),(-14,-1.66667,-25),(-14,11.6667,-25),(-14,25,-25),(-0.666667,-15,-25),(-0.666667,-1.66667,-25),(-0.666667,11.6667,-25),+9 more]
  References = -> [Pocket020]
  Suppressed = true
FEATURE [Fem::FemAnalysis] Analysis
  Group = -> [MaterialSolid,SolverCcxTools,FEMMeshGmsh,ConstraintFixed,ConstraintFixed001]
FEATURE [App::Point] Origin047  label="Origin054"
  Role = Origin
FEATURE [Sketcher::SketchObject] Sketch
  ArcFitTolerance = 1e-06
  AttachmentSupport = -> [Origin046]
  ExternalTypes = [0]
  FullyConstrained = true
  MakeInternals = false
  MapMode = 5
  Placement = pos=(0,0,0) rot=(1,0,0;1.5708rad)
  sketch-geometry (38):
    g0: GeomPoint [constr] X=-6.15 Y=54.04 Z=0
    g1: GeomPoint [constr] X=-6.15 Y=36.2 Z=0
    g2: GeomPoint [constr] X=9.3 Y=45.12 Z=0
    g3: LineSegment [constr] StartX=-6.15 StartY=54.04 StartZ=0 EndX=-6.15 EndY=36.2 EndZ=0
    g4: LineSegment StartX=-14 StartY=27.2487 StartZ=0 EndX=-14 EndY=61.2715 EndZ=0
    g5: GeomPoint [constr] X=-8.53 Y=56.42 Z=0
    g6: ArcOfCircle [constr] CenterX=-6.15 CenterY=54.04 CenterZ=0 NormalX=0 NormalY=0 NormalZ=1 AngleXU=0 Radius=3.36583 StartAngle=2.35619 EndAngle=2.9147
    g7: LineSegment [constr] StartX=-9.42956 StartY=54.7971 StartZ=0 EndX=-3.0692 EndY=58.7715 EndZ=0
    g8: LineSegment [constr] StartX=-9.42956 StartY=54.7971 StartZ=0 EndX=-4.92525 EndY=47.5887 EndZ=0
    g9: GeomPoint [constr] X=-8.53 Y=38.58 Z=0
    g10: GeomPoint [constr] X=6.92 Y=47.5 Z=0
    g11: ArcOfCircle [constr] CenterX=-6.15 CenterY=36.2 CenterZ=0 NormalX=0 NormalY=0 NormalZ=1 AngleXU=0 Radius=3.36583 StartAngle=2.35619 EndAngle=2.9147
    g12: ArcOfCircle [constr] CenterX=9.3 CenterY=45.12 CenterZ=0 NormalX=0 NormalY=0 NormalZ=1 AngleXU=0 Radius=3.36583 StartAngle=2.35619 EndAngle=2.9147
    g13: LineSegment [constr] StartX=-9.42956 StartY=36.9571 StartZ=0 EndX=-3.0692 EndY=40.9315 EndZ=0
    g14: LineSegment [constr] StartX=-9.42956 StartY=36.9571 StartZ=0 EndX=-4.92525 EndY=29.7487 EndZ=0
    g15: LineSegment [constr] StartX=6.02044 StartY=45.8771 StartZ=0 EndX=12.3808 EndY=49.8515 EndZ=0
    g16: LineSegment [constr] StartX=6.02044 StartY=45.8771 StartZ=0 EndX=10.5248 EndY=38.6687 EndZ=0
    g17: ArcOfCircle CenterX=-9.42956 CenterY=54.7971 CenterZ=0 NormalX=0 NormalY=0 NormalZ=1 AngleXU=0 Radius=1.25 StartAngle=0.558505 EndAngle=5.27089
    g18: ArcOfCircle CenterX=6.02044 CenterY=45.8771 CenterZ=0 NormalX=0 NormalY=0 NormalZ=1 AngleXU=0 Radius=1.25 StartAngle=0.558505 EndAngle=5.27089
    g19: ArcOfCircle CenterX=-9.42956 CenterY=36.9571 CenterZ=0 NormalX=0 NormalY=0 NormalZ=1 AngleXU=0 Radius=1.25 StartAngle=0.558505 EndAngle=5.27089
    g20: LineSegment StartX=-8.3695 StartY=55.4595 StartZ=0 EndX=-3.0692 EndY=58.7715 EndZ=0
    g21: LineSegment StartX=6.68284 StartY=44.8171 StartZ=0 EndX=10.5248 EndY=38.6687 EndZ=0
    g22: LineSegment StartX=-8.76716 StartY=35.8971 StartZ=0 EndX=-4.92525 EndY=29.7487 EndZ=0
    g23: LineSegment StartX=-8.76716 StartY=53.7371 StartZ=0 EndX=-4.92525 EndY=47.5887 EndZ=0
    g24: LineSegment StartX=-8.3695 StartY=37.6195 StartZ=0 EndX=-3.0692 EndY=40.9315 EndZ=0
    g25: ArcOfCircle CenterX=-3.44116 CenterY=48.5161 CenterZ=0 NormalX=0 NormalY=0 NormalZ=1 AngleXU=0 Radius=1.75 StartAngle=3.7001 EndAngle=5.27089
    g26: ArcOfCircle CenterX=-2.14184 CenterY=39.4475 CenterZ=0 NormalX=0 NormalY=0 NormalZ=1 AngleXU=0 Radius=1.75 StartAngle=0.558505 EndAngle=2.1293
    g27: LineSegment StartX=5.99922 StartY=52.3515 StartZ=0 EndX=-2.51381 EndY=47.032 EndZ=0
    g28: LineSegment StartX=1.97049 StartY=36.1687 StartZ=0 EndX=-0.657759 EndY=40.3748 EndZ=0
    g29: LineSegment StartX=7.0805 StartY=46.5395 StartZ=0 EndX=12.3808 EndY=49.8515 EndZ=0
    g30: LineSegment StartX=-3.0692 StartY=58.7715 StartZ=0 EndX=-3.0692 EndY=61.2715 EndZ=0
    g31: LineSegment StartX=-4.92525 StartY=29.7487 StartZ=0 EndX=-4.92525 EndY=27.2487 EndZ=0
    g32: LineSegment StartX=12.3808 StartY=49.8515 StartZ=0 EndX=12.3808 EndY=52.3515 EndZ=0
    g33: LineSegment StartX=10.5248 StartY=38.6687 StartZ=0 EndX=10.5248 EndY=36.1687 EndZ=0
    g34: LineSegment StartX=12.3808 StartY=52.3515 StartZ=0 EndX=5.99922 EndY=52.3515 EndZ=0
    g35: LineSegment StartX=10.5248 StartY=36.1687 StartZ=0 EndX=1.97049 EndY=36.1687 EndZ=0
    g36: LineSegment StartX=-3.0692 StartY=61.2715 StartZ=0 EndX=-14 EndY=61.2715 EndZ=0
    g37: LineSegment StartX=-4.92525 StartY=27.2487 StartZ=0 EndX=-14 EndY=27.2487 EndZ=0
  constraints (99):
    c: Coincident(g3,g0)
    c: Coincident(g3,g1)
    c: Vertical(g3)
    c: Distance(g-1,g3) = 6.15
    c: DistanceX(g-2,g2) = 9.3
    c: DistanceY(g-1,g1) = 36.2
    c: DistanceY(g-1,g0) = 54.04
    c: DistanceY(g-1,g2) = 45.12
    c: Vertical(g4)
    c: Distance(g-1,g4) = 14
    c: DistanceX(g5,g0) = 2.38
    c: DistanceY(g0,g5) = 2.38
    c: Coincident(g6,g0)
    c: Coincident(g6,g5)
    c: Angle(g6) = 0.558505
    c: Coincident(g7,g6)
    c: Angle(g-1,g7) = 0.558505
    c: Coincident(g8,g6)
    c: Angle(g8,g7) = 1.5708
    c: Distance(g7) = 7.5
    c: Distance(g8) = 8.5
    c: DistanceY(g1,g9) = 2.38
    c: DistanceX(g9,g1) = 2.38
    c: DistanceY(g2,g10) = 2.38
    c: DistanceX(g10,g2) = 2.38
    c: Coincident(g11,g1)
    c: Coincident(g11,g9)
    c: Coincident(g12,g2)
    c: Coincident(g12,g10)
    c: Angle(g11) = 0.558505
    c: Angle(g12) = 0.558505
    c: Coincident(g13,g11)
    c: Coincident(g14,g11)
    c: Coincident(g15,g12)
    c: Coincident(g16,g12)
    c: Parallel(g7,g15)
    c: Parallel(g7,g13)
    c: Parallel(g8,g16)
    c: Parallel(g8,g14)
    c: Equal(g7,g15)
    c: Equal(g7,g13)
    c: Equal(g8,g16)
    c: Equal(g8,g14)
    c: Coincident(g17,g6)
    c: PointOnObject(g17,g7)
    c: PointOnObject(g17,g8)
    c: Coincident(g18,g12)
    c: PointOnObject(g18,g15)
    c: PointOnObject(g18,g16)
    c: Coincident(g19,g11)
    c: PointOnObject(g19,g13)
    c: PointOnObject(g19,g14)
    c: Radius(g17) = 1.25
    c: Equal(g17,g18)
    c: Equal(g17,g19)
    c: Coincident(g20,g17)
    c: Coincident(g20,g7)
    c: Coincident(g21,g18)
    c: Coincident(g21,g16)
    c: Coincident(g22,g19)
    c: Coincident(g22,g14)
    c: Coincident(g23,g17)
    c: Coincident(g23,g8)
    c: Coincident(g24,g19)
    c: Coincident(g24,g13)
    c: Tangent(g25,g8) = -1.5708
    c: Tangent(g26,g13) = 1.5708
    c: Radius(g25) = 1.75
    c: Equal(g26,g25)
    c: Angle(g25) = 1.5708
    c: Angle(g26) = 1.5708
    c: Tangent(g25,g27) = 1.5708
    c: Tangent(g26,g28) = -1.5708
    c: Coincident(g29,g18)
    c: Coincident(g29,g15)
    c: Coincident(g30,g7)
    c: Vertical(g30)
    c: Coincident(g31,g14)
    c: Vertical(g31)
    c: Coincident(g32,g15)
    c: Vertical(g32)
    c: Coincident(g33,g16)
    c: Vertical(g33)
    c: Coincident(g34,g32)
    c: Horizontal(g34)
    c: Coincident(g35,g33)
    c: Horizontal(g35)
    c: Coincident(g36,g30)
    c: Horizontal(g36)
    c: Coincident(g37,g31)
    c: Horizontal(g37)
    c: Coincident(g4,g36)
    c: Coincident(g37,g4)
    c: Coincident(g27,g34)
    c: Coincident(g28,g35)
    c: Distance(g32,g32) = 2.5
    c: Equal(g33,g32)
    c: Equal(g32,g30)
    c: Equal(g30,g31)
FEATURE [PartDesign::Pad] Pad
  Direction = (0,-1,2e-16)
  Length = 4
  Length2 = 10
  Profile = -> Sketch
  ReferenceAxis = -> Sketch [N_Axis]
  Refine = true
  Reversed = true
  SideType = 0
  Suppressed = false
  Type = 0
  Type2 = 0
FEATURE [App::Point] Origin049  label="Origin057"
  Role = Origin
FEATURE [Sketcher::SketchObject] Sketch032
  ArcFitTolerance = 1e-06
  AttachmentSupport = -> [Origin048]
  ExternalTypes = [0]
  FullyConstrained = true
  MakeInternals = false
  MapMode = 5
  sketch-geometry (11):
    g0: GeomPoint [constr] X=-2.38 Y=-2.38 Z=0
    g1: LineSegment [constr] StartX=-2.38 StartY=-2.38 StartZ=0 EndX=-2.38 EndY=6.12 EndZ=0
    g2: LineSegment [constr] StartX=-2.38 StartY=-2.38 StartZ=0 EndX=5.12 EndY=-2.38 EndZ=0
    g3: ArcOfCircle CenterX=-2.38 CenterY=-2.38 CenterZ=0 NormalX=0 NormalY=0 NormalZ=1 AngleXU=0 Radius=1.25 StartAngle=1.5708 EndAngle=6.28319
    g4: LineSegment StartX=-2.38 StartY=-1.13 StartZ=0 EndX=-2.38 EndY=6.12 EndZ=0
    g5: LineSegment StartX=-1.13 StartY=-2.38 StartZ=0 EndX=5.12 EndY=-2.38 EndZ=0
    g6: LineSegment StartX=-11.9333 StartY=0.102233 StartZ=0 EndX=-0.397767 EndY=-11.4333 EndZ=0
    g7: LineSegment StartX=-2.38 StartY=6.12 StartZ=0 EndX=-4.14777 EndY=7.88777 EndZ=0
    g8: LineSegment StartX=5.12 StartY=-2.38 StartZ=0 EndX=6.88777 EndY=-4.14777 EndZ=0
    g9: LineSegment StartX=6.88777 StartY=-4.14777 StartZ=0 EndX=-0.397767 EndY=-11.4333 EndZ=0
    g10: LineSegment StartX=-4.14777 StartY=7.88777 StartZ=0 EndX=-11.9333 EndY=0.102233 EndZ=0
  constraints (30):
    c: DistanceX(g-2,g0) = -2.38
    c: DistanceY(g-1,g0) = -2.38
    c: Coincident(g1,g0)
    c: Vertical(g1)
    c: Coincident(g2,g0)
    c: Horizontal(g2)
    c: DistanceY(g1,g1) = 8.5
    c: DistanceX(g2,g2) = 7.5
    c: Coincident(g3,g0)
    c: PointOnObject(g3,g1)
    c: PointOnObject(g3,g2)
    c: Radius(g3) = 1.25
    c: Coincident(g4,g3)
    c: Coincident(g4,g1)
    c: Coincident(g5,g3)
    c: Coincident(g5,g2)
    c: Distance(g0,g6) = 5
    c: Coincident(g7,g1)
    c: Coincident(g8,g2)
    c: Coincident(g10,g7)
    c: Coincident(g6,g10)
    c: Coincident(g6,g9)
    c: Parallel(g9,g10)
    c: Coincident(g9,g8)
    c: Angle(g5,g8) = 2.35619
    c: Angle(g8,g9) = 1.5708
    c: Parallel(g7,g8)
    c: Parallel(g6,g8)
    c: Equal(g7,g8)
    c: Distance(g7,g7) = 2.5
FEATURE [PartDesign::Pad] Pad009
  Direction = (0,0,1)
  Length = 5
  Length2 = 10
  Profile = -> Sketch032
  ReferenceAxis = -> Sketch032 [N_Axis]
  Refine = true
  SideType = 0
  Suppressed = false
  Type = 0
  Type2 = 0
FEATURE [App::Point] Origin051  label="Origin060"
  Role = Origin
FEATURE [Sketcher::SketchObject] Sketch033
  ArcFitTolerance = 1e-06
  AttachmentSupport = -> [Origin050]
  ExternalTypes = [0]
  FullyConstrained = true
  MakeInternals = false
  MapMode = 5
  sketch-geometry (12):
    g0: GeomPoint [constr] X=0 Y=14.39 Z=0
    g1: GeomPoint [constr] X=-4.76 Y=9.63 Z=0
    g2: LineSegment [constr] StartX=-4.76 StartY=9.63 StartZ=0 EndX=-4.76 EndY=23.63 EndZ=0
    g3: LineSegment [constr] StartX=-4.76 StartY=9.63 StartZ=0 EndX=9.24 EndY=9.63 EndZ=0
    g4: ArcOfCircle CenterX=-4.76 CenterY=9.63 CenterZ=0 NormalX=0 NormalY=0 NormalZ=1 AngleXU=0 Radius=2.5 StartAngle=1.5708 EndAngle=6.28319
    g5: LineSegment StartX=-4.76 StartY=12.13 StartZ=0 EndX=-4.76 EndY=23.63 EndZ=0
    g6: LineSegment StartX=9.24 StartY=9.63 StartZ=0 EndX=-2.26 EndY=9.63 EndZ=0
    g7: LineSegment StartX=-20.5988 StartY=11.3267 StartZ=0 EndX=-3.0633 EndY=-6.20883 EndZ=0
    g8: LineSegment StartX=9.24 StartY=9.63 StartZ=0 EndX=11.0078 EndY=7.86223 EndZ=0
    g9: LineSegment StartX=11.0078 StartY=7.86223 StartZ=0 EndX=-3.0633 EndY=-6.20883 EndZ=0
    g10: LineSegment StartX=-4.76 StartY=23.63 StartZ=0 EndX=-6.52777 EndY=25.3978 EndZ=0
    g11: LineSegment StartX=-6.52777 StartY=25.3978 StartZ=0 EndX=-20.5988 EndY=11.3267 EndZ=0
  constraints (32):
    c: PointOnObject(g0,g-2)
    c: Distance(g0,g-1) = 14.39
    c: DistanceX(g1,g0) = 4.76
    c: DistanceY(g1,g0) = 4.76
    c: Coincident(g2,g1)
    c: Vertical(g2)
    c: Coincident(g3,g1)
    c: Horizontal(g3)
    c: DistanceY(g2,g2) = 14
    c: DistanceX(g3,g3) = 14
    c: Coincident(g4,g1)
    c: PointOnObject(g4,g2)
    c: PointOnObject(g4,g3)
    c: Coincident(g5,g4)
    c: Coincident(g5,g2)
    c: Coincident(g6,g3)
    c: Coincident(g6,g4)
    c: Radius(g4) = 2.5
    c: Distance(g1,g7) = 10
    c: Coincident(g8,g3)
    c: Coincident(g9,g8)
    c: Coincident(g10,g2)
    c: Coincident(g11,g10)
    c: Coincident(g7,g9)
    c: Coincident(g7,g11)
    c: Angle(g6,g8) = 2.35619
    c: Angle(g8,g9) = 1.5708
    c: Parallel(g9,g11)
    c: Parallel(g8,g10)
    c: Parallel(g10,g7)
    c: Equal(g8,g10)
    c: Distance(g10,g10) = 2.5
FEATURE [PartDesign::Pad] Pad010
  Direction = (0,0,1)
  Length = 10
  Length2 = 10
  Profile = -> Sketch033
  ReferenceAxis = -> Sketch033 [N_Axis]
  Refine = true
  SideType = 0
  Suppressed = false
  Type = 0
  Type2 = 0
FEATURE [App::Point] Origin053
  Role = Origin
FEATURE [Sketcher::SketchObject] Sketch034
  ArcFitTolerance = 1e-06
  AttachmentSupport = -> [Origin052]
  ExternalTypes = [0]
  FullyConstrained = true
  MakeInternals = false
  MapMode = 5
  sketch-geometry (14):
    g0: GeomPoint [constr] X=-2.38 Y=-2.38 Z=0
    g1: LineSegment [constr] StartX=-2.38 StartY=-2.38 StartZ=0 EndX=-2.38 EndY=5.12 EndZ=0
    g2: LineSegment [constr] StartX=-2.38 StartY=-2.38 StartZ=0 EndX=5.12 EndY=-2.38 EndZ=0
    g3: LineSegment StartX=-10.4333 StartY=-1.39777 StartZ=0 EndX=-1.39777 EndY=-10.4333 EndZ=0
    g4: LineSegment [constr] StartX=5.12 StartY=-2.38 StartZ=0 EndX=5.12 EndY=-0.38 EndZ=0
    g5: LineSegment [constr] StartX=-2.38 StartY=5.12 StartZ=0 EndX=-0.38 EndY=5.12 EndZ=0
    g6: ArcOfCircle CenterX=0.1 CenterY=0.1 CenterZ=0 NormalX=0 NormalY=0 NormalZ=1 AngleXU=0 Radius=2.15 StartAngle=2.79648 EndAngle=5.05751
    g7: LineSegment StartX=-0.38 StartY=5.12 StartZ=0 EndX=-1.92323 EndY=0.827361 EndZ=0
    g8: LineSegment StartX=5.12 StartY=-0.38 StartZ=0 EndX=0.827361 EndY=-1.92323 EndZ=0
    g9: LineSegment StartX=-0.38 StartY=5.12 StartZ=0 EndX=-2.14777 EndY=6.88777 EndZ=0
    g10: LineSegment StartX=-2.14777 StartY=6.88777 StartZ=0 EndX=-10.4333 EndY=-1.39777 EndZ=0
    g11: LineSegment StartX=5.12 StartY=-0.38 StartZ=0 EndX=6.88777 EndY=-2.14777 EndZ=0
    g12: LineSegment StartX=6.88777 StartY=-2.14777 StartZ=0 EndX=-1.39777 EndY=-10.4333 EndZ=0
    g13: LineSegment [constr] StartX=-0.38 StartY=5.12 StartZ=0 EndX=5.12 EndY=-0.38 EndZ=0
  constraints (37):
    c: DistanceX(g-2,g0) = -2.38
    c: DistanceY(g-1,g0) = -2.38
    c: Coincident(g1,g0)
    c: Vertical(g1)
    c: Coincident(g2,g0)
    c: Horizontal(g2)
    c: DistanceX(g2,g2) = 7.5
    c: Distance(g0,g3) = 5
    c: Coincident(g4,g2)
    c: Vertical(g4)
    c: Coincident(g5,g1)
    c: Horizontal(g5)
    c: Radius(g6) = 2.15
    c: Equal(g1,g2)
    c: Equal(g4,g5)
    c: Coincident(g7,g5)
    c: Coincident(g8,g4)
    c: Tangent(g8,g6) = 1.5708
    c: Tangent(g6,g7) = -1.5708
    c: Distance(g5,g5) = 2
    c: Coincident(g9,g5)
    c: Coincident(g10,g9)
    c: Coincident(g11,g4)
    c: Coincident(g12,g11)
    c: Coincident(g3,g10)
    c: Coincident(g3,g12)
    c: Parallel(g11,g9)
    c: Angle(g10,g9) = 1.5708
    c: Parallel(g12,g10)
    c: Equal(g9,g11)
    c: Parallel(g9,g3)
    c: Coincident(g13,g5)
    c: Coincident(g13,g4)
    c: Parallel(g13,g9)
    c: Distance(g11,g11) = 2.5
    c: DistanceX(g-1,g6) = 0.1
    c: DistanceY(g-1,g6) = 0.1
FEATURE [PartDesign::Pad] Pad011
  Direction = (0,0,1)
  Length = 4
  Length2 = 10
  Profile = -> Sketch034
  ReferenceAxis = -> Sketch034 [N_Axis]
  Refine = true
  SideType = 0
  Suppressed = false
  Type = 0
  Type2 = 0
FEATURE [Sketcher::SketchObject] Sketch035
  ArcFitTolerance = 1e-06
  AttachmentSupport = -> [Origin052]
  ExternalTypes = [0]
  FullyConstrained = true
  MakeInternals = false
  MapMode = 5
  sketch-geometry (8):
    g0: GeomPoint [constr] X=-2.38 Y=-2.38 Z=0
    g1: LineSegment [constr] StartX=-2.38 StartY=-2.38 StartZ=0 EndX=-2.38 EndY=7.62 EndZ=0
    g2: LineSegment [constr] StartX=-2.38 StartY=-2.38 StartZ=0 EndX=7.62 EndY=-2.38 EndZ=0
    g3: ArcOfCircle CenterX=-2.38 CenterY=-2.38 CenterZ=0 NormalX=0 NormalY=0 NormalZ=1 AngleXU=0 Radius=1.25 StartAngle=1.5708 EndAngle=6.28319
    g4: LineSegment StartX=-2.38 StartY=-1.13 StartZ=0 EndX=-2.38 EndY=7.62 EndZ=0
    g5: LineSegment StartX=-1.13 StartY=-2.38 StartZ=0 EndX=7.62 EndY=-2.38 EndZ=0
    g6: LineSegment StartX=-2.38 StartY=7.62 StartZ=0 EndX=7.62 EndY=7.62 EndZ=0
    g7: LineSegment StartX=7.62 StartY=7.62 StartZ=0 EndX=7.62 EndY=-2.38 EndZ=0
  constraints (21):
    c: DistanceY(g0,g-1) = 2.38
    c: DistanceX(g0,g-1) = 2.38
    c: Coincident(g1,g0)
    c: Vertical(g1)
    c: Coincident(g2,g0)
    c: Horizontal(g2)
    c: Equal(g2,g1)
    c: Distance(g1,g1) = 10
    c: Coincident(g3,g0)
    c: PointOnObject(g3,g1)
    c: PointOnObject(g3,g2)
    c: Radius(g3) = 1.25
    c: Coincident(g4,g3)
    c: Coincident(g4,g1)
    c: Coincident(g5,g3)
    c: Coincident(g5,g2)
    c: Coincident(g6,g1)
    c: Horizontal(g6)
    c: Coincident(g7,g6)
    c: Coincident(g7,g2)
    c: Vertical(g7)
FEATURE [PartDesign::Pocket] Pocket
  BaseFeature = -> Pad011
  Direction = (0,0,-1)
  Length = 1.89
  Length2 = 5
  Profile = -> Sketch035
  ReferenceAxis = -> Sketch035 [N_Axis]
  Refine = true
  Reversed = true
  SideType = 0
  Suppressed = false
  Type = 0
  Type2 = 0
FEATURE [PartDesign::Fillet] Fillet
  Base = -> Pocket007 [Edge2,Edge128]
  BaseFeature = -> Pocket007
  Radius = 1
  Refine = true
  SupportTransform = false
  Suppressed = false
  UseAllEdges = false
FEATURE [PartDesign::Fillet] Fillet001
  Base = -> Fillet [Edge6,Edge81,Edge73,Edge53]
  BaseFeature = -> Fillet
  Radius = 2
  Refine = true
  SupportTransform = false
  Suppressed = false
  UseAllEdges = false
FEATURE [PartDesign::Fillet] Fillet002
  Base = -> Pad [Edge5,Edge20,Edge41,Edge50]
  BaseFeature = -> Pad
  Radius = 0.5
  Refine = true
  SupportTransform = false
  Suppressed = false
  UseAllEdges = false
FEATURE [PartDesign::Fillet] Fillet003
  Base = -> Fillet002 [Edge72,Edge70,Edge69,Edge71,Edge32,Edge3]
  BaseFeature = -> Fillet002
  Radius = 0.5
  Refine = true
  SupportTransform = false
  Suppressed = false
  UseAllEdges = false
FEATURE [PartDesign::Fillet] Fillet004
  Base = -> Fillet003 [Edge72,Edge74,Edge76,Edge70,Edge79,Edge96]
  BaseFeature = -> Fillet003
  Radius = 2
  Refine = true
  SupportTransform = false
  Suppressed = false
  UseAllEdges = false
FEATURE [PartDesign::Fillet] Fillet005
  Base = -> Pad010 [Edge1,Edge5,Edge2,Edge8]
  BaseFeature = -> Pad010
  Radius = 0.5
  Refine = true
  SupportTransform = false
  Suppressed = false
  UseAllEdges = false
FEATURE [PartDesign::Fillet] Fillet006
  Base = -> Fillet005 [Edge30,Edge36,Edge32,Edge34]
  BaseFeature = -> Fillet005
  Radius = 2
  Refine = true
  SupportTransform = false
  Suppressed = false
  UseAllEdges = false
FEATURE [PartDesign::Body] Body011  label="Fine Piezo Aligner"
  AllowCompound = false
  Group = -> [Sketch033,Pad010,Fillet005,Fillet006]
  Origin = -> Origin050
  Placement = pos=(0,0,16.66) rot=(0,0,1;0rad)
  Tip = -> Fillet006
FEATURE [PartDesign::Fillet] Fillet007
  Base = -> Pad009 [Edge5,Edge8,Edge1,Edge11]
  BaseFeature = -> Pad009
  Radius = 0.5
  Refine = true
  SupportTransform = false
  Suppressed = false
  UseAllEdges = false
FEATURE [PartDesign::Fillet] Fillet008
  Base = -> Fillet007 [Edge3,Edge32,Edge18,Edge30]
  BaseFeature = -> Fillet007
  Radius = 2
  Refine = true
  SupportTransform = false
  Suppressed = false
  UseAllEdges = false
FEATURE [PartDesign::Body] Body010  label="Coarse Piezo Aligner 1"
  AllowCompound = false
  Group = -> [Sketch032,Pad009,Fillet007,Fillet008]
  Origin = -> Origin048
  Tip = -> Fillet008
FEATURE [PartDesign::Fillet] Fillet009
  Base = -> Pocket [Edge4,Edge28,Edge34,Edge26]
  BaseFeature = -> Pocket
  Radius = 0.5
  Refine = true
  SupportTransform = false
  Suppressed = false
  UseAllEdges = false
FEATURE [PartDesign::Fillet] Fillet010
  Base = -> Fillet009 [Edge3,Edge44,Edge22,Edge43]
  BaseFeature = -> Fillet009
  Radius = 2
  Refine = true
  SupportTransform = false
  Suppressed = false
  UseAllEdges = false
FEATURE [PartDesign::Body] Body012  label="Coarse Piezo Aligner 2"
  AllowCompound = false
  Group = -> [Sketch034,Pad011,Sketch035,Pocket,Fillet009,Fillet010]
  Origin = -> Origin052
  Placement = pos=(0,0,2) rot=(0,0,1;0rad)
  Tip = -> Fillet010
FEATURE [PartDesign::Fillet] Fillet011
  Base = -> Fillet001 [Edge63,Edge91]
  BaseFeature = -> Fillet001
  Radius = 0.5
  Refine = true
  SupportTransform = false
  Suppressed = false
  UseAllEdges = false
FEATURE [PartDesign::Body] Body001  label="PreAmp Shield"
  AllowCompound = false
  Group = -> [Sketch003,Pad001,Sketch004,Pocket002,Sketch006,Pocket003,Sketch007,Pocket004,Sketch008,Pocket005,Sketch009,Pocket006,Sketch010,Pocket007,Fillet,Fillet001,Fillet011]
  Origin = -> Origin026
  Placement = pos=(0,9.33,43.08) rot=(1,0,0;4.71239rad)
  Tip = -> Fillet011
FEATURE [App::DocumentObjectGroup] Group007  label="PreAmp"
  Group = -> [Board_e57a,Body001,Group006,Cylinder113]
FEATURE [PartDesign::Fillet] Fillet012
  Base = -> Fillet004 [Edge102,Edge72]
  BaseFeature = -> Fillet004
  Radius = 2
  Refine = true
  SupportTransform = false
  Suppressed = false
  UseAllEdges = false
FEATURE [PartDesign::Body] Body  label="Kinematic Mount Aligner"
  AllowCompound = false
  Group = -> [Sketch,Pad,Fillet002,Fillet003,Fillet004,Fillet012]
  Origin = -> Origin046
  Tip = -> Fillet012
